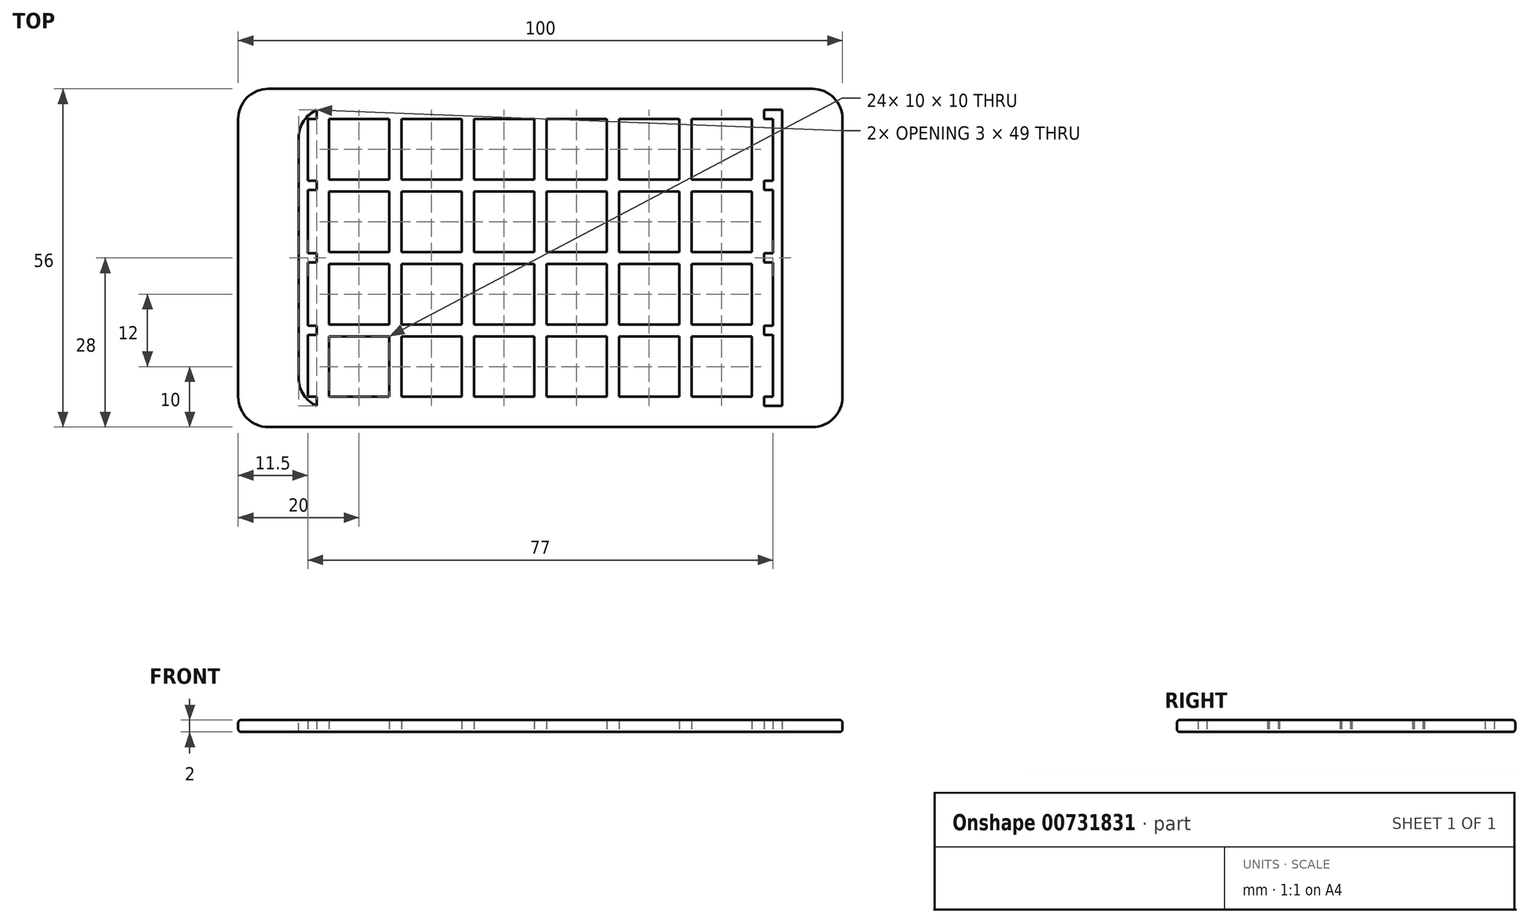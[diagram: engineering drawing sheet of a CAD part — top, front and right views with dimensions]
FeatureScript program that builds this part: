
annotation { "Feature Type Name" : "Feature", "Feature Type Description" : "" }
export const myFeature = defineFeature(function(context is Context, id is Id, definition is map)
    precondition{}
    {
        {
            var Q0;
            Q0=qCreatedBy(makeId("Top.planeOp"),FACE);
            var sketch = newSketch(context, id + "F0", { "sketchPlane" : qUnion([Q0])});
            skLineSegment(sketch, "E0.bottom", {"start": v(5, -5) * mm, "end": v(-5, -5) * mm});
            skLineSegment(sketch, "E0.top", {"start": v(5, 5) * mm, "end": v(-5, 5) * mm});
            skLineSegment(sketch, "E0.left", {"start": v(5, -5) * mm, "end": v(5, 5) * mm});
            skLineSegment(sketch, "E0.right", {"start": v(-5, -5) * mm, "end": v(-5, 5) * mm});
            skPoint(sketch, "E0.middle", {"position": v(0, 0) * mm});
            skPoint(sketch, "E1.0.1.0", {"position": v(0, 12) * mm});
            skLineSegment(sketch, "E1.0.1.1", {"start": v(5, 7) * mm, "end": v(-5, 7) * mm});
            skLineSegment(sketch, "E1.0.1.2", {"start": v(-5, 7) * mm, "end": v(-5, 17) * mm});
            skLineSegment(sketch, "E1.0.1.3", {"start": v(5, 7) * mm, "end": v(5, 17) * mm});
            skLineSegment(sketch, "E1.0.1.4", {"start": v(5, 17) * mm, "end": v(-5, 17) * mm});
            skPoint(sketch, "E1.0.2.0", {"position": v(0, 24) * mm});
            skLineSegment(sketch, "E1.0.2.1", {"start": v(5, 19) * mm, "end": v(-5, 19) * mm});
            skLineSegment(sketch, "E1.0.2.2", {"start": v(-5, 19) * mm, "end": v(-5, 29) * mm});
            skLineSegment(sketch, "E1.0.2.3", {"start": v(5, 19) * mm, "end": v(5, 29) * mm});
            skLineSegment(sketch, "E1.0.2.4", {"start": v(5, 29) * mm, "end": v(-5, 29) * mm});
            skPoint(sketch, "E1.1.0.0", {"position": v(12, 0) * mm});
            skLineSegment(sketch, "E1.1.0.1", {"start": v(17, -5) * mm, "end": v(7, -5) * mm});
            skLineSegment(sketch, "E1.1.0.2", {"start": v(7, -5) * mm, "end": v(7, 5) * mm});
            skLineSegment(sketch, "E1.1.0.3", {"start": v(17, -5) * mm, "end": v(17, 5) * mm});
            skLineSegment(sketch, "E1.1.0.4", {"start": v(17, 5) * mm, "end": v(7, 5) * mm});
            skPoint(sketch, "E1.1.1.0", {"position": v(12, 12) * mm});
            skLineSegment(sketch, "E1.1.1.1", {"start": v(17, 7) * mm, "end": v(7, 7) * mm});
            skLineSegment(sketch, "E1.1.1.2", {"start": v(7, 7) * mm, "end": v(7, 17) * mm});
            skLineSegment(sketch, "E1.1.1.3", {"start": v(17, 7) * mm, "end": v(17, 17) * mm});
            skLineSegment(sketch, "E1.1.1.4", {"start": v(17, 17) * mm, "end": v(7, 17) * mm});
            skPoint(sketch, "E1.1.2.0", {"position": v(12, 24) * mm});
            skLineSegment(sketch, "E1.1.2.1", {"start": v(17, 19) * mm, "end": v(7, 19) * mm});
            skLineSegment(sketch, "E1.1.2.2", {"start": v(7, 19) * mm, "end": v(7, 29) * mm});
            skLineSegment(sketch, "E1.1.2.3", {"start": v(17, 19) * mm, "end": v(17, 29) * mm});
            skLineSegment(sketch, "E1.1.2.4", {"start": v(17, 29) * mm, "end": v(7, 29) * mm});
            skPoint(sketch, "E1.2.0.0", {"position": v(24, 0) * mm});
            skLineSegment(sketch, "E1.2.0.1", {"start": v(29, -5) * mm, "end": v(19, -5) * mm});
            skLineSegment(sketch, "E1.2.0.2", {"start": v(19, -5) * mm, "end": v(19, 5) * mm});
            skLineSegment(sketch, "E1.2.0.3", {"start": v(29, -5) * mm, "end": v(29, 5) * mm});
            skLineSegment(sketch, "E1.2.0.4", {"start": v(29, 5) * mm, "end": v(19, 5) * mm});
            skPoint(sketch, "E1.2.1.0", {"position": v(24, 12) * mm});
            skLineSegment(sketch, "E1.2.1.1", {"start": v(29, 7) * mm, "end": v(19, 7) * mm});
            skLineSegment(sketch, "E1.2.1.2", {"start": v(19, 7) * mm, "end": v(19, 17) * mm});
            skLineSegment(sketch, "E1.2.1.3", {"start": v(29, 7) * mm, "end": v(29, 17) * mm});
            skLineSegment(sketch, "E1.2.1.4", {"start": v(29, 17) * mm, "end": v(19, 17) * mm});
            skPoint(sketch, "E1.2.2.0", {"position": v(24, 24) * mm});
            skLineSegment(sketch, "E1.2.2.1", {"start": v(29, 19) * mm, "end": v(19, 19) * mm});
            skLineSegment(sketch, "E1.2.2.2", {"start": v(19, 19) * mm, "end": v(19, 29) * mm});
            skLineSegment(sketch, "E1.2.2.3", {"start": v(29, 19) * mm, "end": v(29, 29) * mm});
            skLineSegment(sketch, "E1.2.2.4", {"start": v(29, 29) * mm, "end": v(19, 29) * mm});
            skLineSegment(sketch, "E1.direction1", {"start": v(-5, -5) * mm, "end": v(7, -5) * mm, "construction": true});
            skLineSegment(sketch, "E1.direction2", {"start": v(-5, -5) * mm, "end": v(-5, 7) * mm, "construction": true});
            skLineSegment(sketch, "E2.1.0.0", {"start": v(-31, 19) * mm, "end": v(-31, 29) * mm});
            skLineSegment(sketch, "E2.1.0.1", {"start": v(-17, 7) * mm, "end": v(-17, 17) * mm});
            skLineSegment(sketch, "E2.1.0.2", {"start": v(-7, -5) * mm, "end": v(-7, 5) * mm});
            skLineSegment(sketch, "E2.1.0.3", {"start": v(-7, 19) * mm, "end": v(-17, 19) * mm});
            skPoint(sketch, "E2.1.0.4", {"position": v(-24, 12) * mm});
            skLineSegment(sketch, "E2.1.0.5", {"start": v(-19, -5) * mm, "end": v(-19, 5) * mm});
            skLineSegment(sketch, "E2.1.0.6", {"start": v(-41, -5) * mm, "end": v(-29, -5) * mm, "construction": true});
            skLineSegment(sketch, "E2.1.0.7", {"start": v(-31, 5) * mm, "end": v(-41, 5) * mm});
            skLineSegment(sketch, "E2.1.0.8", {"start": v(-41, -5) * mm, "end": v(-41, 7) * mm, "construction": true});
            skPoint(sketch, "E2.1.0.9", {"position": v(-12, 12) * mm});
            skPoint(sketch, "E2.1.0.10", {"position": v(-36, 0) * mm});
            skPoint(sketch, "E2.1.0.11", {"position": v(-12, 24) * mm});
            skLineSegment(sketch, "E2.1.0.12", {"start": v(-31, 7) * mm, "end": v(-31, 17) * mm});
            skLineSegment(sketch, "E2.1.0.13", {"start": v(-29, 19) * mm, "end": v(-29, 29) * mm});
            skLineSegment(sketch, "E2.1.0.14", {"start": v(-31, 7) * mm, "end": v(-41, 7) * mm});
            skLineSegment(sketch, "E2.1.0.15", {"start": v(-31, 19) * mm, "end": v(-41, 19) * mm});
            skLineSegment(sketch, "E2.1.0.16", {"start": v(-19, 17) * mm, "end": v(-29, 17) * mm});
            skLineSegment(sketch, "E2.1.0.17", {"start": v(-19, 29) * mm, "end": v(-29, 29) * mm});
            skLineSegment(sketch, "E2.1.0.18", {"start": v(-19, 19) * mm, "end": v(-29, 19) * mm});
            skLineSegment(sketch, "E2.1.0.19", {"start": v(-7, 7) * mm, "end": v(-17, 7) * mm});
            skLineSegment(sketch, "E2.1.0.20", {"start": v(-19, -5) * mm, "end": v(-29, -5) * mm});
            skLineSegment(sketch, "E2.1.0.21", {"start": v(-41, 19) * mm, "end": v(-41, 29) * mm});
            skLineSegment(sketch, "E2.1.0.22", {"start": v(-29, -5) * mm, "end": v(-29, 5) * mm});
            skLineSegment(sketch, "E2.1.0.23", {"start": v(-19, 5) * mm, "end": v(-29, 5) * mm});
            skPoint(sketch, "E2.1.0.24", {"position": v(-36, 12) * mm});
            skLineSegment(sketch, "E2.1.0.25", {"start": v(-7, -5) * mm, "end": v(-17, -5) * mm});
            skPoint(sketch, "E2.1.0.26", {"position": v(-24, 0) * mm});
            skLineSegment(sketch, "E2.1.0.27", {"start": v(-7, 29) * mm, "end": v(-17, 29) * mm});
            skLineSegment(sketch, "E2.1.0.28", {"start": v(-41, 7) * mm, "end": v(-41, 17) * mm});
            skPoint(sketch, "E2.1.0.29", {"position": v(-24, 24) * mm});
            skLineSegment(sketch, "E2.1.0.30", {"start": v(-19, 7) * mm, "end": v(-29, 7) * mm});
            skPoint(sketch, "E2.1.0.31", {"position": v(-36, 24) * mm});
            skLineSegment(sketch, "E2.1.0.32", {"start": v(-31, 29) * mm, "end": v(-41, 29) * mm});
            skLineSegment(sketch, "E2.1.0.33", {"start": v(-31, -5) * mm, "end": v(-31, 5) * mm});
            skLineSegment(sketch, "E2.1.0.34", {"start": v(-7, 5) * mm, "end": v(-17, 5) * mm});
            skLineSegment(sketch, "E2.1.0.35", {"start": v(-7, 7) * mm, "end": v(-7, 17) * mm});
            skLineSegment(sketch, "E2.1.0.36", {"start": v(-29, 7) * mm, "end": v(-29, 17) * mm});
            skLineSegment(sketch, "E2.1.0.37", {"start": v(-17, 19) * mm, "end": v(-17, 29) * mm});
            skLineSegment(sketch, "E2.1.0.38", {"start": v(-31, 17) * mm, "end": v(-41, 17) * mm});
            skPoint(sketch, "E2.1.0.39", {"position": v(-12, 0) * mm});
            skLineSegment(sketch, "E2.1.0.40", {"start": v(-17, -5) * mm, "end": v(-17, 5) * mm});
            skLineSegment(sketch, "E2.1.0.41", {"start": v(-19, 19) * mm, "end": v(-19, 29) * mm});
            skLineSegment(sketch, "E2.1.0.42", {"start": v(-7, 17) * mm, "end": v(-17, 17) * mm});
            skLineSegment(sketch, "E2.1.0.43", {"start": v(-19, 7) * mm, "end": v(-19, 17) * mm});
            skLineSegment(sketch, "E2.1.0.44", {"start": v(-7, 19) * mm, "end": v(-7, 29) * mm});
            skLineSegment(sketch, "E2.1.0.45", {"start": v(-41, -5) * mm, "end": v(-41, 5) * mm});
            skLineSegment(sketch, "E2.1.0.46", {"start": v(-31, -5) * mm, "end": v(-41, -5) * mm});
            skLineSegment(sketch, "E2.direction1", {"start": v(-5, -5) * mm, "end": v(-41, -5) * mm, "construction": true});
            skPoint(sketch, "E3.0.1.0", {"position": v(24, -12) * mm});
            skLineSegment(sketch, "E3.0.1.1", {"start": v(19, -17) * mm, "end": v(19, -7) * mm});
            skLineSegment(sketch, "E3.0.1.2", {"start": v(7, -17) * mm, "end": v(7, -7) * mm});
            skLineSegment(sketch, "E3.0.1.3", {"start": v(17, -7) * mm, "end": v(7, -7) * mm});
            skLineSegment(sketch, "E3.0.1.4", {"start": v(29, -17) * mm, "end": v(19, -17) * mm});
            skLineSegment(sketch, "E3.0.1.5", {"start": v(-19, -7) * mm, "end": v(-29, -7) * mm});
            skLineSegment(sketch, "E3.0.1.6", {"start": v(-7, -7) * mm, "end": v(-17, -7) * mm});
            skLineSegment(sketch, "E3.0.1.7", {"start": v(5, -7) * mm, "end": v(-5, -7) * mm});
            skLineSegment(sketch, "E3.0.1.8", {"start": v(5, -17) * mm, "end": v(5, -7) * mm});
            skLineSegment(sketch, "E3.0.1.9", {"start": v(17, -17) * mm, "end": v(17, -7) * mm});
            skLineSegment(sketch, "E3.0.1.10", {"start": v(-29, -17) * mm, "end": v(-29, -7) * mm});
            skLineSegment(sketch, "E3.0.1.11", {"start": v(-7, -17) * mm, "end": v(-7, -7) * mm});
            skLineSegment(sketch, "E3.0.1.12", {"start": v(-31, -17) * mm, "end": v(-31, -7) * mm});
            skPoint(sketch, "E3.0.1.13", {"position": v(-24, -12) * mm});
            skLineSegment(sketch, "E3.0.1.14", {"start": v(-19, -17) * mm, "end": v(-19, -7) * mm});
            skLineSegment(sketch, "E3.0.1.15", {"start": v(29, -17) * mm, "end": v(29, -7) * mm});
            skLineSegment(sketch, "E3.0.1.16", {"start": v(-5, -17) * mm, "end": v(-5, -7) * mm});
            skLineSegment(sketch, "E3.0.1.17", {"start": v(-41, -17) * mm, "end": v(-41, -7) * mm});
            skPoint(sketch, "E3.0.1.18", {"position": v(0, -12) * mm});
            skPoint(sketch, "E3.0.1.19", {"position": v(12, -12) * mm});
            skLineSegment(sketch, "E3.0.1.20", {"start": v(29, -7) * mm, "end": v(19, -7) * mm});
            skLineSegment(sketch, "E3.0.1.21", {"start": v(-5, -17) * mm, "end": v(7, -17) * mm, "construction": true});
            skPoint(sketch, "E3.0.1.22", {"position": v(-12, -12) * mm});
            skPoint(sketch, "E3.0.1.23", {"position": v(-36, -12) * mm});
            skLineSegment(sketch, "E3.0.1.24", {"start": v(-31, -7) * mm, "end": v(-41, -7) * mm});
            skLineSegment(sketch, "E3.0.1.25", {"start": v(-5, -17) * mm, "end": v(-41, -17) * mm, "construction": true});
            skLineSegment(sketch, "E3.0.1.26", {"start": v(17, -17) * mm, "end": v(7, -17) * mm});
            skLineSegment(sketch, "E3.0.1.27", {"start": v(-17, -17) * mm, "end": v(-17, -7) * mm});
            skLineSegment(sketch, "E3.0.1.28", {"start": v(5, -17) * mm, "end": v(-5, -17) * mm});
            skLineSegment(sketch, "E3.0.1.29", {"start": v(-19, -17) * mm, "end": v(-29, -17) * mm});
            skLineSegment(sketch, "E3.0.1.30", {"start": v(-7, -17) * mm, "end": v(-17, -17) * mm});
            skLineSegment(sketch, "E3.0.1.31", {"start": v(-41, -17) * mm, "end": v(-29, -17) * mm, "construction": true});
            skLineSegment(sketch, "E3.0.1.32", {"start": v(-31, -17) * mm, "end": v(-41, -17) * mm});
            skLineSegment(sketch, "E3.direction1", {"start": v(-41, -5) * mm, "end": v(-23.4, -5) * mm, "construction": true});
            skLineSegment(sketch, "E3.direction2", {"start": v(-41, -5) * mm, "end": v(-41, -17) * mm, "construction": true});
            skLineSegment(sketch, "E4.bottom", {"start": v(-56, 34) * mm, "end": v(44, 34) * mm});
            skLineSegment(sketch, "E4.top", {"start": v(-56, -22) * mm, "end": v(44, -22) * mm});
            skLineSegment(sketch, "E4.left", {"start": v(-56, 34) * mm, "end": v(-56, -22) * mm});
            skLineSegment(sketch, "E4.right", {"start": v(44, 34) * mm, "end": v(44, -22) * mm});
            skLineSegment(sketch, "E5", {"start": v(-41, 29) * mm, "end": v(-41, 34) * mm});
            skLineSegment(sketch, "E6", {"start": v(-41, 29) * mm, "end": v(-56, 29) * mm});
            skLineSegment(sketch, "E7", {"start": v(29, -17) * mm, "end": v(29, -22) * mm});
            skLineSegment(sketch, "E8", {"start": v(29, -17) * mm, "end": v(44, -17) * mm});
            skLineSegment(sketch, "E9.bottom", {"start": v(-46, 29) * mm, "end": v(-44.5, 29) * mm});
            skLineSegment(sketch, "E9.top", {"start": v(-46, -17) * mm, "end": v(-44.5, -17) * mm});
            skLineSegment(sketch, "E9.left", {"start": v(-46, 29) * mm, "end": v(-46, -17) * mm});
            skLineSegment(sketch, "E9.right", {"start": v(-44.5, 29) * mm, "end": v(-44.5, -17) * mm});
            skLineSegment(sketch, "E10", {"start": v(-46, 29) * mm, "end": v(-46, 34) * mm});
            skLineSegment(sketch, "E11", {"start": v(-46, -17) * mm, "end": v(-46, -22) * mm});
            skLineSegment(sketch, "E12", {"start": v(-46, -17) * mm, "end": v(-56, -17) * mm});
            skLineSegment(sketch, "E13.bottom", {"start": v(-46, 29) * mm, "end": v(-43, 29) * mm});
            skLineSegment(sketch, "E13.top", {"start": v(-46, 30.5) * mm, "end": v(-43, 30.5) * mm});
            skLineSegment(sketch, "E13.left", {"start": v(-46, 29) * mm, "end": v(-46, 30.5) * mm});
            skLineSegment(sketch, "E13.right", {"start": v(-43, 29) * mm, "end": v(-43, 30.5) * mm});
            skLineSegment(sketch, "E14.bottom", {"start": v(-46, -17) * mm, "end": v(-43, -17) * mm});
            skLineSegment(sketch, "E14.top", {"start": v(-46, -18.5) * mm, "end": v(-43, -18.5) * mm});
            skLineSegment(sketch, "E14.left", {"start": v(-46, -17) * mm, "end": v(-46, -18.5) * mm});
            skLineSegment(sketch, "E14.right", {"start": v(-43, -17) * mm, "end": v(-43, -18.5) * mm});
            skLineSegment(sketch, "E15.bottom", {"start": v(32.5, 29) * mm, "end": v(34, 29) * mm});
            skLineSegment(sketch, "E15.top", {"start": v(32.5, -17) * mm, "end": v(34, -17) * mm});
            skLineSegment(sketch, "E15.left", {"start": v(32.5, 29) * mm, "end": v(32.5, -17) * mm});
            skLineSegment(sketch, "E15.right", {"start": v(34, 29) * mm, "end": v(34, -17) * mm});
            skLineSegment(sketch, "E16", {"start": v(34, -17) * mm, "end": v(34, -22) * mm});
            skLineSegment(sketch, "E17", {"start": v(34, -17) * mm, "end": v(44, -17) * mm});
            skLineSegment(sketch, "E18", {"start": v(34, 29) * mm, "end": v(34, 34) * mm});
            skLineSegment(sketch, "E19", {"start": v(34, 29) * mm, "end": v(44, 29) * mm});
            skLineSegment(sketch, "E20.bottom", {"start": v(34, 29) * mm, "end": v(31, 29) * mm});
            skLineSegment(sketch, "E20.top", {"start": v(34, 30.5) * mm, "end": v(31, 30.5) * mm});
            skLineSegment(sketch, "E20.left", {"start": v(34, 29) * mm, "end": v(34, 30.5) * mm});
            skLineSegment(sketch, "E20.right", {"start": v(31, 29) * mm, "end": v(31, 30.5) * mm});
            skLineSegment(sketch, "E21.bottom", {"start": v(34, -17) * mm, "end": v(31, -17) * mm});
            skLineSegment(sketch, "E21.top", {"start": v(34, -18.5) * mm, "end": v(31, -18.5) * mm});
            skLineSegment(sketch, "E21.left", {"start": v(34, -17) * mm, "end": v(34, -18.5) * mm});
            skLineSegment(sketch, "E21.right", {"start": v(31, -17) * mm, "end": v(31, -18.5) * mm});
            skLineSegment(sketch, "E22.bottom", {"start": v(31, 6.75) * mm, "end": v(32.5, 6.75) * mm});
            skLineSegment(sketch, "E22.top", {"start": v(31, 5.25) * mm, "end": v(32.5, 5.25) * mm});
            skLineSegment(sketch, "E22.left", {"start": v(31, 6.75) * mm, "end": v(31, 5.25) * mm});
            skLineSegment(sketch, "E22.right", {"start": v(32.5, 6.75) * mm, "end": v(32.5, 5.25) * mm});
            skLineSegment(sketch, "E23.bottom", {"start": v(32.5, -5.25) * mm, "end": v(31, -5.25) * mm});
            skLineSegment(sketch, "E23.top", {"start": v(32.5, -6.75) * mm, "end": v(31, -6.75) * mm});
            skLineSegment(sketch, "E23.left", {"start": v(32.5, -5.25) * mm, "end": v(32.5, -6.75) * mm});
            skLineSegment(sketch, "E23.right", {"start": v(31, -5.25) * mm, "end": v(31, -6.75) * mm});
            skLineSegment(sketch, "E24.bottom", {"start": v(-44.5, 6.75) * mm, "end": v(-43, 6.75) * mm});
            skLineSegment(sketch, "E24.top", {"start": v(-44.5, 5.25) * mm, "end": v(-43, 5.25) * mm});
            skLineSegment(sketch, "E24.left", {"start": v(-44.5, 6.75) * mm, "end": v(-44.5, 5.25) * mm});
            skLineSegment(sketch, "E24.right", {"start": v(-43, 6.75) * mm, "end": v(-43, 5.25) * mm});
            skLineSegment(sketch, "E25.bottom", {"start": v(-44.5, -5.25) * mm, "end": v(-43, -5.25) * mm});
            skLineSegment(sketch, "E25.top", {"start": v(-44.5, -6.75) * mm, "end": v(-43, -6.75) * mm});
            skLineSegment(sketch, "E25.left", {"start": v(-44.5, -5.25) * mm, "end": v(-44.5, -6.75) * mm});
            skLineSegment(sketch, "E25.right", {"start": v(-43, -5.25) * mm, "end": v(-43, -6.75) * mm});
            skLineSegment(sketch, "E26.bottom", {"start": v(-44.5, 18.75) * mm, "end": v(-43, 18.75) * mm});
            skLineSegment(sketch, "E26.top", {"start": v(-44.5, 17.25) * mm, "end": v(-43, 17.25) * mm});
            skLineSegment(sketch, "E26.left", {"start": v(-44.5, 18.75) * mm, "end": v(-44.5, 17.25) * mm});
            skLineSegment(sketch, "E26.right", {"start": v(-43, 18.75) * mm, "end": v(-43, 17.25) * mm});
            skLineSegment(sketch, "E27", {"start": v(-43, 18.75) * mm, "end": v(-43, 29) * mm});
            skLineSegment(sketch, "E28", {"start": v(-43, -17) * mm, "end": v(-43, -6.75) * mm});
            skLineSegment(sketch, "E29", {"start": v(-43, -5.25) * mm, "end": v(-43, 5.25) * mm});
            skLineSegment(sketch, "E30", {"start": v(-43, 6.75) * mm, "end": v(-43, 17.25) * mm});
            skLineSegment(sketch, "E31.bottom", {"start": v(32.5, 18.75) * mm, "end": v(31, 18.75) * mm});
            skLineSegment(sketch, "E31.top", {"start": v(32.5, 17.25) * mm, "end": v(31, 17.25) * mm});
            skLineSegment(sketch, "E31.left", {"start": v(32.5, 18.75) * mm, "end": v(32.5, 17.25) * mm});
            skLineSegment(sketch, "E31.right", {"start": v(31, 18.75) * mm, "end": v(31, 17.25) * mm});
            skLineSegment(sketch, "E32", {"start": v(31, 29) * mm, "end": v(31, 18.75) * mm});
            skLineSegment(sketch, "E33", {"start": v(31, -6.75) * mm, "end": v(31, -17) * mm});
            skLineSegment(sketch, "E34", {"start": v(31, 17.25) * mm, "end": v(31, 6.75) * mm});
            skLineSegment(sketch, "E35", {"start": v(31, 5.25) * mm, "end": v(31, -5.25) * mm});
            skSolve(sketch);
        }
        {
            var Q0;
            {var subQ1=sQuery(id+"F0.wireOp",EDGE,"E5");Q0=makeQuery(id+"F0.imprint","IMPRINT",FACE,{"disambiguationData":[TD([[makeQuery(id+"F0.imprint","IMPRINT",EDGE,{"derivedFrom":subQ1}),1.0]])]});}
            var Q1;
            Q1=makeQuery(id+"F0.imprint","IMPRINT",FACE,{"disambiguationData":[TD([[makeQuery(id+"F0.imprint","IMPRINT",EDGE,{"derivedFrom":sQuery(id+"F0.wireOp",EDGE,"E0.bottom")}),1.0]])]});
            var Q2;
            {var subQ0=sQuery(id+"F0.wireOp",EDGE,"E18");Q2=makeQuery(id+"F0.imprint","IMPRINT",FACE,{"disambiguationData":[TD([[makeQuery(id+"F0.imprint","IMPRINT",EDGE,{"derivedFrom":subQ0}),-1.0]])]});}
            var Q3;
            Q3=makeQuery(id+"F0.imprint","IMPRINT",FACE,{"disambiguationData":[TD([[makeQuery(id+"F0.imprint","IMPRINT",EDGE,{"derivedFrom":sQuery(id+"F0.wireOp",EDGE,"E15.right")}),1.0]])]});
            var Q4;
            {var subQ1=sQuery(id+"F0.wireOp",EDGE,"E16");Q4=makeQuery(id+"F0.imprint","IMPRINT",FACE,{"disambiguationData":[TD([[makeQuery(id+"F0.imprint","IMPRINT",EDGE,{"derivedFrom":subQ1}),1.0]])]});}
            var Q5;
            {var subQ1=sQuery(id+"F0.wireOp",EDGE,"E7");Q5=makeQuery(id+"F0.imprint","IMPRINT",FACE,{"disambiguationData":[TD([[makeQuery(id+"F0.imprint","IMPRINT",EDGE,{"derivedFrom":subQ1}),1.0]])]});}
            var Q6;
            {var subQ0=sQuery(id+"F0.wireOp",EDGE,"E22.top");Q6=makeQuery(id+"F0.imprint","IMPRINT",FACE,{"disambiguationData":[TD([[makeQuery(id+"F0.imprint","IMPRINT",EDGE,{"derivedFrom":subQ0}),-1.0]])]});}
            var Q7;
            {var subQ3=sQuery(id+"F0.wireOp",EDGE,"E22.bottom");Q7=makeQuery(id+"F0.imprint","IMPRINT",FACE,{"disambiguationData":[TD([[makeQuery(id+"F0.imprint","IMPRINT",EDGE,{"derivedFrom":subQ3}),1.0]])]});}
            var Q8;
            {var subQ4=sQuery(id+"F0.wireOp",EDGE,"E9.left");Q8=makeQuery(id+"F0.imprint","IMPRINT",FACE,{"disambiguationData":[TD([[makeQuery(id+"F0.imprint","IMPRINT",EDGE,{"derivedFrom":subQ4}),-1.0]])]});}
            var Q9;
            {var subQ4=sQuery(id+"F0.wireOp",EDGE,"E11");Q9=makeQuery(id+"F0.imprint","IMPRINT",FACE,{"disambiguationData":[TD([[makeQuery(id+"F0.imprint","IMPRINT",EDGE,{"derivedFrom":subQ4}),-1.0]])]});}
            var Q10;
            {var subQ0=sQuery(id+"F0.wireOp",EDGE,"E10");Q10=makeQuery(id+"F0.imprint","IMPRINT",FACE,{"disambiguationData":[TD([[makeQuery(id+"F0.imprint","IMPRINT",EDGE,{"derivedFrom":subQ0}),1.0]])]});}
            var Q11;
            {var subQ3=sQuery(id+"F0.wireOp",EDGE,"E26.bottom");Q11=makeQuery(id+"F0.imprint","IMPRINT",FACE,{"disambiguationData":[TD([[makeQuery(id+"F0.imprint","IMPRINT",EDGE,{"derivedFrom":subQ3}),1.0]])]});}
            var Q12;
            {var subQ0=sQuery(id+"F0.wireOp",EDGE,"E24.bottom");Q12=makeQuery(id+"F0.imprint","IMPRINT",FACE,{"disambiguationData":[TD([[makeQuery(id+"F0.imprint","IMPRINT",EDGE,{"derivedFrom":subQ0}),1.0]])]});}
            var Q13;
            {var subQ0=sQuery(id+"F0.wireOp",EDGE,"E24.top");Q13=makeQuery(id+"F0.imprint","IMPRINT",FACE,{"disambiguationData":[TD([[makeQuery(id+"F0.imprint","IMPRINT",EDGE,{"derivedFrom":subQ0}),-1.0]])]});}
            var Q14;
            {var subQ3=sQuery(id+"F0.wireOp",EDGE,"E25.top");Q14=makeQuery(id+"F0.imprint","IMPRINT",FACE,{"disambiguationData":[TD([[makeQuery(id+"F0.imprint","IMPRINT",EDGE,{"derivedFrom":subQ3}),-1.0]])]});}
            var Q15;
            {var subQ3=sQuery(id+"F0.wireOp",EDGE,"E31.bottom");Q15=makeQuery(id+"F0.imprint","IMPRINT",FACE,{"disambiguationData":[TD([[makeQuery(id+"F0.imprint","IMPRINT",EDGE,{"derivedFrom":subQ3}),-1.0]])]});}
            var Q16;
            {var subQ3=sQuery(id+"F0.wireOp",EDGE,"E23.top");Q16=makeQuery(id+"F0.imprint","IMPRINT",FACE,{"disambiguationData":[TD([[makeQuery(id+"F0.imprint","IMPRINT",EDGE,{"derivedFrom":subQ3}),1.0]])]});}
            extrude(context, id + "F1", {"entities" : qUnion([Q0, Q1, Q2, Q3, Q4, Q5, Q6, Q7, Q8, Q9, Q10, Q11, Q12, Q13, Q14, Q15, Q16]), "depth" : 2 * mm, "offsetDistance" : 25 * mm});
        }
        {
            var Q0;
            Q0=makeQuery(id+"F1.opExtrude","SWEPT_EDGE",EDGE,{"disambiguationData":[OSD([sQuery(id+"F0.wireOp",EDGE,"E4.bottom"),sQuery(id+"F0.wireOp",EDGE,"E10")])]});
            fillet(context, id + "F2", {"entities" : qUnion([Q0]), "radius" : 5 * mm, "tangentPropagation" : true, "allowEdgeOverflow" : false});
        }
        {
            var Q0;
            Q0=makeQuery(id+"F1.opExtrude","SWEPT_EDGE",EDGE,{"disambiguationData":[OSD([sQuery(id+"F0.wireOp",EDGE,"E4.top"),sQuery(id+"F0.wireOp",EDGE,"E11")])]});
            var Q1;
            Q1=makeQuery(id+"F1.opExtrude","SWEPT_EDGE",EDGE,{"disambiguationData":[OSD([sQuery(id+"F0.wireOp",EDGE,"E4.top"),sQuery(id+"F0.wireOp",EDGE,"E4.right")])]});
            var Q2;
            Q2=makeQuery(id+"F1.opExtrude","SWEPT_EDGE",EDGE,{"disambiguationData":[OSD([sQuery(id+"F0.wireOp",EDGE,"E4.bottom"),sQuery(id+"F0.wireOp",EDGE,"E4.right")])]});
            fillet(context, id + "F3", {"entities" : qUnion([Q0, Q1, Q2]), "radius" : 5 * mm, "tangentPropagation" : true, "allowEdgeOverflow" : false});
        }
        {
            var Q0;
            Q0=makeQuery(id+"F1.opExtrude","CAP_EDGE",EDGE,{"disambiguationData":[OSD([sQuery(id+"F0.wireOp",EDGE,"E4.bottom")])],"isStart":false});
            var Q1;
            Q1=makeQuery(id+"F1.opExtrude","CAP_EDGE",EDGE,{"disambiguationData":[OSD([sQuery(id+"F0.wireOp",EDGE,"E4.bottom")])],"isStart":true});
            var Q2;
            {var subQ0=sQuery(id+"F0.wireOp",EDGE,"E4.bottom");Q2=makeQuery(id+"F2.opFillet","BLEND_EDGE",EDGE,{"blendedFrom":[makeQuery(id+"F1.opExtrude","SWEPT_EDGE",EDGE,{"disambiguationData":[OSD([subQ0,sQuery(id+"F0.wireOp",EDGE,"E4.left")])]}),makeQuery(id+"F1.opExtrude","SWEPT_FACE",FACE,{"disambiguationData":[OSD([subQ0])]})],"blendedInto":[makeQuery(id+"F1.opExtrude","SWEPT_FACE",FACE,{"disambiguationData":[OSD([subQ0])]})]});}
            var Q3;
            {var subQ0=sQuery(id+"F0.wireOp",EDGE,"E4.bottom");Q3=makeQuery(id+"F2.opFillet","BLEND_EDGE",EDGE,{"blendedFrom":[makeQuery(id+"F1.opExtrude","SWEPT_EDGE",EDGE,{"disambiguationData":[OSD([subQ0,sQuery(id+"F0.wireOp",EDGE,"E4.right")])]}),makeQuery(id+"F1.opExtrude","SWEPT_FACE",FACE,{"disambiguationData":[OSD([subQ0])]})],"blendedInto":[makeQuery(id+"F1.opExtrude","SWEPT_FACE",FACE,{"disambiguationData":[OSD([subQ0])]})]});}
            var Q4;
            Q4=makeQuery(id+"F1.opExtrude","CAP_EDGE",EDGE,{"disambiguationData":[OSD([sQuery(id+"F0.wireOp",EDGE,"E4.right")])],"isStart":false});
            var Q5;
            {var subQ0=sQuery(id+"F0.wireOp",EDGE,"E4.right");var subQ1=sQuery(id+"F0.wireOp",EDGE,"E4.top");Q5=makeQuery(id+"F3.opFillet","BLEND_EDGE",EDGE,{"blendedFrom":[makeQuery(id+"F1.opExtrude","SWEPT_EDGE",EDGE,{"disambiguationData":[OSD([subQ1,subQ0])]}),makeQuery(id+"F1.opExtrude","CAP_FACE",FACE,{"disambiguationData":[OSD([sQuery(id+"F0.wireOp",EDGE,"E0.bottom"),sQuery(id+"F0.wireOp",EDGE,"E0.top"),sQuery(id+"F0.wireOp",EDGE,"E0.left"),sQuery(id+"F0.wireOp",EDGE,"E0.right"),sQuery(id+"F0.wireOp",EDGE,"E1.0.1.1"),sQuery(id+"F0.wireOp",EDGE,"E1.0.1.2"),sQuery(id+"F0.wireOp",EDGE,"E1.0.1.3"),sQuery(id+"F0.wireOp",EDGE,"E1.0.1.4"),sQuery(id+"F0.wireOp",EDGE,"E1.0.2.1"),sQuery(id+"F0.wireOp",EDGE,"E1.0.2.2"),sQuery(id+"F0.wireOp",EDGE,"E1.0.2.3"),sQuery(id+"F0.wireOp",EDGE,"E1.0.2.4"),sQuery(id+"F0.wireOp",EDGE,"E1.1.0.1"),sQuery(id+"F0.wireOp",EDGE,"E1.1.0.2"),sQuery(id+"F0.wireOp",EDGE,"E1.1.0.3"),sQuery(id+"F0.wireOp",EDGE,"E1.1.0.4"),sQuery(id+"F0.wireOp",EDGE,"E1.1.1.1"),sQuery(id+"F0.wireOp",EDGE,"E1.1.1.2"),sQuery(id+"F0.wireOp",EDGE,"E1.1.1.3"),sQuery(id+"F0.wireOp",EDGE,"E1.1.1.4"),sQuery(id+"F0.wireOp",EDGE,"E1.1.2.1"),sQuery(id+"F0.wireOp",EDGE,"E1.1.2.2"),sQuery(id+"F0.wireOp",EDGE,"E1.1.2.3"),sQuery(id+"F0.wireOp",EDGE,"E1.1.2.4"),sQuery(id+"F0.wireOp",EDGE,"E1.2.0.1"),sQuery(id+"F0.wireOp",EDGE,"E1.2.0.2"),sQuery(id+"F0.wireOp",EDGE,"E1.2.0.3"),sQuery(id+"F0.wireOp",EDGE,"E1.2.0.4"),sQuery(id+"F0.wireOp",EDGE,"E1.2.1.1"),sQuery(id+"F0.wireOp",EDGE,"E1.2.1.2"),sQuery(id+"F0.wireOp",EDGE,"E1.2.1.3"),sQuery(id+"F0.wireOp",EDGE,"E1.2.1.4"),sQuery(id+"F0.wireOp",EDGE,"E1.2.2.1"),sQuery(id+"F0.wireOp",EDGE,"E1.2.2.2"),sQuery(id+"F0.wireOp",EDGE,"E1.2.2.3"),sQuery(id+"F0.wireOp",EDGE,"E1.2.2.4"),sQuery(id+"F0.wireOp",EDGE,"E2.1.0.0"),sQuery(id+"F0.wireOp",EDGE,"E2.1.0.1"),sQuery(id+"F0.wireOp",EDGE,"E2.1.0.2"),sQuery(id+"F0.wireOp",EDGE,"E2.1.0.3"),sQuery(id+"F0.wireOp",EDGE,"E2.1.0.5"),sQuery(id+"F0.wireOp",EDGE,"E2.1.0.7"),sQuery(id+"F0.wireOp",EDGE,"E2.1.0.12"),sQuery(id+"F0.wireOp",EDGE,"E2.1.0.13"),sQuery(id+"F0.wireOp",EDGE,"E2.1.0.14"),sQuery(id+"F0.wireOp",EDGE,"E2.1.0.15"),sQuery(id+"F0.wireOp",EDGE,"E2.1.0.16"),sQuery(id+"F0.wireOp",EDGE,"E2.1.0.17"),sQuery(id+"F0.wireOp",EDGE,"E2.1.0.18"),sQuery(id+"F0.wireOp",EDGE,"E2.1.0.19"),sQuery(id+"F0.wireOp",EDGE,"E2.1.0.20"),sQuery(id+"F0.wireOp",EDGE,"E2.1.0.21"),sQuery(id+"F0.wireOp",EDGE,"E2.1.0.22"),sQuery(id+"F0.wireOp",EDGE,"E2.1.0.23"),sQuery(id+"F0.wireOp",EDGE,"E2.1.0.25"),sQuery(id+"F0.wireOp",EDGE,"E2.1.0.27"),sQuery(id+"F0.wireOp",EDGE,"E2.1.0.28"),sQuery(id+"F0.wireOp",EDGE,"E2.1.0.30"),sQuery(id+"F0.wireOp",EDGE,"E2.1.0.32"),sQuery(id+"F0.wireOp",EDGE,"E2.1.0.33"),sQuery(id+"F0.wireOp",EDGE,"E2.1.0.34"),sQuery(id+"F0.wireOp",EDGE,"E2.1.0.35"),sQuery(id+"F0.wireOp",EDGE,"E2.1.0.36"),sQuery(id+"F0.wireOp",EDGE,"E2.1.0.37"),sQuery(id+"F0.wireOp",EDGE,"E2.1.0.38"),sQuery(id+"F0.wireOp",EDGE,"E2.1.0.40"),sQuery(id+"F0.wireOp",EDGE,"E2.1.0.41"),sQuery(id+"F0.wireOp",EDGE,"E2.1.0.42"),sQuery(id+"F0.wireOp",EDGE,"E2.1.0.43"),sQuery(id+"F0.wireOp",EDGE,"E2.1.0.44"),sQuery(id+"F0.wireOp",EDGE,"E2.1.0.45"),sQuery(id+"F0.wireOp",EDGE,"E2.1.0.46"),sQuery(id+"F0.wireOp",EDGE,"E3.0.1.1"),sQuery(id+"F0.wireOp",EDGE,"E3.0.1.2"),sQuery(id+"F0.wireOp",EDGE,"E3.0.1.3"),sQuery(id+"F0.wireOp",EDGE,"E3.0.1.4"),sQuery(id+"F0.wireOp",EDGE,"E3.0.1.5"),sQuery(id+"F0.wireOp",EDGE,"E3.0.1.6"),sQuery(id+"F0.wireOp",EDGE,"E3.0.1.7"),sQuery(id+"F0.wireOp",EDGE,"E3.0.1.8"),sQuery(id+"F0.wireOp",EDGE,"E3.0.1.9"),sQuery(id+"F0.wireOp",EDGE,"E3.0.1.10"),sQuery(id+"F0.wireOp",EDGE,"E3.0.1.11"),sQuery(id+"F0.wireOp",EDGE,"E3.0.1.12"),sQuery(id+"F0.wireOp",EDGE,"E3.0.1.14"),sQuery(id+"F0.wireOp",EDGE,"E3.0.1.15"),sQuery(id+"F0.wireOp",EDGE,"E3.0.1.16"),sQuery(id+"F0.wireOp",EDGE,"E3.0.1.17"),sQuery(id+"F0.wireOp",EDGE,"E3.0.1.20"),sQuery(id+"F0.wireOp",EDGE,"E3.0.1.24"),sQuery(id+"F0.wireOp",EDGE,"E3.0.1.26"),sQuery(id+"F0.wireOp",EDGE,"E3.0.1.27"),sQuery(id+"F0.wireOp",EDGE,"E3.0.1.28"),sQuery(id+"F0.wireOp",EDGE,"E3.0.1.29"),sQuery(id+"F0.wireOp",EDGE,"E3.0.1.30"),sQuery(id+"F0.wireOp",EDGE,"E3.0.1.32"),sQuery(id+"F0.wireOp",EDGE,"E4.bottom"),subQ1,sQuery(id+"F0.wireOp",EDGE,"E4.left"),subQ0,sQuery(id+"F0.wireOp",EDGE,"E9.left"),sQuery(id+"F0.wireOp",EDGE,"E9.right"),sQuery(id+"F0.wireOp",EDGE,"E13.bottom"),sQuery(id+"F0.wireOp",EDGE,"E13.top"),sQuery(id+"F0.wireOp",EDGE,"E13.left"),sQuery(id+"F0.wireOp",EDGE,"E13.right"),sQuery(id+"F0.wireOp",EDGE,"E14.bottom"),sQuery(id+"F0.wireOp",EDGE,"E14.top"),sQuery(id+"F0.wireOp",EDGE,"E14.left"),sQuery(id+"F0.wireOp",EDGE,"E14.right"),sQuery(id+"F0.wireOp",EDGE,"E15.left"),sQuery(id+"F0.wireOp",EDGE,"E15.right"),sQuery(id+"F0.wireOp",EDGE,"E20.bottom"),sQuery(id+"F0.wireOp",EDGE,"E20.top"),sQuery(id+"F0.wireOp",EDGE,"E20.left"),sQuery(id+"F0.wireOp",EDGE,"E20.right"),sQuery(id+"F0.wireOp",EDGE,"E21.bottom"),sQuery(id+"F0.wireOp",EDGE,"E21.top"),sQuery(id+"F0.wireOp",EDGE,"E21.left"),sQuery(id+"F0.wireOp",EDGE,"E21.right"),sQuery(id+"F0.wireOp",EDGE,"E22.bottom"),sQuery(id+"F0.wireOp",EDGE,"E22.top"),sQuery(id+"F0.wireOp",EDGE,"E22.left"),sQuery(id+"F0.wireOp",EDGE,"E23.bottom"),sQuery(id+"F0.wireOp",EDGE,"E23.top"),sQuery(id+"F0.wireOp",EDGE,"E23.right"),sQuery(id+"F0.wireOp",EDGE,"E24.bottom"),sQuery(id+"F0.wireOp",EDGE,"E24.top"),sQuery(id+"F0.wireOp",EDGE,"E24.right"),sQuery(id+"F0.wireOp",EDGE,"E25.bottom"),sQuery(id+"F0.wireOp",EDGE,"E25.top"),sQuery(id+"F0.wireOp",EDGE,"E25.right"),sQuery(id+"F0.wireOp",EDGE,"E26.bottom"),sQuery(id+"F0.wireOp",EDGE,"E26.top"),sQuery(id+"F0.wireOp",EDGE,"E26.right"),sQuery(id+"F0.wireOp",EDGE,"E31.bottom"),sQuery(id+"F0.wireOp",EDGE,"E31.top"),sQuery(id+"F0.wireOp",EDGE,"E31.right")])],"isStart":false})],"blendedInto":[makeQuery(id+"F1.opExtrude","CAP_FACE",FACE,{"disambiguationData":[OSD([sQuery(id+"F0.wireOp",EDGE,"E0.bottom"),sQuery(id+"F0.wireOp",EDGE,"E0.top"),sQuery(id+"F0.wireOp",EDGE,"E0.left"),sQuery(id+"F0.wireOp",EDGE,"E0.right"),sQuery(id+"F0.wireOp",EDGE,"E1.0.1.1"),sQuery(id+"F0.wireOp",EDGE,"E1.0.1.2"),sQuery(id+"F0.wireOp",EDGE,"E1.0.1.3"),sQuery(id+"F0.wireOp",EDGE,"E1.0.1.4"),sQuery(id+"F0.wireOp",EDGE,"E1.0.2.1"),sQuery(id+"F0.wireOp",EDGE,"E1.0.2.2"),sQuery(id+"F0.wireOp",EDGE,"E1.0.2.3"),sQuery(id+"F0.wireOp",EDGE,"E1.0.2.4"),sQuery(id+"F0.wireOp",EDGE,"E1.1.0.1"),sQuery(id+"F0.wireOp",EDGE,"E1.1.0.2"),sQuery(id+"F0.wireOp",EDGE,"E1.1.0.3"),sQuery(id+"F0.wireOp",EDGE,"E1.1.0.4"),sQuery(id+"F0.wireOp",EDGE,"E1.1.1.1"),sQuery(id+"F0.wireOp",EDGE,"E1.1.1.2"),sQuery(id+"F0.wireOp",EDGE,"E1.1.1.3"),sQuery(id+"F0.wireOp",EDGE,"E1.1.1.4"),sQuery(id+"F0.wireOp",EDGE,"E1.1.2.1"),sQuery(id+"F0.wireOp",EDGE,"E1.1.2.2"),sQuery(id+"F0.wireOp",EDGE,"E1.1.2.3"),sQuery(id+"F0.wireOp",EDGE,"E1.1.2.4"),sQuery(id+"F0.wireOp",EDGE,"E1.2.0.1"),sQuery(id+"F0.wireOp",EDGE,"E1.2.0.2"),sQuery(id+"F0.wireOp",EDGE,"E1.2.0.3"),sQuery(id+"F0.wireOp",EDGE,"E1.2.0.4"),sQuery(id+"F0.wireOp",EDGE,"E1.2.1.1"),sQuery(id+"F0.wireOp",EDGE,"E1.2.1.2"),sQuery(id+"F0.wireOp",EDGE,"E1.2.1.3"),sQuery(id+"F0.wireOp",EDGE,"E1.2.1.4"),sQuery(id+"F0.wireOp",EDGE,"E1.2.2.1"),sQuery(id+"F0.wireOp",EDGE,"E1.2.2.2"),sQuery(id+"F0.wireOp",EDGE,"E1.2.2.3"),sQuery(id+"F0.wireOp",EDGE,"E1.2.2.4"),sQuery(id+"F0.wireOp",EDGE,"E2.1.0.0"),sQuery(id+"F0.wireOp",EDGE,"E2.1.0.1"),sQuery(id+"F0.wireOp",EDGE,"E2.1.0.2"),sQuery(id+"F0.wireOp",EDGE,"E2.1.0.3"),sQuery(id+"F0.wireOp",EDGE,"E2.1.0.5"),sQuery(id+"F0.wireOp",EDGE,"E2.1.0.7"),sQuery(id+"F0.wireOp",EDGE,"E2.1.0.12"),sQuery(id+"F0.wireOp",EDGE,"E2.1.0.13"),sQuery(id+"F0.wireOp",EDGE,"E2.1.0.14"),sQuery(id+"F0.wireOp",EDGE,"E2.1.0.15"),sQuery(id+"F0.wireOp",EDGE,"E2.1.0.16"),sQuery(id+"F0.wireOp",EDGE,"E2.1.0.17"),sQuery(id+"F0.wireOp",EDGE,"E2.1.0.18"),sQuery(id+"F0.wireOp",EDGE,"E2.1.0.19"),sQuery(id+"F0.wireOp",EDGE,"E2.1.0.20"),sQuery(id+"F0.wireOp",EDGE,"E2.1.0.21"),sQuery(id+"F0.wireOp",EDGE,"E2.1.0.22"),sQuery(id+"F0.wireOp",EDGE,"E2.1.0.23"),sQuery(id+"F0.wireOp",EDGE,"E2.1.0.25"),sQuery(id+"F0.wireOp",EDGE,"E2.1.0.27"),sQuery(id+"F0.wireOp",EDGE,"E2.1.0.28"),sQuery(id+"F0.wireOp",EDGE,"E2.1.0.30"),sQuery(id+"F0.wireOp",EDGE,"E2.1.0.32"),sQuery(id+"F0.wireOp",EDGE,"E2.1.0.33"),sQuery(id+"F0.wireOp",EDGE,"E2.1.0.34"),sQuery(id+"F0.wireOp",EDGE,"E2.1.0.35"),sQuery(id+"F0.wireOp",EDGE,"E2.1.0.36"),sQuery(id+"F0.wireOp",EDGE,"E2.1.0.37"),sQuery(id+"F0.wireOp",EDGE,"E2.1.0.38"),sQuery(id+"F0.wireOp",EDGE,"E2.1.0.40"),sQuery(id+"F0.wireOp",EDGE,"E2.1.0.41"),sQuery(id+"F0.wireOp",EDGE,"E2.1.0.42"),sQuery(id+"F0.wireOp",EDGE,"E2.1.0.43"),sQuery(id+"F0.wireOp",EDGE,"E2.1.0.44"),sQuery(id+"F0.wireOp",EDGE,"E2.1.0.45"),sQuery(id+"F0.wireOp",EDGE,"E2.1.0.46"),sQuery(id+"F0.wireOp",EDGE,"E3.0.1.1"),sQuery(id+"F0.wireOp",EDGE,"E3.0.1.2"),sQuery(id+"F0.wireOp",EDGE,"E3.0.1.3"),sQuery(id+"F0.wireOp",EDGE,"E3.0.1.4"),sQuery(id+"F0.wireOp",EDGE,"E3.0.1.5"),sQuery(id+"F0.wireOp",EDGE,"E3.0.1.6"),sQuery(id+"F0.wireOp",EDGE,"E3.0.1.7"),sQuery(id+"F0.wireOp",EDGE,"E3.0.1.8"),sQuery(id+"F0.wireOp",EDGE,"E3.0.1.9"),sQuery(id+"F0.wireOp",EDGE,"E3.0.1.10"),sQuery(id+"F0.wireOp",EDGE,"E3.0.1.11"),sQuery(id+"F0.wireOp",EDGE,"E3.0.1.12"),sQuery(id+"F0.wireOp",EDGE,"E3.0.1.14"),sQuery(id+"F0.wireOp",EDGE,"E3.0.1.15"),sQuery(id+"F0.wireOp",EDGE,"E3.0.1.16"),sQuery(id+"F0.wireOp",EDGE,"E3.0.1.17"),sQuery(id+"F0.wireOp",EDGE,"E3.0.1.20"),sQuery(id+"F0.wireOp",EDGE,"E3.0.1.24"),sQuery(id+"F0.wireOp",EDGE,"E3.0.1.26"),sQuery(id+"F0.wireOp",EDGE,"E3.0.1.27"),sQuery(id+"F0.wireOp",EDGE,"E3.0.1.28"),sQuery(id+"F0.wireOp",EDGE,"E3.0.1.29"),sQuery(id+"F0.wireOp",EDGE,"E3.0.1.30"),sQuery(id+"F0.wireOp",EDGE,"E3.0.1.32"),sQuery(id+"F0.wireOp",EDGE,"E4.bottom"),subQ1,sQuery(id+"F0.wireOp",EDGE,"E4.left"),subQ0,sQuery(id+"F0.wireOp",EDGE,"E9.left"),sQuery(id+"F0.wireOp",EDGE,"E9.right"),sQuery(id+"F0.wireOp",EDGE,"E13.bottom"),sQuery(id+"F0.wireOp",EDGE,"E13.top"),sQuery(id+"F0.wireOp",EDGE,"E13.left"),sQuery(id+"F0.wireOp",EDGE,"E13.right"),sQuery(id+"F0.wireOp",EDGE,"E14.bottom"),sQuery(id+"F0.wireOp",EDGE,"E14.top"),sQuery(id+"F0.wireOp",EDGE,"E14.left"),sQuery(id+"F0.wireOp",EDGE,"E14.right"),sQuery(id+"F0.wireOp",EDGE,"E15.left"),sQuery(id+"F0.wireOp",EDGE,"E15.right"),sQuery(id+"F0.wireOp",EDGE,"E20.bottom"),sQuery(id+"F0.wireOp",EDGE,"E20.top"),sQuery(id+"F0.wireOp",EDGE,"E20.left"),sQuery(id+"F0.wireOp",EDGE,"E20.right"),sQuery(id+"F0.wireOp",EDGE,"E21.bottom"),sQuery(id+"F0.wireOp",EDGE,"E21.top"),sQuery(id+"F0.wireOp",EDGE,"E21.left"),sQuery(id+"F0.wireOp",EDGE,"E21.right"),sQuery(id+"F0.wireOp",EDGE,"E22.bottom"),sQuery(id+"F0.wireOp",EDGE,"E22.top"),sQuery(id+"F0.wireOp",EDGE,"E22.left"),sQuery(id+"F0.wireOp",EDGE,"E23.bottom"),sQuery(id+"F0.wireOp",EDGE,"E23.top"),sQuery(id+"F0.wireOp",EDGE,"E23.right"),sQuery(id+"F0.wireOp",EDGE,"E24.bottom"),sQuery(id+"F0.wireOp",EDGE,"E24.top"),sQuery(id+"F0.wireOp",EDGE,"E24.right"),sQuery(id+"F0.wireOp",EDGE,"E25.bottom"),sQuery(id+"F0.wireOp",EDGE,"E25.top"),sQuery(id+"F0.wireOp",EDGE,"E25.right"),sQuery(id+"F0.wireOp",EDGE,"E26.bottom"),sQuery(id+"F0.wireOp",EDGE,"E26.top"),sQuery(id+"F0.wireOp",EDGE,"E26.right"),sQuery(id+"F0.wireOp",EDGE,"E31.bottom"),sQuery(id+"F0.wireOp",EDGE,"E31.top"),sQuery(id+"F0.wireOp",EDGE,"E31.right")])],"isStart":false})]});}
            var Q6;
            {var subQ0=sQuery(id+"F0.wireOp",EDGE,"E4.right");Q6=makeQuery(id+"F2.opFillet","BLEND_EDGE",EDGE,{"blendedFrom":[makeQuery(id+"F1.opExtrude","SWEPT_EDGE",EDGE,{"disambiguationData":[OSD([sQuery(id+"F0.wireOp",EDGE,"E4.bottom"),subQ0])]}),makeQuery(id+"F1.opExtrude","SWEPT_FACE",FACE,{"disambiguationData":[OSD([subQ0])]})],"blendedInto":[makeQuery(id+"F1.opExtrude","SWEPT_FACE",FACE,{"disambiguationData":[OSD([subQ0])]})]});}
            var Q7;
            {var subQ0=sQuery(id+"F0.wireOp",EDGE,"E4.right");Q7=makeQuery(id+"F3.opFillet","BLEND_EDGE",EDGE,{"blendedFrom":[makeQuery(id+"F1.opExtrude","SWEPT_EDGE",EDGE,{"disambiguationData":[OSD([sQuery(id+"F0.wireOp",EDGE,"E4.top"),subQ0])]}),makeQuery(id+"F1.opExtrude","SWEPT_FACE",FACE,{"disambiguationData":[OSD([subQ0])]})],"blendedInto":[makeQuery(id+"F1.opExtrude","SWEPT_FACE",FACE,{"disambiguationData":[OSD([subQ0])]})]});}
            var Q8;
            Q8=makeQuery(id+"F1.opExtrude","CAP_EDGE",EDGE,{"disambiguationData":[OSD([sQuery(id+"F0.wireOp",EDGE,"E4.right")])],"isStart":true});
            var Q9;
            {var subQ0=sQuery(id+"F0.wireOp",EDGE,"E4.right");var subQ1=sQuery(id+"F0.wireOp",EDGE,"E4.top");Q9=makeQuery(id+"F3.opFillet","BLEND_EDGE",EDGE,{"blendedFrom":[makeQuery(id+"F1.opExtrude","SWEPT_EDGE",EDGE,{"disambiguationData":[OSD([subQ1,subQ0])]}),makeQuery(id+"F1.opExtrude","CAP_FACE",FACE,{"disambiguationData":[OSD([sQuery(id+"F0.wireOp",EDGE,"E0.bottom"),sQuery(id+"F0.wireOp",EDGE,"E0.top"),sQuery(id+"F0.wireOp",EDGE,"E0.left"),sQuery(id+"F0.wireOp",EDGE,"E0.right"),sQuery(id+"F0.wireOp",EDGE,"E1.0.1.1"),sQuery(id+"F0.wireOp",EDGE,"E1.0.1.2"),sQuery(id+"F0.wireOp",EDGE,"E1.0.1.3"),sQuery(id+"F0.wireOp",EDGE,"E1.0.1.4"),sQuery(id+"F0.wireOp",EDGE,"E1.0.2.1"),sQuery(id+"F0.wireOp",EDGE,"E1.0.2.2"),sQuery(id+"F0.wireOp",EDGE,"E1.0.2.3"),sQuery(id+"F0.wireOp",EDGE,"E1.0.2.4"),sQuery(id+"F0.wireOp",EDGE,"E1.1.0.1"),sQuery(id+"F0.wireOp",EDGE,"E1.1.0.2"),sQuery(id+"F0.wireOp",EDGE,"E1.1.0.3"),sQuery(id+"F0.wireOp",EDGE,"E1.1.0.4"),sQuery(id+"F0.wireOp",EDGE,"E1.1.1.1"),sQuery(id+"F0.wireOp",EDGE,"E1.1.1.2"),sQuery(id+"F0.wireOp",EDGE,"E1.1.1.3"),sQuery(id+"F0.wireOp",EDGE,"E1.1.1.4"),sQuery(id+"F0.wireOp",EDGE,"E1.1.2.1"),sQuery(id+"F0.wireOp",EDGE,"E1.1.2.2"),sQuery(id+"F0.wireOp",EDGE,"E1.1.2.3"),sQuery(id+"F0.wireOp",EDGE,"E1.1.2.4"),sQuery(id+"F0.wireOp",EDGE,"E1.2.0.1"),sQuery(id+"F0.wireOp",EDGE,"E1.2.0.2"),sQuery(id+"F0.wireOp",EDGE,"E1.2.0.3"),sQuery(id+"F0.wireOp",EDGE,"E1.2.0.4"),sQuery(id+"F0.wireOp",EDGE,"E1.2.1.1"),sQuery(id+"F0.wireOp",EDGE,"E1.2.1.2"),sQuery(id+"F0.wireOp",EDGE,"E1.2.1.3"),sQuery(id+"F0.wireOp",EDGE,"E1.2.1.4"),sQuery(id+"F0.wireOp",EDGE,"E1.2.2.1"),sQuery(id+"F0.wireOp",EDGE,"E1.2.2.2"),sQuery(id+"F0.wireOp",EDGE,"E1.2.2.3"),sQuery(id+"F0.wireOp",EDGE,"E1.2.2.4"),sQuery(id+"F0.wireOp",EDGE,"E2.1.0.0"),sQuery(id+"F0.wireOp",EDGE,"E2.1.0.1"),sQuery(id+"F0.wireOp",EDGE,"E2.1.0.2"),sQuery(id+"F0.wireOp",EDGE,"E2.1.0.3"),sQuery(id+"F0.wireOp",EDGE,"E2.1.0.5"),sQuery(id+"F0.wireOp",EDGE,"E2.1.0.7"),sQuery(id+"F0.wireOp",EDGE,"E2.1.0.12"),sQuery(id+"F0.wireOp",EDGE,"E2.1.0.13"),sQuery(id+"F0.wireOp",EDGE,"E2.1.0.14"),sQuery(id+"F0.wireOp",EDGE,"E2.1.0.15"),sQuery(id+"F0.wireOp",EDGE,"E2.1.0.16"),sQuery(id+"F0.wireOp",EDGE,"E2.1.0.17"),sQuery(id+"F0.wireOp",EDGE,"E2.1.0.18"),sQuery(id+"F0.wireOp",EDGE,"E2.1.0.19"),sQuery(id+"F0.wireOp",EDGE,"E2.1.0.20"),sQuery(id+"F0.wireOp",EDGE,"E2.1.0.21"),sQuery(id+"F0.wireOp",EDGE,"E2.1.0.22"),sQuery(id+"F0.wireOp",EDGE,"E2.1.0.23"),sQuery(id+"F0.wireOp",EDGE,"E2.1.0.25"),sQuery(id+"F0.wireOp",EDGE,"E2.1.0.27"),sQuery(id+"F0.wireOp",EDGE,"E2.1.0.28"),sQuery(id+"F0.wireOp",EDGE,"E2.1.0.30"),sQuery(id+"F0.wireOp",EDGE,"E2.1.0.32"),sQuery(id+"F0.wireOp",EDGE,"E2.1.0.33"),sQuery(id+"F0.wireOp",EDGE,"E2.1.0.34"),sQuery(id+"F0.wireOp",EDGE,"E2.1.0.35"),sQuery(id+"F0.wireOp",EDGE,"E2.1.0.36"),sQuery(id+"F0.wireOp",EDGE,"E2.1.0.37"),sQuery(id+"F0.wireOp",EDGE,"E2.1.0.38"),sQuery(id+"F0.wireOp",EDGE,"E2.1.0.40"),sQuery(id+"F0.wireOp",EDGE,"E2.1.0.41"),sQuery(id+"F0.wireOp",EDGE,"E2.1.0.42"),sQuery(id+"F0.wireOp",EDGE,"E2.1.0.43"),sQuery(id+"F0.wireOp",EDGE,"E2.1.0.44"),sQuery(id+"F0.wireOp",EDGE,"E2.1.0.45"),sQuery(id+"F0.wireOp",EDGE,"E2.1.0.46"),sQuery(id+"F0.wireOp",EDGE,"E3.0.1.1"),sQuery(id+"F0.wireOp",EDGE,"E3.0.1.2"),sQuery(id+"F0.wireOp",EDGE,"E3.0.1.3"),sQuery(id+"F0.wireOp",EDGE,"E3.0.1.4"),sQuery(id+"F0.wireOp",EDGE,"E3.0.1.5"),sQuery(id+"F0.wireOp",EDGE,"E3.0.1.6"),sQuery(id+"F0.wireOp",EDGE,"E3.0.1.7"),sQuery(id+"F0.wireOp",EDGE,"E3.0.1.8"),sQuery(id+"F0.wireOp",EDGE,"E3.0.1.9"),sQuery(id+"F0.wireOp",EDGE,"E3.0.1.10"),sQuery(id+"F0.wireOp",EDGE,"E3.0.1.11"),sQuery(id+"F0.wireOp",EDGE,"E3.0.1.12"),sQuery(id+"F0.wireOp",EDGE,"E3.0.1.14"),sQuery(id+"F0.wireOp",EDGE,"E3.0.1.15"),sQuery(id+"F0.wireOp",EDGE,"E3.0.1.16"),sQuery(id+"F0.wireOp",EDGE,"E3.0.1.17"),sQuery(id+"F0.wireOp",EDGE,"E3.0.1.20"),sQuery(id+"F0.wireOp",EDGE,"E3.0.1.24"),sQuery(id+"F0.wireOp",EDGE,"E3.0.1.26"),sQuery(id+"F0.wireOp",EDGE,"E3.0.1.27"),sQuery(id+"F0.wireOp",EDGE,"E3.0.1.28"),sQuery(id+"F0.wireOp",EDGE,"E3.0.1.29"),sQuery(id+"F0.wireOp",EDGE,"E3.0.1.30"),sQuery(id+"F0.wireOp",EDGE,"E3.0.1.32"),sQuery(id+"F0.wireOp",EDGE,"E4.bottom"),subQ1,sQuery(id+"F0.wireOp",EDGE,"E4.left"),subQ0,sQuery(id+"F0.wireOp",EDGE,"E9.left"),sQuery(id+"F0.wireOp",EDGE,"E9.right"),sQuery(id+"F0.wireOp",EDGE,"E13.bottom"),sQuery(id+"F0.wireOp",EDGE,"E13.top"),sQuery(id+"F0.wireOp",EDGE,"E13.left"),sQuery(id+"F0.wireOp",EDGE,"E13.right"),sQuery(id+"F0.wireOp",EDGE,"E14.bottom"),sQuery(id+"F0.wireOp",EDGE,"E14.top"),sQuery(id+"F0.wireOp",EDGE,"E14.left"),sQuery(id+"F0.wireOp",EDGE,"E14.right"),sQuery(id+"F0.wireOp",EDGE,"E15.left"),sQuery(id+"F0.wireOp",EDGE,"E15.right"),sQuery(id+"F0.wireOp",EDGE,"E20.bottom"),sQuery(id+"F0.wireOp",EDGE,"E20.top"),sQuery(id+"F0.wireOp",EDGE,"E20.left"),sQuery(id+"F0.wireOp",EDGE,"E20.right"),sQuery(id+"F0.wireOp",EDGE,"E21.bottom"),sQuery(id+"F0.wireOp",EDGE,"E21.top"),sQuery(id+"F0.wireOp",EDGE,"E21.left"),sQuery(id+"F0.wireOp",EDGE,"E21.right"),sQuery(id+"F0.wireOp",EDGE,"E22.bottom"),sQuery(id+"F0.wireOp",EDGE,"E22.top"),sQuery(id+"F0.wireOp",EDGE,"E22.left"),sQuery(id+"F0.wireOp",EDGE,"E23.bottom"),sQuery(id+"F0.wireOp",EDGE,"E23.top"),sQuery(id+"F0.wireOp",EDGE,"E23.right"),sQuery(id+"F0.wireOp",EDGE,"E24.bottom"),sQuery(id+"F0.wireOp",EDGE,"E24.top"),sQuery(id+"F0.wireOp",EDGE,"E24.right"),sQuery(id+"F0.wireOp",EDGE,"E25.bottom"),sQuery(id+"F0.wireOp",EDGE,"E25.top"),sQuery(id+"F0.wireOp",EDGE,"E25.right"),sQuery(id+"F0.wireOp",EDGE,"E26.bottom"),sQuery(id+"F0.wireOp",EDGE,"E26.top"),sQuery(id+"F0.wireOp",EDGE,"E26.right"),sQuery(id+"F0.wireOp",EDGE,"E31.bottom"),sQuery(id+"F0.wireOp",EDGE,"E31.top"),sQuery(id+"F0.wireOp",EDGE,"E31.right")])],"isStart":true})],"blendedInto":[makeQuery(id+"F1.opExtrude","CAP_FACE",FACE,{"disambiguationData":[OSD([sQuery(id+"F0.wireOp",EDGE,"E0.bottom"),sQuery(id+"F0.wireOp",EDGE,"E0.top"),sQuery(id+"F0.wireOp",EDGE,"E0.left"),sQuery(id+"F0.wireOp",EDGE,"E0.right"),sQuery(id+"F0.wireOp",EDGE,"E1.0.1.1"),sQuery(id+"F0.wireOp",EDGE,"E1.0.1.2"),sQuery(id+"F0.wireOp",EDGE,"E1.0.1.3"),sQuery(id+"F0.wireOp",EDGE,"E1.0.1.4"),sQuery(id+"F0.wireOp",EDGE,"E1.0.2.1"),sQuery(id+"F0.wireOp",EDGE,"E1.0.2.2"),sQuery(id+"F0.wireOp",EDGE,"E1.0.2.3"),sQuery(id+"F0.wireOp",EDGE,"E1.0.2.4"),sQuery(id+"F0.wireOp",EDGE,"E1.1.0.1"),sQuery(id+"F0.wireOp",EDGE,"E1.1.0.2"),sQuery(id+"F0.wireOp",EDGE,"E1.1.0.3"),sQuery(id+"F0.wireOp",EDGE,"E1.1.0.4"),sQuery(id+"F0.wireOp",EDGE,"E1.1.1.1"),sQuery(id+"F0.wireOp",EDGE,"E1.1.1.2"),sQuery(id+"F0.wireOp",EDGE,"E1.1.1.3"),sQuery(id+"F0.wireOp",EDGE,"E1.1.1.4"),sQuery(id+"F0.wireOp",EDGE,"E1.1.2.1"),sQuery(id+"F0.wireOp",EDGE,"E1.1.2.2"),sQuery(id+"F0.wireOp",EDGE,"E1.1.2.3"),sQuery(id+"F0.wireOp",EDGE,"E1.1.2.4"),sQuery(id+"F0.wireOp",EDGE,"E1.2.0.1"),sQuery(id+"F0.wireOp",EDGE,"E1.2.0.2"),sQuery(id+"F0.wireOp",EDGE,"E1.2.0.3"),sQuery(id+"F0.wireOp",EDGE,"E1.2.0.4"),sQuery(id+"F0.wireOp",EDGE,"E1.2.1.1"),sQuery(id+"F0.wireOp",EDGE,"E1.2.1.2"),sQuery(id+"F0.wireOp",EDGE,"E1.2.1.3"),sQuery(id+"F0.wireOp",EDGE,"E1.2.1.4"),sQuery(id+"F0.wireOp",EDGE,"E1.2.2.1"),sQuery(id+"F0.wireOp",EDGE,"E1.2.2.2"),sQuery(id+"F0.wireOp",EDGE,"E1.2.2.3"),sQuery(id+"F0.wireOp",EDGE,"E1.2.2.4"),sQuery(id+"F0.wireOp",EDGE,"E2.1.0.0"),sQuery(id+"F0.wireOp",EDGE,"E2.1.0.1"),sQuery(id+"F0.wireOp",EDGE,"E2.1.0.2"),sQuery(id+"F0.wireOp",EDGE,"E2.1.0.3"),sQuery(id+"F0.wireOp",EDGE,"E2.1.0.5"),sQuery(id+"F0.wireOp",EDGE,"E2.1.0.7"),sQuery(id+"F0.wireOp",EDGE,"E2.1.0.12"),sQuery(id+"F0.wireOp",EDGE,"E2.1.0.13"),sQuery(id+"F0.wireOp",EDGE,"E2.1.0.14"),sQuery(id+"F0.wireOp",EDGE,"E2.1.0.15"),sQuery(id+"F0.wireOp",EDGE,"E2.1.0.16"),sQuery(id+"F0.wireOp",EDGE,"E2.1.0.17"),sQuery(id+"F0.wireOp",EDGE,"E2.1.0.18"),sQuery(id+"F0.wireOp",EDGE,"E2.1.0.19"),sQuery(id+"F0.wireOp",EDGE,"E2.1.0.20"),sQuery(id+"F0.wireOp",EDGE,"E2.1.0.21"),sQuery(id+"F0.wireOp",EDGE,"E2.1.0.22"),sQuery(id+"F0.wireOp",EDGE,"E2.1.0.23"),sQuery(id+"F0.wireOp",EDGE,"E2.1.0.25"),sQuery(id+"F0.wireOp",EDGE,"E2.1.0.27"),sQuery(id+"F0.wireOp",EDGE,"E2.1.0.28"),sQuery(id+"F0.wireOp",EDGE,"E2.1.0.30"),sQuery(id+"F0.wireOp",EDGE,"E2.1.0.32"),sQuery(id+"F0.wireOp",EDGE,"E2.1.0.33"),sQuery(id+"F0.wireOp",EDGE,"E2.1.0.34"),sQuery(id+"F0.wireOp",EDGE,"E2.1.0.35"),sQuery(id+"F0.wireOp",EDGE,"E2.1.0.36"),sQuery(id+"F0.wireOp",EDGE,"E2.1.0.37"),sQuery(id+"F0.wireOp",EDGE,"E2.1.0.38"),sQuery(id+"F0.wireOp",EDGE,"E2.1.0.40"),sQuery(id+"F0.wireOp",EDGE,"E2.1.0.41"),sQuery(id+"F0.wireOp",EDGE,"E2.1.0.42"),sQuery(id+"F0.wireOp",EDGE,"E2.1.0.43"),sQuery(id+"F0.wireOp",EDGE,"E2.1.0.44"),sQuery(id+"F0.wireOp",EDGE,"E2.1.0.45"),sQuery(id+"F0.wireOp",EDGE,"E2.1.0.46"),sQuery(id+"F0.wireOp",EDGE,"E3.0.1.1"),sQuery(id+"F0.wireOp",EDGE,"E3.0.1.2"),sQuery(id+"F0.wireOp",EDGE,"E3.0.1.3"),sQuery(id+"F0.wireOp",EDGE,"E3.0.1.4"),sQuery(id+"F0.wireOp",EDGE,"E3.0.1.5"),sQuery(id+"F0.wireOp",EDGE,"E3.0.1.6"),sQuery(id+"F0.wireOp",EDGE,"E3.0.1.7"),sQuery(id+"F0.wireOp",EDGE,"E3.0.1.8"),sQuery(id+"F0.wireOp",EDGE,"E3.0.1.9"),sQuery(id+"F0.wireOp",EDGE,"E3.0.1.10"),sQuery(id+"F0.wireOp",EDGE,"E3.0.1.11"),sQuery(id+"F0.wireOp",EDGE,"E3.0.1.12"),sQuery(id+"F0.wireOp",EDGE,"E3.0.1.14"),sQuery(id+"F0.wireOp",EDGE,"E3.0.1.15"),sQuery(id+"F0.wireOp",EDGE,"E3.0.1.16"),sQuery(id+"F0.wireOp",EDGE,"E3.0.1.17"),sQuery(id+"F0.wireOp",EDGE,"E3.0.1.20"),sQuery(id+"F0.wireOp",EDGE,"E3.0.1.24"),sQuery(id+"F0.wireOp",EDGE,"E3.0.1.26"),sQuery(id+"F0.wireOp",EDGE,"E3.0.1.27"),sQuery(id+"F0.wireOp",EDGE,"E3.0.1.28"),sQuery(id+"F0.wireOp",EDGE,"E3.0.1.29"),sQuery(id+"F0.wireOp",EDGE,"E3.0.1.30"),sQuery(id+"F0.wireOp",EDGE,"E3.0.1.32"),sQuery(id+"F0.wireOp",EDGE,"E4.bottom"),subQ1,sQuery(id+"F0.wireOp",EDGE,"E4.left"),subQ0,sQuery(id+"F0.wireOp",EDGE,"E9.left"),sQuery(id+"F0.wireOp",EDGE,"E9.right"),sQuery(id+"F0.wireOp",EDGE,"E13.bottom"),sQuery(id+"F0.wireOp",EDGE,"E13.top"),sQuery(id+"F0.wireOp",EDGE,"E13.left"),sQuery(id+"F0.wireOp",EDGE,"E13.right"),sQuery(id+"F0.wireOp",EDGE,"E14.bottom"),sQuery(id+"F0.wireOp",EDGE,"E14.top"),sQuery(id+"F0.wireOp",EDGE,"E14.left"),sQuery(id+"F0.wireOp",EDGE,"E14.right"),sQuery(id+"F0.wireOp",EDGE,"E15.left"),sQuery(id+"F0.wireOp",EDGE,"E15.right"),sQuery(id+"F0.wireOp",EDGE,"E20.bottom"),sQuery(id+"F0.wireOp",EDGE,"E20.top"),sQuery(id+"F0.wireOp",EDGE,"E20.left"),sQuery(id+"F0.wireOp",EDGE,"E20.right"),sQuery(id+"F0.wireOp",EDGE,"E21.bottom"),sQuery(id+"F0.wireOp",EDGE,"E21.top"),sQuery(id+"F0.wireOp",EDGE,"E21.left"),sQuery(id+"F0.wireOp",EDGE,"E21.right"),sQuery(id+"F0.wireOp",EDGE,"E22.bottom"),sQuery(id+"F0.wireOp",EDGE,"E22.top"),sQuery(id+"F0.wireOp",EDGE,"E22.left"),sQuery(id+"F0.wireOp",EDGE,"E23.bottom"),sQuery(id+"F0.wireOp",EDGE,"E23.top"),sQuery(id+"F0.wireOp",EDGE,"E23.right"),sQuery(id+"F0.wireOp",EDGE,"E24.bottom"),sQuery(id+"F0.wireOp",EDGE,"E24.top"),sQuery(id+"F0.wireOp",EDGE,"E24.right"),sQuery(id+"F0.wireOp",EDGE,"E25.bottom"),sQuery(id+"F0.wireOp",EDGE,"E25.top"),sQuery(id+"F0.wireOp",EDGE,"E25.right"),sQuery(id+"F0.wireOp",EDGE,"E26.bottom"),sQuery(id+"F0.wireOp",EDGE,"E26.top"),sQuery(id+"F0.wireOp",EDGE,"E26.right"),sQuery(id+"F0.wireOp",EDGE,"E31.bottom"),sQuery(id+"F0.wireOp",EDGE,"E31.top"),sQuery(id+"F0.wireOp",EDGE,"E31.right")])],"isStart":true})]});}
            var Q10;
            {var subQ0=sQuery(id+"F0.wireOp",EDGE,"E4.right");var subQ1=sQuery(id+"F0.wireOp",EDGE,"E4.bottom");Q10=makeQuery(id+"F2.opFillet","BLEND_EDGE",EDGE,{"blendedFrom":[makeQuery(id+"F1.opExtrude","SWEPT_EDGE",EDGE,{"disambiguationData":[OSD([subQ1,subQ0])]}),makeQuery(id+"F1.opExtrude","CAP_FACE",FACE,{"disambiguationData":[OSD([sQuery(id+"F0.wireOp",EDGE,"E0.bottom"),sQuery(id+"F0.wireOp",EDGE,"E0.top"),sQuery(id+"F0.wireOp",EDGE,"E0.left"),sQuery(id+"F0.wireOp",EDGE,"E0.right"),sQuery(id+"F0.wireOp",EDGE,"E1.0.1.1"),sQuery(id+"F0.wireOp",EDGE,"E1.0.1.2"),sQuery(id+"F0.wireOp",EDGE,"E1.0.1.3"),sQuery(id+"F0.wireOp",EDGE,"E1.0.1.4"),sQuery(id+"F0.wireOp",EDGE,"E1.0.2.1"),sQuery(id+"F0.wireOp",EDGE,"E1.0.2.2"),sQuery(id+"F0.wireOp",EDGE,"E1.0.2.3"),sQuery(id+"F0.wireOp",EDGE,"E1.0.2.4"),sQuery(id+"F0.wireOp",EDGE,"E1.1.0.1"),sQuery(id+"F0.wireOp",EDGE,"E1.1.0.2"),sQuery(id+"F0.wireOp",EDGE,"E1.1.0.3"),sQuery(id+"F0.wireOp",EDGE,"E1.1.0.4"),sQuery(id+"F0.wireOp",EDGE,"E1.1.1.1"),sQuery(id+"F0.wireOp",EDGE,"E1.1.1.2"),sQuery(id+"F0.wireOp",EDGE,"E1.1.1.3"),sQuery(id+"F0.wireOp",EDGE,"E1.1.1.4"),sQuery(id+"F0.wireOp",EDGE,"E1.1.2.1"),sQuery(id+"F0.wireOp",EDGE,"E1.1.2.2"),sQuery(id+"F0.wireOp",EDGE,"E1.1.2.3"),sQuery(id+"F0.wireOp",EDGE,"E1.1.2.4"),sQuery(id+"F0.wireOp",EDGE,"E1.2.0.1"),sQuery(id+"F0.wireOp",EDGE,"E1.2.0.2"),sQuery(id+"F0.wireOp",EDGE,"E1.2.0.3"),sQuery(id+"F0.wireOp",EDGE,"E1.2.0.4"),sQuery(id+"F0.wireOp",EDGE,"E1.2.1.1"),sQuery(id+"F0.wireOp",EDGE,"E1.2.1.2"),sQuery(id+"F0.wireOp",EDGE,"E1.2.1.3"),sQuery(id+"F0.wireOp",EDGE,"E1.2.1.4"),sQuery(id+"F0.wireOp",EDGE,"E1.2.2.1"),sQuery(id+"F0.wireOp",EDGE,"E1.2.2.2"),sQuery(id+"F0.wireOp",EDGE,"E1.2.2.3"),sQuery(id+"F0.wireOp",EDGE,"E1.2.2.4"),sQuery(id+"F0.wireOp",EDGE,"E2.1.0.0"),sQuery(id+"F0.wireOp",EDGE,"E2.1.0.1"),sQuery(id+"F0.wireOp",EDGE,"E2.1.0.2"),sQuery(id+"F0.wireOp",EDGE,"E2.1.0.3"),sQuery(id+"F0.wireOp",EDGE,"E2.1.0.5"),sQuery(id+"F0.wireOp",EDGE,"E2.1.0.7"),sQuery(id+"F0.wireOp",EDGE,"E2.1.0.12"),sQuery(id+"F0.wireOp",EDGE,"E2.1.0.13"),sQuery(id+"F0.wireOp",EDGE,"E2.1.0.14"),sQuery(id+"F0.wireOp",EDGE,"E2.1.0.15"),sQuery(id+"F0.wireOp",EDGE,"E2.1.0.16"),sQuery(id+"F0.wireOp",EDGE,"E2.1.0.17"),sQuery(id+"F0.wireOp",EDGE,"E2.1.0.18"),sQuery(id+"F0.wireOp",EDGE,"E2.1.0.19"),sQuery(id+"F0.wireOp",EDGE,"E2.1.0.20"),sQuery(id+"F0.wireOp",EDGE,"E2.1.0.21"),sQuery(id+"F0.wireOp",EDGE,"E2.1.0.22"),sQuery(id+"F0.wireOp",EDGE,"E2.1.0.23"),sQuery(id+"F0.wireOp",EDGE,"E2.1.0.25"),sQuery(id+"F0.wireOp",EDGE,"E2.1.0.27"),sQuery(id+"F0.wireOp",EDGE,"E2.1.0.28"),sQuery(id+"F0.wireOp",EDGE,"E2.1.0.30"),sQuery(id+"F0.wireOp",EDGE,"E2.1.0.32"),sQuery(id+"F0.wireOp",EDGE,"E2.1.0.33"),sQuery(id+"F0.wireOp",EDGE,"E2.1.0.34"),sQuery(id+"F0.wireOp",EDGE,"E2.1.0.35"),sQuery(id+"F0.wireOp",EDGE,"E2.1.0.36"),sQuery(id+"F0.wireOp",EDGE,"E2.1.0.37"),sQuery(id+"F0.wireOp",EDGE,"E2.1.0.38"),sQuery(id+"F0.wireOp",EDGE,"E2.1.0.40"),sQuery(id+"F0.wireOp",EDGE,"E2.1.0.41"),sQuery(id+"F0.wireOp",EDGE,"E2.1.0.42"),sQuery(id+"F0.wireOp",EDGE,"E2.1.0.43"),sQuery(id+"F0.wireOp",EDGE,"E2.1.0.44"),sQuery(id+"F0.wireOp",EDGE,"E2.1.0.45"),sQuery(id+"F0.wireOp",EDGE,"E2.1.0.46"),sQuery(id+"F0.wireOp",EDGE,"E3.0.1.1"),sQuery(id+"F0.wireOp",EDGE,"E3.0.1.2"),sQuery(id+"F0.wireOp",EDGE,"E3.0.1.3"),sQuery(id+"F0.wireOp",EDGE,"E3.0.1.4"),sQuery(id+"F0.wireOp",EDGE,"E3.0.1.5"),sQuery(id+"F0.wireOp",EDGE,"E3.0.1.6"),sQuery(id+"F0.wireOp",EDGE,"E3.0.1.7"),sQuery(id+"F0.wireOp",EDGE,"E3.0.1.8"),sQuery(id+"F0.wireOp",EDGE,"E3.0.1.9"),sQuery(id+"F0.wireOp",EDGE,"E3.0.1.10"),sQuery(id+"F0.wireOp",EDGE,"E3.0.1.11"),sQuery(id+"F0.wireOp",EDGE,"E3.0.1.12"),sQuery(id+"F0.wireOp",EDGE,"E3.0.1.14"),sQuery(id+"F0.wireOp",EDGE,"E3.0.1.15"),sQuery(id+"F0.wireOp",EDGE,"E3.0.1.16"),sQuery(id+"F0.wireOp",EDGE,"E3.0.1.17"),sQuery(id+"F0.wireOp",EDGE,"E3.0.1.20"),sQuery(id+"F0.wireOp",EDGE,"E3.0.1.24"),sQuery(id+"F0.wireOp",EDGE,"E3.0.1.26"),sQuery(id+"F0.wireOp",EDGE,"E3.0.1.27"),sQuery(id+"F0.wireOp",EDGE,"E3.0.1.28"),sQuery(id+"F0.wireOp",EDGE,"E3.0.1.29"),sQuery(id+"F0.wireOp",EDGE,"E3.0.1.30"),sQuery(id+"F0.wireOp",EDGE,"E3.0.1.32"),subQ1,sQuery(id+"F0.wireOp",EDGE,"E4.top"),sQuery(id+"F0.wireOp",EDGE,"E4.left"),subQ0,sQuery(id+"F0.wireOp",EDGE,"E9.left"),sQuery(id+"F0.wireOp",EDGE,"E9.right"),sQuery(id+"F0.wireOp",EDGE,"E13.bottom"),sQuery(id+"F0.wireOp",EDGE,"E13.top"),sQuery(id+"F0.wireOp",EDGE,"E13.left"),sQuery(id+"F0.wireOp",EDGE,"E13.right"),sQuery(id+"F0.wireOp",EDGE,"E14.bottom"),sQuery(id+"F0.wireOp",EDGE,"E14.top"),sQuery(id+"F0.wireOp",EDGE,"E14.left"),sQuery(id+"F0.wireOp",EDGE,"E14.right"),sQuery(id+"F0.wireOp",EDGE,"E15.left"),sQuery(id+"F0.wireOp",EDGE,"E15.right"),sQuery(id+"F0.wireOp",EDGE,"E20.bottom"),sQuery(id+"F0.wireOp",EDGE,"E20.top"),sQuery(id+"F0.wireOp",EDGE,"E20.left"),sQuery(id+"F0.wireOp",EDGE,"E20.right"),sQuery(id+"F0.wireOp",EDGE,"E21.bottom"),sQuery(id+"F0.wireOp",EDGE,"E21.top"),sQuery(id+"F0.wireOp",EDGE,"E21.left"),sQuery(id+"F0.wireOp",EDGE,"E21.right"),sQuery(id+"F0.wireOp",EDGE,"E22.bottom"),sQuery(id+"F0.wireOp",EDGE,"E22.top"),sQuery(id+"F0.wireOp",EDGE,"E22.left"),sQuery(id+"F0.wireOp",EDGE,"E23.bottom"),sQuery(id+"F0.wireOp",EDGE,"E23.top"),sQuery(id+"F0.wireOp",EDGE,"E23.right"),sQuery(id+"F0.wireOp",EDGE,"E24.bottom"),sQuery(id+"F0.wireOp",EDGE,"E24.top"),sQuery(id+"F0.wireOp",EDGE,"E24.right"),sQuery(id+"F0.wireOp",EDGE,"E25.bottom"),sQuery(id+"F0.wireOp",EDGE,"E25.top"),sQuery(id+"F0.wireOp",EDGE,"E25.right"),sQuery(id+"F0.wireOp",EDGE,"E26.bottom"),sQuery(id+"F0.wireOp",EDGE,"E26.top"),sQuery(id+"F0.wireOp",EDGE,"E26.right"),sQuery(id+"F0.wireOp",EDGE,"E31.bottom"),sQuery(id+"F0.wireOp",EDGE,"E31.top"),sQuery(id+"F0.wireOp",EDGE,"E31.right")])],"isStart":false})],"blendedInto":[makeQuery(id+"F1.opExtrude","CAP_FACE",FACE,{"disambiguationData":[OSD([sQuery(id+"F0.wireOp",EDGE,"E0.bottom"),sQuery(id+"F0.wireOp",EDGE,"E0.top"),sQuery(id+"F0.wireOp",EDGE,"E0.left"),sQuery(id+"F0.wireOp",EDGE,"E0.right"),sQuery(id+"F0.wireOp",EDGE,"E1.0.1.1"),sQuery(id+"F0.wireOp",EDGE,"E1.0.1.2"),sQuery(id+"F0.wireOp",EDGE,"E1.0.1.3"),sQuery(id+"F0.wireOp",EDGE,"E1.0.1.4"),sQuery(id+"F0.wireOp",EDGE,"E1.0.2.1"),sQuery(id+"F0.wireOp",EDGE,"E1.0.2.2"),sQuery(id+"F0.wireOp",EDGE,"E1.0.2.3"),sQuery(id+"F0.wireOp",EDGE,"E1.0.2.4"),sQuery(id+"F0.wireOp",EDGE,"E1.1.0.1"),sQuery(id+"F0.wireOp",EDGE,"E1.1.0.2"),sQuery(id+"F0.wireOp",EDGE,"E1.1.0.3"),sQuery(id+"F0.wireOp",EDGE,"E1.1.0.4"),sQuery(id+"F0.wireOp",EDGE,"E1.1.1.1"),sQuery(id+"F0.wireOp",EDGE,"E1.1.1.2"),sQuery(id+"F0.wireOp",EDGE,"E1.1.1.3"),sQuery(id+"F0.wireOp",EDGE,"E1.1.1.4"),sQuery(id+"F0.wireOp",EDGE,"E1.1.2.1"),sQuery(id+"F0.wireOp",EDGE,"E1.1.2.2"),sQuery(id+"F0.wireOp",EDGE,"E1.1.2.3"),sQuery(id+"F0.wireOp",EDGE,"E1.1.2.4"),sQuery(id+"F0.wireOp",EDGE,"E1.2.0.1"),sQuery(id+"F0.wireOp",EDGE,"E1.2.0.2"),sQuery(id+"F0.wireOp",EDGE,"E1.2.0.3"),sQuery(id+"F0.wireOp",EDGE,"E1.2.0.4"),sQuery(id+"F0.wireOp",EDGE,"E1.2.1.1"),sQuery(id+"F0.wireOp",EDGE,"E1.2.1.2"),sQuery(id+"F0.wireOp",EDGE,"E1.2.1.3"),sQuery(id+"F0.wireOp",EDGE,"E1.2.1.4"),sQuery(id+"F0.wireOp",EDGE,"E1.2.2.1"),sQuery(id+"F0.wireOp",EDGE,"E1.2.2.2"),sQuery(id+"F0.wireOp",EDGE,"E1.2.2.3"),sQuery(id+"F0.wireOp",EDGE,"E1.2.2.4"),sQuery(id+"F0.wireOp",EDGE,"E2.1.0.0"),sQuery(id+"F0.wireOp",EDGE,"E2.1.0.1"),sQuery(id+"F0.wireOp",EDGE,"E2.1.0.2"),sQuery(id+"F0.wireOp",EDGE,"E2.1.0.3"),sQuery(id+"F0.wireOp",EDGE,"E2.1.0.5"),sQuery(id+"F0.wireOp",EDGE,"E2.1.0.7"),sQuery(id+"F0.wireOp",EDGE,"E2.1.0.12"),sQuery(id+"F0.wireOp",EDGE,"E2.1.0.13"),sQuery(id+"F0.wireOp",EDGE,"E2.1.0.14"),sQuery(id+"F0.wireOp",EDGE,"E2.1.0.15"),sQuery(id+"F0.wireOp",EDGE,"E2.1.0.16"),sQuery(id+"F0.wireOp",EDGE,"E2.1.0.17"),sQuery(id+"F0.wireOp",EDGE,"E2.1.0.18"),sQuery(id+"F0.wireOp",EDGE,"E2.1.0.19"),sQuery(id+"F0.wireOp",EDGE,"E2.1.0.20"),sQuery(id+"F0.wireOp",EDGE,"E2.1.0.21"),sQuery(id+"F0.wireOp",EDGE,"E2.1.0.22"),sQuery(id+"F0.wireOp",EDGE,"E2.1.0.23"),sQuery(id+"F0.wireOp",EDGE,"E2.1.0.25"),sQuery(id+"F0.wireOp",EDGE,"E2.1.0.27"),sQuery(id+"F0.wireOp",EDGE,"E2.1.0.28"),sQuery(id+"F0.wireOp",EDGE,"E2.1.0.30"),sQuery(id+"F0.wireOp",EDGE,"E2.1.0.32"),sQuery(id+"F0.wireOp",EDGE,"E2.1.0.33"),sQuery(id+"F0.wireOp",EDGE,"E2.1.0.34"),sQuery(id+"F0.wireOp",EDGE,"E2.1.0.35"),sQuery(id+"F0.wireOp",EDGE,"E2.1.0.36"),sQuery(id+"F0.wireOp",EDGE,"E2.1.0.37"),sQuery(id+"F0.wireOp",EDGE,"E2.1.0.38"),sQuery(id+"F0.wireOp",EDGE,"E2.1.0.40"),sQuery(id+"F0.wireOp",EDGE,"E2.1.0.41"),sQuery(id+"F0.wireOp",EDGE,"E2.1.0.42"),sQuery(id+"F0.wireOp",EDGE,"E2.1.0.43"),sQuery(id+"F0.wireOp",EDGE,"E2.1.0.44"),sQuery(id+"F0.wireOp",EDGE,"E2.1.0.45"),sQuery(id+"F0.wireOp",EDGE,"E2.1.0.46"),sQuery(id+"F0.wireOp",EDGE,"E3.0.1.1"),sQuery(id+"F0.wireOp",EDGE,"E3.0.1.2"),sQuery(id+"F0.wireOp",EDGE,"E3.0.1.3"),sQuery(id+"F0.wireOp",EDGE,"E3.0.1.4"),sQuery(id+"F0.wireOp",EDGE,"E3.0.1.5"),sQuery(id+"F0.wireOp",EDGE,"E3.0.1.6"),sQuery(id+"F0.wireOp",EDGE,"E3.0.1.7"),sQuery(id+"F0.wireOp",EDGE,"E3.0.1.8"),sQuery(id+"F0.wireOp",EDGE,"E3.0.1.9"),sQuery(id+"F0.wireOp",EDGE,"E3.0.1.10"),sQuery(id+"F0.wireOp",EDGE,"E3.0.1.11"),sQuery(id+"F0.wireOp",EDGE,"E3.0.1.12"),sQuery(id+"F0.wireOp",EDGE,"E3.0.1.14"),sQuery(id+"F0.wireOp",EDGE,"E3.0.1.15"),sQuery(id+"F0.wireOp",EDGE,"E3.0.1.16"),sQuery(id+"F0.wireOp",EDGE,"E3.0.1.17"),sQuery(id+"F0.wireOp",EDGE,"E3.0.1.20"),sQuery(id+"F0.wireOp",EDGE,"E3.0.1.24"),sQuery(id+"F0.wireOp",EDGE,"E3.0.1.26"),sQuery(id+"F0.wireOp",EDGE,"E3.0.1.27"),sQuery(id+"F0.wireOp",EDGE,"E3.0.1.28"),sQuery(id+"F0.wireOp",EDGE,"E3.0.1.29"),sQuery(id+"F0.wireOp",EDGE,"E3.0.1.30"),sQuery(id+"F0.wireOp",EDGE,"E3.0.1.32"),subQ1,sQuery(id+"F0.wireOp",EDGE,"E4.top"),sQuery(id+"F0.wireOp",EDGE,"E4.left"),subQ0,sQuery(id+"F0.wireOp",EDGE,"E9.left"),sQuery(id+"F0.wireOp",EDGE,"E9.right"),sQuery(id+"F0.wireOp",EDGE,"E13.bottom"),sQuery(id+"F0.wireOp",EDGE,"E13.top"),sQuery(id+"F0.wireOp",EDGE,"E13.left"),sQuery(id+"F0.wireOp",EDGE,"E13.right"),sQuery(id+"F0.wireOp",EDGE,"E14.bottom"),sQuery(id+"F0.wireOp",EDGE,"E14.top"),sQuery(id+"F0.wireOp",EDGE,"E14.left"),sQuery(id+"F0.wireOp",EDGE,"E14.right"),sQuery(id+"F0.wireOp",EDGE,"E15.left"),sQuery(id+"F0.wireOp",EDGE,"E15.right"),sQuery(id+"F0.wireOp",EDGE,"E20.bottom"),sQuery(id+"F0.wireOp",EDGE,"E20.top"),sQuery(id+"F0.wireOp",EDGE,"E20.left"),sQuery(id+"F0.wireOp",EDGE,"E20.right"),sQuery(id+"F0.wireOp",EDGE,"E21.bottom"),sQuery(id+"F0.wireOp",EDGE,"E21.top"),sQuery(id+"F0.wireOp",EDGE,"E21.left"),sQuery(id+"F0.wireOp",EDGE,"E21.right"),sQuery(id+"F0.wireOp",EDGE,"E22.bottom"),sQuery(id+"F0.wireOp",EDGE,"E22.top"),sQuery(id+"F0.wireOp",EDGE,"E22.left"),sQuery(id+"F0.wireOp",EDGE,"E23.bottom"),sQuery(id+"F0.wireOp",EDGE,"E23.top"),sQuery(id+"F0.wireOp",EDGE,"E23.right"),sQuery(id+"F0.wireOp",EDGE,"E24.bottom"),sQuery(id+"F0.wireOp",EDGE,"E24.top"),sQuery(id+"F0.wireOp",EDGE,"E24.right"),sQuery(id+"F0.wireOp",EDGE,"E25.bottom"),sQuery(id+"F0.wireOp",EDGE,"E25.top"),sQuery(id+"F0.wireOp",EDGE,"E25.right"),sQuery(id+"F0.wireOp",EDGE,"E26.bottom"),sQuery(id+"F0.wireOp",EDGE,"E26.top"),sQuery(id+"F0.wireOp",EDGE,"E26.right"),sQuery(id+"F0.wireOp",EDGE,"E31.bottom"),sQuery(id+"F0.wireOp",EDGE,"E31.top"),sQuery(id+"F0.wireOp",EDGE,"E31.right")])],"isStart":false})]});}
            var Q11;
            Q11=makeQuery(id+"F1.opExtrude","CAP_EDGE",EDGE,{"disambiguationData":[OSD([sQuery(id+"F0.wireOp",EDGE,"E4.top")])],"isStart":false});
            var Q12;
            {var subQ0=sQuery(id+"F0.wireOp",EDGE,"E4.right");var subQ1=sQuery(id+"F0.wireOp",EDGE,"E4.bottom");Q12=makeQuery(id+"F2.opFillet","BLEND_EDGE",EDGE,{"blendedFrom":[makeQuery(id+"F1.opExtrude","SWEPT_EDGE",EDGE,{"disambiguationData":[OSD([subQ1,subQ0])]}),makeQuery(id+"F1.opExtrude","CAP_FACE",FACE,{"disambiguationData":[OSD([sQuery(id+"F0.wireOp",EDGE,"E0.bottom"),sQuery(id+"F0.wireOp",EDGE,"E0.top"),sQuery(id+"F0.wireOp",EDGE,"E0.left"),sQuery(id+"F0.wireOp",EDGE,"E0.right"),sQuery(id+"F0.wireOp",EDGE,"E1.0.1.1"),sQuery(id+"F0.wireOp",EDGE,"E1.0.1.2"),sQuery(id+"F0.wireOp",EDGE,"E1.0.1.3"),sQuery(id+"F0.wireOp",EDGE,"E1.0.1.4"),sQuery(id+"F0.wireOp",EDGE,"E1.0.2.1"),sQuery(id+"F0.wireOp",EDGE,"E1.0.2.2"),sQuery(id+"F0.wireOp",EDGE,"E1.0.2.3"),sQuery(id+"F0.wireOp",EDGE,"E1.0.2.4"),sQuery(id+"F0.wireOp",EDGE,"E1.1.0.1"),sQuery(id+"F0.wireOp",EDGE,"E1.1.0.2"),sQuery(id+"F0.wireOp",EDGE,"E1.1.0.3"),sQuery(id+"F0.wireOp",EDGE,"E1.1.0.4"),sQuery(id+"F0.wireOp",EDGE,"E1.1.1.1"),sQuery(id+"F0.wireOp",EDGE,"E1.1.1.2"),sQuery(id+"F0.wireOp",EDGE,"E1.1.1.3"),sQuery(id+"F0.wireOp",EDGE,"E1.1.1.4"),sQuery(id+"F0.wireOp",EDGE,"E1.1.2.1"),sQuery(id+"F0.wireOp",EDGE,"E1.1.2.2"),sQuery(id+"F0.wireOp",EDGE,"E1.1.2.3"),sQuery(id+"F0.wireOp",EDGE,"E1.1.2.4"),sQuery(id+"F0.wireOp",EDGE,"E1.2.0.1"),sQuery(id+"F0.wireOp",EDGE,"E1.2.0.2"),sQuery(id+"F0.wireOp",EDGE,"E1.2.0.3"),sQuery(id+"F0.wireOp",EDGE,"E1.2.0.4"),sQuery(id+"F0.wireOp",EDGE,"E1.2.1.1"),sQuery(id+"F0.wireOp",EDGE,"E1.2.1.2"),sQuery(id+"F0.wireOp",EDGE,"E1.2.1.3"),sQuery(id+"F0.wireOp",EDGE,"E1.2.1.4"),sQuery(id+"F0.wireOp",EDGE,"E1.2.2.1"),sQuery(id+"F0.wireOp",EDGE,"E1.2.2.2"),sQuery(id+"F0.wireOp",EDGE,"E1.2.2.3"),sQuery(id+"F0.wireOp",EDGE,"E1.2.2.4"),sQuery(id+"F0.wireOp",EDGE,"E2.1.0.0"),sQuery(id+"F0.wireOp",EDGE,"E2.1.0.1"),sQuery(id+"F0.wireOp",EDGE,"E2.1.0.2"),sQuery(id+"F0.wireOp",EDGE,"E2.1.0.3"),sQuery(id+"F0.wireOp",EDGE,"E2.1.0.5"),sQuery(id+"F0.wireOp",EDGE,"E2.1.0.7"),sQuery(id+"F0.wireOp",EDGE,"E2.1.0.12"),sQuery(id+"F0.wireOp",EDGE,"E2.1.0.13"),sQuery(id+"F0.wireOp",EDGE,"E2.1.0.14"),sQuery(id+"F0.wireOp",EDGE,"E2.1.0.15"),sQuery(id+"F0.wireOp",EDGE,"E2.1.0.16"),sQuery(id+"F0.wireOp",EDGE,"E2.1.0.17"),sQuery(id+"F0.wireOp",EDGE,"E2.1.0.18"),sQuery(id+"F0.wireOp",EDGE,"E2.1.0.19"),sQuery(id+"F0.wireOp",EDGE,"E2.1.0.20"),sQuery(id+"F0.wireOp",EDGE,"E2.1.0.21"),sQuery(id+"F0.wireOp",EDGE,"E2.1.0.22"),sQuery(id+"F0.wireOp",EDGE,"E2.1.0.23"),sQuery(id+"F0.wireOp",EDGE,"E2.1.0.25"),sQuery(id+"F0.wireOp",EDGE,"E2.1.0.27"),sQuery(id+"F0.wireOp",EDGE,"E2.1.0.28"),sQuery(id+"F0.wireOp",EDGE,"E2.1.0.30"),sQuery(id+"F0.wireOp",EDGE,"E2.1.0.32"),sQuery(id+"F0.wireOp",EDGE,"E2.1.0.33"),sQuery(id+"F0.wireOp",EDGE,"E2.1.0.34"),sQuery(id+"F0.wireOp",EDGE,"E2.1.0.35"),sQuery(id+"F0.wireOp",EDGE,"E2.1.0.36"),sQuery(id+"F0.wireOp",EDGE,"E2.1.0.37"),sQuery(id+"F0.wireOp",EDGE,"E2.1.0.38"),sQuery(id+"F0.wireOp",EDGE,"E2.1.0.40"),sQuery(id+"F0.wireOp",EDGE,"E2.1.0.41"),sQuery(id+"F0.wireOp",EDGE,"E2.1.0.42"),sQuery(id+"F0.wireOp",EDGE,"E2.1.0.43"),sQuery(id+"F0.wireOp",EDGE,"E2.1.0.44"),sQuery(id+"F0.wireOp",EDGE,"E2.1.0.45"),sQuery(id+"F0.wireOp",EDGE,"E2.1.0.46"),sQuery(id+"F0.wireOp",EDGE,"E3.0.1.1"),sQuery(id+"F0.wireOp",EDGE,"E3.0.1.2"),sQuery(id+"F0.wireOp",EDGE,"E3.0.1.3"),sQuery(id+"F0.wireOp",EDGE,"E3.0.1.4"),sQuery(id+"F0.wireOp",EDGE,"E3.0.1.5"),sQuery(id+"F0.wireOp",EDGE,"E3.0.1.6"),sQuery(id+"F0.wireOp",EDGE,"E3.0.1.7"),sQuery(id+"F0.wireOp",EDGE,"E3.0.1.8"),sQuery(id+"F0.wireOp",EDGE,"E3.0.1.9"),sQuery(id+"F0.wireOp",EDGE,"E3.0.1.10"),sQuery(id+"F0.wireOp",EDGE,"E3.0.1.11"),sQuery(id+"F0.wireOp",EDGE,"E3.0.1.12"),sQuery(id+"F0.wireOp",EDGE,"E3.0.1.14"),sQuery(id+"F0.wireOp",EDGE,"E3.0.1.15"),sQuery(id+"F0.wireOp",EDGE,"E3.0.1.16"),sQuery(id+"F0.wireOp",EDGE,"E3.0.1.17"),sQuery(id+"F0.wireOp",EDGE,"E3.0.1.20"),sQuery(id+"F0.wireOp",EDGE,"E3.0.1.24"),sQuery(id+"F0.wireOp",EDGE,"E3.0.1.26"),sQuery(id+"F0.wireOp",EDGE,"E3.0.1.27"),sQuery(id+"F0.wireOp",EDGE,"E3.0.1.28"),sQuery(id+"F0.wireOp",EDGE,"E3.0.1.29"),sQuery(id+"F0.wireOp",EDGE,"E3.0.1.30"),sQuery(id+"F0.wireOp",EDGE,"E3.0.1.32"),subQ1,sQuery(id+"F0.wireOp",EDGE,"E4.top"),sQuery(id+"F0.wireOp",EDGE,"E4.left"),subQ0,sQuery(id+"F0.wireOp",EDGE,"E9.left"),sQuery(id+"F0.wireOp",EDGE,"E9.right"),sQuery(id+"F0.wireOp",EDGE,"E13.bottom"),sQuery(id+"F0.wireOp",EDGE,"E13.top"),sQuery(id+"F0.wireOp",EDGE,"E13.left"),sQuery(id+"F0.wireOp",EDGE,"E13.right"),sQuery(id+"F0.wireOp",EDGE,"E14.bottom"),sQuery(id+"F0.wireOp",EDGE,"E14.top"),sQuery(id+"F0.wireOp",EDGE,"E14.left"),sQuery(id+"F0.wireOp",EDGE,"E14.right"),sQuery(id+"F0.wireOp",EDGE,"E15.left"),sQuery(id+"F0.wireOp",EDGE,"E15.right"),sQuery(id+"F0.wireOp",EDGE,"E20.bottom"),sQuery(id+"F0.wireOp",EDGE,"E20.top"),sQuery(id+"F0.wireOp",EDGE,"E20.left"),sQuery(id+"F0.wireOp",EDGE,"E20.right"),sQuery(id+"F0.wireOp",EDGE,"E21.bottom"),sQuery(id+"F0.wireOp",EDGE,"E21.top"),sQuery(id+"F0.wireOp",EDGE,"E21.left"),sQuery(id+"F0.wireOp",EDGE,"E21.right"),sQuery(id+"F0.wireOp",EDGE,"E22.bottom"),sQuery(id+"F0.wireOp",EDGE,"E22.top"),sQuery(id+"F0.wireOp",EDGE,"E22.left"),sQuery(id+"F0.wireOp",EDGE,"E23.bottom"),sQuery(id+"F0.wireOp",EDGE,"E23.top"),sQuery(id+"F0.wireOp",EDGE,"E23.right"),sQuery(id+"F0.wireOp",EDGE,"E24.bottom"),sQuery(id+"F0.wireOp",EDGE,"E24.top"),sQuery(id+"F0.wireOp",EDGE,"E24.right"),sQuery(id+"F0.wireOp",EDGE,"E25.bottom"),sQuery(id+"F0.wireOp",EDGE,"E25.top"),sQuery(id+"F0.wireOp",EDGE,"E25.right"),sQuery(id+"F0.wireOp",EDGE,"E26.bottom"),sQuery(id+"F0.wireOp",EDGE,"E26.top"),sQuery(id+"F0.wireOp",EDGE,"E26.right"),sQuery(id+"F0.wireOp",EDGE,"E31.bottom"),sQuery(id+"F0.wireOp",EDGE,"E31.top"),sQuery(id+"F0.wireOp",EDGE,"E31.right")])],"isStart":true})],"blendedInto":[makeQuery(id+"F1.opExtrude","CAP_FACE",FACE,{"disambiguationData":[OSD([sQuery(id+"F0.wireOp",EDGE,"E0.bottom"),sQuery(id+"F0.wireOp",EDGE,"E0.top"),sQuery(id+"F0.wireOp",EDGE,"E0.left"),sQuery(id+"F0.wireOp",EDGE,"E0.right"),sQuery(id+"F0.wireOp",EDGE,"E1.0.1.1"),sQuery(id+"F0.wireOp",EDGE,"E1.0.1.2"),sQuery(id+"F0.wireOp",EDGE,"E1.0.1.3"),sQuery(id+"F0.wireOp",EDGE,"E1.0.1.4"),sQuery(id+"F0.wireOp",EDGE,"E1.0.2.1"),sQuery(id+"F0.wireOp",EDGE,"E1.0.2.2"),sQuery(id+"F0.wireOp",EDGE,"E1.0.2.3"),sQuery(id+"F0.wireOp",EDGE,"E1.0.2.4"),sQuery(id+"F0.wireOp",EDGE,"E1.1.0.1"),sQuery(id+"F0.wireOp",EDGE,"E1.1.0.2"),sQuery(id+"F0.wireOp",EDGE,"E1.1.0.3"),sQuery(id+"F0.wireOp",EDGE,"E1.1.0.4"),sQuery(id+"F0.wireOp",EDGE,"E1.1.1.1"),sQuery(id+"F0.wireOp",EDGE,"E1.1.1.2"),sQuery(id+"F0.wireOp",EDGE,"E1.1.1.3"),sQuery(id+"F0.wireOp",EDGE,"E1.1.1.4"),sQuery(id+"F0.wireOp",EDGE,"E1.1.2.1"),sQuery(id+"F0.wireOp",EDGE,"E1.1.2.2"),sQuery(id+"F0.wireOp",EDGE,"E1.1.2.3"),sQuery(id+"F0.wireOp",EDGE,"E1.1.2.4"),sQuery(id+"F0.wireOp",EDGE,"E1.2.0.1"),sQuery(id+"F0.wireOp",EDGE,"E1.2.0.2"),sQuery(id+"F0.wireOp",EDGE,"E1.2.0.3"),sQuery(id+"F0.wireOp",EDGE,"E1.2.0.4"),sQuery(id+"F0.wireOp",EDGE,"E1.2.1.1"),sQuery(id+"F0.wireOp",EDGE,"E1.2.1.2"),sQuery(id+"F0.wireOp",EDGE,"E1.2.1.3"),sQuery(id+"F0.wireOp",EDGE,"E1.2.1.4"),sQuery(id+"F0.wireOp",EDGE,"E1.2.2.1"),sQuery(id+"F0.wireOp",EDGE,"E1.2.2.2"),sQuery(id+"F0.wireOp",EDGE,"E1.2.2.3"),sQuery(id+"F0.wireOp",EDGE,"E1.2.2.4"),sQuery(id+"F0.wireOp",EDGE,"E2.1.0.0"),sQuery(id+"F0.wireOp",EDGE,"E2.1.0.1"),sQuery(id+"F0.wireOp",EDGE,"E2.1.0.2"),sQuery(id+"F0.wireOp",EDGE,"E2.1.0.3"),sQuery(id+"F0.wireOp",EDGE,"E2.1.0.5"),sQuery(id+"F0.wireOp",EDGE,"E2.1.0.7"),sQuery(id+"F0.wireOp",EDGE,"E2.1.0.12"),sQuery(id+"F0.wireOp",EDGE,"E2.1.0.13"),sQuery(id+"F0.wireOp",EDGE,"E2.1.0.14"),sQuery(id+"F0.wireOp",EDGE,"E2.1.0.15"),sQuery(id+"F0.wireOp",EDGE,"E2.1.0.16"),sQuery(id+"F0.wireOp",EDGE,"E2.1.0.17"),sQuery(id+"F0.wireOp",EDGE,"E2.1.0.18"),sQuery(id+"F0.wireOp",EDGE,"E2.1.0.19"),sQuery(id+"F0.wireOp",EDGE,"E2.1.0.20"),sQuery(id+"F0.wireOp",EDGE,"E2.1.0.21"),sQuery(id+"F0.wireOp",EDGE,"E2.1.0.22"),sQuery(id+"F0.wireOp",EDGE,"E2.1.0.23"),sQuery(id+"F0.wireOp",EDGE,"E2.1.0.25"),sQuery(id+"F0.wireOp",EDGE,"E2.1.0.27"),sQuery(id+"F0.wireOp",EDGE,"E2.1.0.28"),sQuery(id+"F0.wireOp",EDGE,"E2.1.0.30"),sQuery(id+"F0.wireOp",EDGE,"E2.1.0.32"),sQuery(id+"F0.wireOp",EDGE,"E2.1.0.33"),sQuery(id+"F0.wireOp",EDGE,"E2.1.0.34"),sQuery(id+"F0.wireOp",EDGE,"E2.1.0.35"),sQuery(id+"F0.wireOp",EDGE,"E2.1.0.36"),sQuery(id+"F0.wireOp",EDGE,"E2.1.0.37"),sQuery(id+"F0.wireOp",EDGE,"E2.1.0.38"),sQuery(id+"F0.wireOp",EDGE,"E2.1.0.40"),sQuery(id+"F0.wireOp",EDGE,"E2.1.0.41"),sQuery(id+"F0.wireOp",EDGE,"E2.1.0.42"),sQuery(id+"F0.wireOp",EDGE,"E2.1.0.43"),sQuery(id+"F0.wireOp",EDGE,"E2.1.0.44"),sQuery(id+"F0.wireOp",EDGE,"E2.1.0.45"),sQuery(id+"F0.wireOp",EDGE,"E2.1.0.46"),sQuery(id+"F0.wireOp",EDGE,"E3.0.1.1"),sQuery(id+"F0.wireOp",EDGE,"E3.0.1.2"),sQuery(id+"F0.wireOp",EDGE,"E3.0.1.3"),sQuery(id+"F0.wireOp",EDGE,"E3.0.1.4"),sQuery(id+"F0.wireOp",EDGE,"E3.0.1.5"),sQuery(id+"F0.wireOp",EDGE,"E3.0.1.6"),sQuery(id+"F0.wireOp",EDGE,"E3.0.1.7"),sQuery(id+"F0.wireOp",EDGE,"E3.0.1.8"),sQuery(id+"F0.wireOp",EDGE,"E3.0.1.9"),sQuery(id+"F0.wireOp",EDGE,"E3.0.1.10"),sQuery(id+"F0.wireOp",EDGE,"E3.0.1.11"),sQuery(id+"F0.wireOp",EDGE,"E3.0.1.12"),sQuery(id+"F0.wireOp",EDGE,"E3.0.1.14"),sQuery(id+"F0.wireOp",EDGE,"E3.0.1.15"),sQuery(id+"F0.wireOp",EDGE,"E3.0.1.16"),sQuery(id+"F0.wireOp",EDGE,"E3.0.1.17"),sQuery(id+"F0.wireOp",EDGE,"E3.0.1.20"),sQuery(id+"F0.wireOp",EDGE,"E3.0.1.24"),sQuery(id+"F0.wireOp",EDGE,"E3.0.1.26"),sQuery(id+"F0.wireOp",EDGE,"E3.0.1.27"),sQuery(id+"F0.wireOp",EDGE,"E3.0.1.28"),sQuery(id+"F0.wireOp",EDGE,"E3.0.1.29"),sQuery(id+"F0.wireOp",EDGE,"E3.0.1.30"),sQuery(id+"F0.wireOp",EDGE,"E3.0.1.32"),subQ1,sQuery(id+"F0.wireOp",EDGE,"E4.top"),sQuery(id+"F0.wireOp",EDGE,"E4.left"),subQ0,sQuery(id+"F0.wireOp",EDGE,"E9.left"),sQuery(id+"F0.wireOp",EDGE,"E9.right"),sQuery(id+"F0.wireOp",EDGE,"E13.bottom"),sQuery(id+"F0.wireOp",EDGE,"E13.top"),sQuery(id+"F0.wireOp",EDGE,"E13.left"),sQuery(id+"F0.wireOp",EDGE,"E13.right"),sQuery(id+"F0.wireOp",EDGE,"E14.bottom"),sQuery(id+"F0.wireOp",EDGE,"E14.top"),sQuery(id+"F0.wireOp",EDGE,"E14.left"),sQuery(id+"F0.wireOp",EDGE,"E14.right"),sQuery(id+"F0.wireOp",EDGE,"E15.left"),sQuery(id+"F0.wireOp",EDGE,"E15.right"),sQuery(id+"F0.wireOp",EDGE,"E20.bottom"),sQuery(id+"F0.wireOp",EDGE,"E20.top"),sQuery(id+"F0.wireOp",EDGE,"E20.left"),sQuery(id+"F0.wireOp",EDGE,"E20.right"),sQuery(id+"F0.wireOp",EDGE,"E21.bottom"),sQuery(id+"F0.wireOp",EDGE,"E21.top"),sQuery(id+"F0.wireOp",EDGE,"E21.left"),sQuery(id+"F0.wireOp",EDGE,"E21.right"),sQuery(id+"F0.wireOp",EDGE,"E22.bottom"),sQuery(id+"F0.wireOp",EDGE,"E22.top"),sQuery(id+"F0.wireOp",EDGE,"E22.left"),sQuery(id+"F0.wireOp",EDGE,"E23.bottom"),sQuery(id+"F0.wireOp",EDGE,"E23.top"),sQuery(id+"F0.wireOp",EDGE,"E23.right"),sQuery(id+"F0.wireOp",EDGE,"E24.bottom"),sQuery(id+"F0.wireOp",EDGE,"E24.top"),sQuery(id+"F0.wireOp",EDGE,"E24.right"),sQuery(id+"F0.wireOp",EDGE,"E25.bottom"),sQuery(id+"F0.wireOp",EDGE,"E25.top"),sQuery(id+"F0.wireOp",EDGE,"E25.right"),sQuery(id+"F0.wireOp",EDGE,"E26.bottom"),sQuery(id+"F0.wireOp",EDGE,"E26.top"),sQuery(id+"F0.wireOp",EDGE,"E26.right"),sQuery(id+"F0.wireOp",EDGE,"E31.bottom"),sQuery(id+"F0.wireOp",EDGE,"E31.top"),sQuery(id+"F0.wireOp",EDGE,"E31.right")])],"isStart":true})]});}
            var Q13;
            {var subQ0=sQuery(id+"F0.wireOp",EDGE,"E4.top");Q13=makeQuery(id+"F3.opFillet","BLEND_EDGE",EDGE,{"blendedFrom":[makeQuery(id+"F1.opExtrude","SWEPT_EDGE",EDGE,{"disambiguationData":[OSD([subQ0,sQuery(id+"F0.wireOp",EDGE,"E4.right")])]}),makeQuery(id+"F1.opExtrude","SWEPT_FACE",FACE,{"disambiguationData":[OSD([subQ0])]})],"blendedInto":[makeQuery(id+"F1.opExtrude","SWEPT_FACE",FACE,{"disambiguationData":[OSD([subQ0])]})]});}
            var Q14;
            Q14=makeQuery(id+"F1.opExtrude","CAP_EDGE",EDGE,{"disambiguationData":[OSD([sQuery(id+"F0.wireOp",EDGE,"E4.top")])],"isStart":true});
            var Q15;
            {var subQ0=sQuery(id+"F0.wireOp",EDGE,"E4.left");var subQ1=sQuery(id+"F0.wireOp",EDGE,"E4.top");Q15=makeQuery(id+"F3.opFillet","BLEND_EDGE",EDGE,{"blendedFrom":[makeQuery(id+"F1.opExtrude","SWEPT_EDGE",EDGE,{"disambiguationData":[OSD([subQ1,subQ0])]}),makeQuery(id+"F1.opExtrude","CAP_FACE",FACE,{"disambiguationData":[OSD([sQuery(id+"F0.wireOp",EDGE,"E0.bottom"),sQuery(id+"F0.wireOp",EDGE,"E0.top"),sQuery(id+"F0.wireOp",EDGE,"E0.left"),sQuery(id+"F0.wireOp",EDGE,"E0.right"),sQuery(id+"F0.wireOp",EDGE,"E1.0.1.1"),sQuery(id+"F0.wireOp",EDGE,"E1.0.1.2"),sQuery(id+"F0.wireOp",EDGE,"E1.0.1.3"),sQuery(id+"F0.wireOp",EDGE,"E1.0.1.4"),sQuery(id+"F0.wireOp",EDGE,"E1.0.2.1"),sQuery(id+"F0.wireOp",EDGE,"E1.0.2.2"),sQuery(id+"F0.wireOp",EDGE,"E1.0.2.3"),sQuery(id+"F0.wireOp",EDGE,"E1.0.2.4"),sQuery(id+"F0.wireOp",EDGE,"E1.1.0.1"),sQuery(id+"F0.wireOp",EDGE,"E1.1.0.2"),sQuery(id+"F0.wireOp",EDGE,"E1.1.0.3"),sQuery(id+"F0.wireOp",EDGE,"E1.1.0.4"),sQuery(id+"F0.wireOp",EDGE,"E1.1.1.1"),sQuery(id+"F0.wireOp",EDGE,"E1.1.1.2"),sQuery(id+"F0.wireOp",EDGE,"E1.1.1.3"),sQuery(id+"F0.wireOp",EDGE,"E1.1.1.4"),sQuery(id+"F0.wireOp",EDGE,"E1.1.2.1"),sQuery(id+"F0.wireOp",EDGE,"E1.1.2.2"),sQuery(id+"F0.wireOp",EDGE,"E1.1.2.3"),sQuery(id+"F0.wireOp",EDGE,"E1.1.2.4"),sQuery(id+"F0.wireOp",EDGE,"E1.2.0.1"),sQuery(id+"F0.wireOp",EDGE,"E1.2.0.2"),sQuery(id+"F0.wireOp",EDGE,"E1.2.0.3"),sQuery(id+"F0.wireOp",EDGE,"E1.2.0.4"),sQuery(id+"F0.wireOp",EDGE,"E1.2.1.1"),sQuery(id+"F0.wireOp",EDGE,"E1.2.1.2"),sQuery(id+"F0.wireOp",EDGE,"E1.2.1.3"),sQuery(id+"F0.wireOp",EDGE,"E1.2.1.4"),sQuery(id+"F0.wireOp",EDGE,"E1.2.2.1"),sQuery(id+"F0.wireOp",EDGE,"E1.2.2.2"),sQuery(id+"F0.wireOp",EDGE,"E1.2.2.3"),sQuery(id+"F0.wireOp",EDGE,"E1.2.2.4"),sQuery(id+"F0.wireOp",EDGE,"E2.1.0.0"),sQuery(id+"F0.wireOp",EDGE,"E2.1.0.1"),sQuery(id+"F0.wireOp",EDGE,"E2.1.0.2"),sQuery(id+"F0.wireOp",EDGE,"E2.1.0.3"),sQuery(id+"F0.wireOp",EDGE,"E2.1.0.5"),sQuery(id+"F0.wireOp",EDGE,"E2.1.0.7"),sQuery(id+"F0.wireOp",EDGE,"E2.1.0.12"),sQuery(id+"F0.wireOp",EDGE,"E2.1.0.13"),sQuery(id+"F0.wireOp",EDGE,"E2.1.0.14"),sQuery(id+"F0.wireOp",EDGE,"E2.1.0.15"),sQuery(id+"F0.wireOp",EDGE,"E2.1.0.16"),sQuery(id+"F0.wireOp",EDGE,"E2.1.0.17"),sQuery(id+"F0.wireOp",EDGE,"E2.1.0.18"),sQuery(id+"F0.wireOp",EDGE,"E2.1.0.19"),sQuery(id+"F0.wireOp",EDGE,"E2.1.0.20"),sQuery(id+"F0.wireOp",EDGE,"E2.1.0.21"),sQuery(id+"F0.wireOp",EDGE,"E2.1.0.22"),sQuery(id+"F0.wireOp",EDGE,"E2.1.0.23"),sQuery(id+"F0.wireOp",EDGE,"E2.1.0.25"),sQuery(id+"F0.wireOp",EDGE,"E2.1.0.27"),sQuery(id+"F0.wireOp",EDGE,"E2.1.0.28"),sQuery(id+"F0.wireOp",EDGE,"E2.1.0.30"),sQuery(id+"F0.wireOp",EDGE,"E2.1.0.32"),sQuery(id+"F0.wireOp",EDGE,"E2.1.0.33"),sQuery(id+"F0.wireOp",EDGE,"E2.1.0.34"),sQuery(id+"F0.wireOp",EDGE,"E2.1.0.35"),sQuery(id+"F0.wireOp",EDGE,"E2.1.0.36"),sQuery(id+"F0.wireOp",EDGE,"E2.1.0.37"),sQuery(id+"F0.wireOp",EDGE,"E2.1.0.38"),sQuery(id+"F0.wireOp",EDGE,"E2.1.0.40"),sQuery(id+"F0.wireOp",EDGE,"E2.1.0.41"),sQuery(id+"F0.wireOp",EDGE,"E2.1.0.42"),sQuery(id+"F0.wireOp",EDGE,"E2.1.0.43"),sQuery(id+"F0.wireOp",EDGE,"E2.1.0.44"),sQuery(id+"F0.wireOp",EDGE,"E2.1.0.45"),sQuery(id+"F0.wireOp",EDGE,"E2.1.0.46"),sQuery(id+"F0.wireOp",EDGE,"E3.0.1.1"),sQuery(id+"F0.wireOp",EDGE,"E3.0.1.2"),sQuery(id+"F0.wireOp",EDGE,"E3.0.1.3"),sQuery(id+"F0.wireOp",EDGE,"E3.0.1.4"),sQuery(id+"F0.wireOp",EDGE,"E3.0.1.5"),sQuery(id+"F0.wireOp",EDGE,"E3.0.1.6"),sQuery(id+"F0.wireOp",EDGE,"E3.0.1.7"),sQuery(id+"F0.wireOp",EDGE,"E3.0.1.8"),sQuery(id+"F0.wireOp",EDGE,"E3.0.1.9"),sQuery(id+"F0.wireOp",EDGE,"E3.0.1.10"),sQuery(id+"F0.wireOp",EDGE,"E3.0.1.11"),sQuery(id+"F0.wireOp",EDGE,"E3.0.1.12"),sQuery(id+"F0.wireOp",EDGE,"E3.0.1.14"),sQuery(id+"F0.wireOp",EDGE,"E3.0.1.15"),sQuery(id+"F0.wireOp",EDGE,"E3.0.1.16"),sQuery(id+"F0.wireOp",EDGE,"E3.0.1.17"),sQuery(id+"F0.wireOp",EDGE,"E3.0.1.20"),sQuery(id+"F0.wireOp",EDGE,"E3.0.1.24"),sQuery(id+"F0.wireOp",EDGE,"E3.0.1.26"),sQuery(id+"F0.wireOp",EDGE,"E3.0.1.27"),sQuery(id+"F0.wireOp",EDGE,"E3.0.1.28"),sQuery(id+"F0.wireOp",EDGE,"E3.0.1.29"),sQuery(id+"F0.wireOp",EDGE,"E3.0.1.30"),sQuery(id+"F0.wireOp",EDGE,"E3.0.1.32"),sQuery(id+"F0.wireOp",EDGE,"E4.bottom"),subQ1,subQ0,sQuery(id+"F0.wireOp",EDGE,"E4.right"),sQuery(id+"F0.wireOp",EDGE,"E9.left"),sQuery(id+"F0.wireOp",EDGE,"E9.right"),sQuery(id+"F0.wireOp",EDGE,"E13.bottom"),sQuery(id+"F0.wireOp",EDGE,"E13.top"),sQuery(id+"F0.wireOp",EDGE,"E13.left"),sQuery(id+"F0.wireOp",EDGE,"E13.right"),sQuery(id+"F0.wireOp",EDGE,"E14.bottom"),sQuery(id+"F0.wireOp",EDGE,"E14.top"),sQuery(id+"F0.wireOp",EDGE,"E14.left"),sQuery(id+"F0.wireOp",EDGE,"E14.right"),sQuery(id+"F0.wireOp",EDGE,"E15.left"),sQuery(id+"F0.wireOp",EDGE,"E15.right"),sQuery(id+"F0.wireOp",EDGE,"E20.bottom"),sQuery(id+"F0.wireOp",EDGE,"E20.top"),sQuery(id+"F0.wireOp",EDGE,"E20.left"),sQuery(id+"F0.wireOp",EDGE,"E20.right"),sQuery(id+"F0.wireOp",EDGE,"E21.bottom"),sQuery(id+"F0.wireOp",EDGE,"E21.top"),sQuery(id+"F0.wireOp",EDGE,"E21.left"),sQuery(id+"F0.wireOp",EDGE,"E21.right"),sQuery(id+"F0.wireOp",EDGE,"E22.bottom"),sQuery(id+"F0.wireOp",EDGE,"E22.top"),sQuery(id+"F0.wireOp",EDGE,"E22.left"),sQuery(id+"F0.wireOp",EDGE,"E23.bottom"),sQuery(id+"F0.wireOp",EDGE,"E23.top"),sQuery(id+"F0.wireOp",EDGE,"E23.right"),sQuery(id+"F0.wireOp",EDGE,"E24.bottom"),sQuery(id+"F0.wireOp",EDGE,"E24.top"),sQuery(id+"F0.wireOp",EDGE,"E24.right"),sQuery(id+"F0.wireOp",EDGE,"E25.bottom"),sQuery(id+"F0.wireOp",EDGE,"E25.top"),sQuery(id+"F0.wireOp",EDGE,"E25.right"),sQuery(id+"F0.wireOp",EDGE,"E26.bottom"),sQuery(id+"F0.wireOp",EDGE,"E26.top"),sQuery(id+"F0.wireOp",EDGE,"E26.right"),sQuery(id+"F0.wireOp",EDGE,"E31.bottom"),sQuery(id+"F0.wireOp",EDGE,"E31.top"),sQuery(id+"F0.wireOp",EDGE,"E31.right")])],"isStart":false})],"blendedInto":[makeQuery(id+"F1.opExtrude","CAP_FACE",FACE,{"disambiguationData":[OSD([sQuery(id+"F0.wireOp",EDGE,"E0.bottom"),sQuery(id+"F0.wireOp",EDGE,"E0.top"),sQuery(id+"F0.wireOp",EDGE,"E0.left"),sQuery(id+"F0.wireOp",EDGE,"E0.right"),sQuery(id+"F0.wireOp",EDGE,"E1.0.1.1"),sQuery(id+"F0.wireOp",EDGE,"E1.0.1.2"),sQuery(id+"F0.wireOp",EDGE,"E1.0.1.3"),sQuery(id+"F0.wireOp",EDGE,"E1.0.1.4"),sQuery(id+"F0.wireOp",EDGE,"E1.0.2.1"),sQuery(id+"F0.wireOp",EDGE,"E1.0.2.2"),sQuery(id+"F0.wireOp",EDGE,"E1.0.2.3"),sQuery(id+"F0.wireOp",EDGE,"E1.0.2.4"),sQuery(id+"F0.wireOp",EDGE,"E1.1.0.1"),sQuery(id+"F0.wireOp",EDGE,"E1.1.0.2"),sQuery(id+"F0.wireOp",EDGE,"E1.1.0.3"),sQuery(id+"F0.wireOp",EDGE,"E1.1.0.4"),sQuery(id+"F0.wireOp",EDGE,"E1.1.1.1"),sQuery(id+"F0.wireOp",EDGE,"E1.1.1.2"),sQuery(id+"F0.wireOp",EDGE,"E1.1.1.3"),sQuery(id+"F0.wireOp",EDGE,"E1.1.1.4"),sQuery(id+"F0.wireOp",EDGE,"E1.1.2.1"),sQuery(id+"F0.wireOp",EDGE,"E1.1.2.2"),sQuery(id+"F0.wireOp",EDGE,"E1.1.2.3"),sQuery(id+"F0.wireOp",EDGE,"E1.1.2.4"),sQuery(id+"F0.wireOp",EDGE,"E1.2.0.1"),sQuery(id+"F0.wireOp",EDGE,"E1.2.0.2"),sQuery(id+"F0.wireOp",EDGE,"E1.2.0.3"),sQuery(id+"F0.wireOp",EDGE,"E1.2.0.4"),sQuery(id+"F0.wireOp",EDGE,"E1.2.1.1"),sQuery(id+"F0.wireOp",EDGE,"E1.2.1.2"),sQuery(id+"F0.wireOp",EDGE,"E1.2.1.3"),sQuery(id+"F0.wireOp",EDGE,"E1.2.1.4"),sQuery(id+"F0.wireOp",EDGE,"E1.2.2.1"),sQuery(id+"F0.wireOp",EDGE,"E1.2.2.2"),sQuery(id+"F0.wireOp",EDGE,"E1.2.2.3"),sQuery(id+"F0.wireOp",EDGE,"E1.2.2.4"),sQuery(id+"F0.wireOp",EDGE,"E2.1.0.0"),sQuery(id+"F0.wireOp",EDGE,"E2.1.0.1"),sQuery(id+"F0.wireOp",EDGE,"E2.1.0.2"),sQuery(id+"F0.wireOp",EDGE,"E2.1.0.3"),sQuery(id+"F0.wireOp",EDGE,"E2.1.0.5"),sQuery(id+"F0.wireOp",EDGE,"E2.1.0.7"),sQuery(id+"F0.wireOp",EDGE,"E2.1.0.12"),sQuery(id+"F0.wireOp",EDGE,"E2.1.0.13"),sQuery(id+"F0.wireOp",EDGE,"E2.1.0.14"),sQuery(id+"F0.wireOp",EDGE,"E2.1.0.15"),sQuery(id+"F0.wireOp",EDGE,"E2.1.0.16"),sQuery(id+"F0.wireOp",EDGE,"E2.1.0.17"),sQuery(id+"F0.wireOp",EDGE,"E2.1.0.18"),sQuery(id+"F0.wireOp",EDGE,"E2.1.0.19"),sQuery(id+"F0.wireOp",EDGE,"E2.1.0.20"),sQuery(id+"F0.wireOp",EDGE,"E2.1.0.21"),sQuery(id+"F0.wireOp",EDGE,"E2.1.0.22"),sQuery(id+"F0.wireOp",EDGE,"E2.1.0.23"),sQuery(id+"F0.wireOp",EDGE,"E2.1.0.25"),sQuery(id+"F0.wireOp",EDGE,"E2.1.0.27"),sQuery(id+"F0.wireOp",EDGE,"E2.1.0.28"),sQuery(id+"F0.wireOp",EDGE,"E2.1.0.30"),sQuery(id+"F0.wireOp",EDGE,"E2.1.0.32"),sQuery(id+"F0.wireOp",EDGE,"E2.1.0.33"),sQuery(id+"F0.wireOp",EDGE,"E2.1.0.34"),sQuery(id+"F0.wireOp",EDGE,"E2.1.0.35"),sQuery(id+"F0.wireOp",EDGE,"E2.1.0.36"),sQuery(id+"F0.wireOp",EDGE,"E2.1.0.37"),sQuery(id+"F0.wireOp",EDGE,"E2.1.0.38"),sQuery(id+"F0.wireOp",EDGE,"E2.1.0.40"),sQuery(id+"F0.wireOp",EDGE,"E2.1.0.41"),sQuery(id+"F0.wireOp",EDGE,"E2.1.0.42"),sQuery(id+"F0.wireOp",EDGE,"E2.1.0.43"),sQuery(id+"F0.wireOp",EDGE,"E2.1.0.44"),sQuery(id+"F0.wireOp",EDGE,"E2.1.0.45"),sQuery(id+"F0.wireOp",EDGE,"E2.1.0.46"),sQuery(id+"F0.wireOp",EDGE,"E3.0.1.1"),sQuery(id+"F0.wireOp",EDGE,"E3.0.1.2"),sQuery(id+"F0.wireOp",EDGE,"E3.0.1.3"),sQuery(id+"F0.wireOp",EDGE,"E3.0.1.4"),sQuery(id+"F0.wireOp",EDGE,"E3.0.1.5"),sQuery(id+"F0.wireOp",EDGE,"E3.0.1.6"),sQuery(id+"F0.wireOp",EDGE,"E3.0.1.7"),sQuery(id+"F0.wireOp",EDGE,"E3.0.1.8"),sQuery(id+"F0.wireOp",EDGE,"E3.0.1.9"),sQuery(id+"F0.wireOp",EDGE,"E3.0.1.10"),sQuery(id+"F0.wireOp",EDGE,"E3.0.1.11"),sQuery(id+"F0.wireOp",EDGE,"E3.0.1.12"),sQuery(id+"F0.wireOp",EDGE,"E3.0.1.14"),sQuery(id+"F0.wireOp",EDGE,"E3.0.1.15"),sQuery(id+"F0.wireOp",EDGE,"E3.0.1.16"),sQuery(id+"F0.wireOp",EDGE,"E3.0.1.17"),sQuery(id+"F0.wireOp",EDGE,"E3.0.1.20"),sQuery(id+"F0.wireOp",EDGE,"E3.0.1.24"),sQuery(id+"F0.wireOp",EDGE,"E3.0.1.26"),sQuery(id+"F0.wireOp",EDGE,"E3.0.1.27"),sQuery(id+"F0.wireOp",EDGE,"E3.0.1.28"),sQuery(id+"F0.wireOp",EDGE,"E3.0.1.29"),sQuery(id+"F0.wireOp",EDGE,"E3.0.1.30"),sQuery(id+"F0.wireOp",EDGE,"E3.0.1.32"),sQuery(id+"F0.wireOp",EDGE,"E4.bottom"),subQ1,subQ0,sQuery(id+"F0.wireOp",EDGE,"E4.right"),sQuery(id+"F0.wireOp",EDGE,"E9.left"),sQuery(id+"F0.wireOp",EDGE,"E9.right"),sQuery(id+"F0.wireOp",EDGE,"E13.bottom"),sQuery(id+"F0.wireOp",EDGE,"E13.top"),sQuery(id+"F0.wireOp",EDGE,"E13.left"),sQuery(id+"F0.wireOp",EDGE,"E13.right"),sQuery(id+"F0.wireOp",EDGE,"E14.bottom"),sQuery(id+"F0.wireOp",EDGE,"E14.top"),sQuery(id+"F0.wireOp",EDGE,"E14.left"),sQuery(id+"F0.wireOp",EDGE,"E14.right"),sQuery(id+"F0.wireOp",EDGE,"E15.left"),sQuery(id+"F0.wireOp",EDGE,"E15.right"),sQuery(id+"F0.wireOp",EDGE,"E20.bottom"),sQuery(id+"F0.wireOp",EDGE,"E20.top"),sQuery(id+"F0.wireOp",EDGE,"E20.left"),sQuery(id+"F0.wireOp",EDGE,"E20.right"),sQuery(id+"F0.wireOp",EDGE,"E21.bottom"),sQuery(id+"F0.wireOp",EDGE,"E21.top"),sQuery(id+"F0.wireOp",EDGE,"E21.left"),sQuery(id+"F0.wireOp",EDGE,"E21.right"),sQuery(id+"F0.wireOp",EDGE,"E22.bottom"),sQuery(id+"F0.wireOp",EDGE,"E22.top"),sQuery(id+"F0.wireOp",EDGE,"E22.left"),sQuery(id+"F0.wireOp",EDGE,"E23.bottom"),sQuery(id+"F0.wireOp",EDGE,"E23.top"),sQuery(id+"F0.wireOp",EDGE,"E23.right"),sQuery(id+"F0.wireOp",EDGE,"E24.bottom"),sQuery(id+"F0.wireOp",EDGE,"E24.top"),sQuery(id+"F0.wireOp",EDGE,"E24.right"),sQuery(id+"F0.wireOp",EDGE,"E25.bottom"),sQuery(id+"F0.wireOp",EDGE,"E25.top"),sQuery(id+"F0.wireOp",EDGE,"E25.right"),sQuery(id+"F0.wireOp",EDGE,"E26.bottom"),sQuery(id+"F0.wireOp",EDGE,"E26.top"),sQuery(id+"F0.wireOp",EDGE,"E26.right"),sQuery(id+"F0.wireOp",EDGE,"E31.bottom"),sQuery(id+"F0.wireOp",EDGE,"E31.top"),sQuery(id+"F0.wireOp",EDGE,"E31.right")])],"isStart":false})]});}
            var Q16;
            {var subQ0=sQuery(id+"F0.wireOp",EDGE,"E4.top");Q16=makeQuery(id+"F3.opFillet","BLEND_EDGE",EDGE,{"blendedFrom":[makeQuery(id+"F1.opExtrude","SWEPT_EDGE",EDGE,{"disambiguationData":[OSD([subQ0,sQuery(id+"F0.wireOp",EDGE,"E4.left")])]}),makeQuery(id+"F1.opExtrude","SWEPT_FACE",FACE,{"disambiguationData":[OSD([subQ0])]})],"blendedInto":[makeQuery(id+"F1.opExtrude","SWEPT_FACE",FACE,{"disambiguationData":[OSD([subQ0])]})]});}
            var Q17;
            {var subQ0=sQuery(id+"F0.wireOp",EDGE,"E4.left");var subQ1=sQuery(id+"F0.wireOp",EDGE,"E4.top");Q17=makeQuery(id+"F3.opFillet","BLEND_EDGE",EDGE,{"blendedFrom":[makeQuery(id+"F1.opExtrude","SWEPT_EDGE",EDGE,{"disambiguationData":[OSD([subQ1,subQ0])]}),makeQuery(id+"F1.opExtrude","CAP_FACE",FACE,{"disambiguationData":[OSD([sQuery(id+"F0.wireOp",EDGE,"E0.bottom"),sQuery(id+"F0.wireOp",EDGE,"E0.top"),sQuery(id+"F0.wireOp",EDGE,"E0.left"),sQuery(id+"F0.wireOp",EDGE,"E0.right"),sQuery(id+"F0.wireOp",EDGE,"E1.0.1.1"),sQuery(id+"F0.wireOp",EDGE,"E1.0.1.2"),sQuery(id+"F0.wireOp",EDGE,"E1.0.1.3"),sQuery(id+"F0.wireOp",EDGE,"E1.0.1.4"),sQuery(id+"F0.wireOp",EDGE,"E1.0.2.1"),sQuery(id+"F0.wireOp",EDGE,"E1.0.2.2"),sQuery(id+"F0.wireOp",EDGE,"E1.0.2.3"),sQuery(id+"F0.wireOp",EDGE,"E1.0.2.4"),sQuery(id+"F0.wireOp",EDGE,"E1.1.0.1"),sQuery(id+"F0.wireOp",EDGE,"E1.1.0.2"),sQuery(id+"F0.wireOp",EDGE,"E1.1.0.3"),sQuery(id+"F0.wireOp",EDGE,"E1.1.0.4"),sQuery(id+"F0.wireOp",EDGE,"E1.1.1.1"),sQuery(id+"F0.wireOp",EDGE,"E1.1.1.2"),sQuery(id+"F0.wireOp",EDGE,"E1.1.1.3"),sQuery(id+"F0.wireOp",EDGE,"E1.1.1.4"),sQuery(id+"F0.wireOp",EDGE,"E1.1.2.1"),sQuery(id+"F0.wireOp",EDGE,"E1.1.2.2"),sQuery(id+"F0.wireOp",EDGE,"E1.1.2.3"),sQuery(id+"F0.wireOp",EDGE,"E1.1.2.4"),sQuery(id+"F0.wireOp",EDGE,"E1.2.0.1"),sQuery(id+"F0.wireOp",EDGE,"E1.2.0.2"),sQuery(id+"F0.wireOp",EDGE,"E1.2.0.3"),sQuery(id+"F0.wireOp",EDGE,"E1.2.0.4"),sQuery(id+"F0.wireOp",EDGE,"E1.2.1.1"),sQuery(id+"F0.wireOp",EDGE,"E1.2.1.2"),sQuery(id+"F0.wireOp",EDGE,"E1.2.1.3"),sQuery(id+"F0.wireOp",EDGE,"E1.2.1.4"),sQuery(id+"F0.wireOp",EDGE,"E1.2.2.1"),sQuery(id+"F0.wireOp",EDGE,"E1.2.2.2"),sQuery(id+"F0.wireOp",EDGE,"E1.2.2.3"),sQuery(id+"F0.wireOp",EDGE,"E1.2.2.4"),sQuery(id+"F0.wireOp",EDGE,"E2.1.0.0"),sQuery(id+"F0.wireOp",EDGE,"E2.1.0.1"),sQuery(id+"F0.wireOp",EDGE,"E2.1.0.2"),sQuery(id+"F0.wireOp",EDGE,"E2.1.0.3"),sQuery(id+"F0.wireOp",EDGE,"E2.1.0.5"),sQuery(id+"F0.wireOp",EDGE,"E2.1.0.7"),sQuery(id+"F0.wireOp",EDGE,"E2.1.0.12"),sQuery(id+"F0.wireOp",EDGE,"E2.1.0.13"),sQuery(id+"F0.wireOp",EDGE,"E2.1.0.14"),sQuery(id+"F0.wireOp",EDGE,"E2.1.0.15"),sQuery(id+"F0.wireOp",EDGE,"E2.1.0.16"),sQuery(id+"F0.wireOp",EDGE,"E2.1.0.17"),sQuery(id+"F0.wireOp",EDGE,"E2.1.0.18"),sQuery(id+"F0.wireOp",EDGE,"E2.1.0.19"),sQuery(id+"F0.wireOp",EDGE,"E2.1.0.20"),sQuery(id+"F0.wireOp",EDGE,"E2.1.0.21"),sQuery(id+"F0.wireOp",EDGE,"E2.1.0.22"),sQuery(id+"F0.wireOp",EDGE,"E2.1.0.23"),sQuery(id+"F0.wireOp",EDGE,"E2.1.0.25"),sQuery(id+"F0.wireOp",EDGE,"E2.1.0.27"),sQuery(id+"F0.wireOp",EDGE,"E2.1.0.28"),sQuery(id+"F0.wireOp",EDGE,"E2.1.0.30"),sQuery(id+"F0.wireOp",EDGE,"E2.1.0.32"),sQuery(id+"F0.wireOp",EDGE,"E2.1.0.33"),sQuery(id+"F0.wireOp",EDGE,"E2.1.0.34"),sQuery(id+"F0.wireOp",EDGE,"E2.1.0.35"),sQuery(id+"F0.wireOp",EDGE,"E2.1.0.36"),sQuery(id+"F0.wireOp",EDGE,"E2.1.0.37"),sQuery(id+"F0.wireOp",EDGE,"E2.1.0.38"),sQuery(id+"F0.wireOp",EDGE,"E2.1.0.40"),sQuery(id+"F0.wireOp",EDGE,"E2.1.0.41"),sQuery(id+"F0.wireOp",EDGE,"E2.1.0.42"),sQuery(id+"F0.wireOp",EDGE,"E2.1.0.43"),sQuery(id+"F0.wireOp",EDGE,"E2.1.0.44"),sQuery(id+"F0.wireOp",EDGE,"E2.1.0.45"),sQuery(id+"F0.wireOp",EDGE,"E2.1.0.46"),sQuery(id+"F0.wireOp",EDGE,"E3.0.1.1"),sQuery(id+"F0.wireOp",EDGE,"E3.0.1.2"),sQuery(id+"F0.wireOp",EDGE,"E3.0.1.3"),sQuery(id+"F0.wireOp",EDGE,"E3.0.1.4"),sQuery(id+"F0.wireOp",EDGE,"E3.0.1.5"),sQuery(id+"F0.wireOp",EDGE,"E3.0.1.6"),sQuery(id+"F0.wireOp",EDGE,"E3.0.1.7"),sQuery(id+"F0.wireOp",EDGE,"E3.0.1.8"),sQuery(id+"F0.wireOp",EDGE,"E3.0.1.9"),sQuery(id+"F0.wireOp",EDGE,"E3.0.1.10"),sQuery(id+"F0.wireOp",EDGE,"E3.0.1.11"),sQuery(id+"F0.wireOp",EDGE,"E3.0.1.12"),sQuery(id+"F0.wireOp",EDGE,"E3.0.1.14"),sQuery(id+"F0.wireOp",EDGE,"E3.0.1.15"),sQuery(id+"F0.wireOp",EDGE,"E3.0.1.16"),sQuery(id+"F0.wireOp",EDGE,"E3.0.1.17"),sQuery(id+"F0.wireOp",EDGE,"E3.0.1.20"),sQuery(id+"F0.wireOp",EDGE,"E3.0.1.24"),sQuery(id+"F0.wireOp",EDGE,"E3.0.1.26"),sQuery(id+"F0.wireOp",EDGE,"E3.0.1.27"),sQuery(id+"F0.wireOp",EDGE,"E3.0.1.28"),sQuery(id+"F0.wireOp",EDGE,"E3.0.1.29"),sQuery(id+"F0.wireOp",EDGE,"E3.0.1.30"),sQuery(id+"F0.wireOp",EDGE,"E3.0.1.32"),sQuery(id+"F0.wireOp",EDGE,"E4.bottom"),subQ1,subQ0,sQuery(id+"F0.wireOp",EDGE,"E4.right"),sQuery(id+"F0.wireOp",EDGE,"E9.left"),sQuery(id+"F0.wireOp",EDGE,"E9.right"),sQuery(id+"F0.wireOp",EDGE,"E13.bottom"),sQuery(id+"F0.wireOp",EDGE,"E13.top"),sQuery(id+"F0.wireOp",EDGE,"E13.left"),sQuery(id+"F0.wireOp",EDGE,"E13.right"),sQuery(id+"F0.wireOp",EDGE,"E14.bottom"),sQuery(id+"F0.wireOp",EDGE,"E14.top"),sQuery(id+"F0.wireOp",EDGE,"E14.left"),sQuery(id+"F0.wireOp",EDGE,"E14.right"),sQuery(id+"F0.wireOp",EDGE,"E15.left"),sQuery(id+"F0.wireOp",EDGE,"E15.right"),sQuery(id+"F0.wireOp",EDGE,"E20.bottom"),sQuery(id+"F0.wireOp",EDGE,"E20.top"),sQuery(id+"F0.wireOp",EDGE,"E20.left"),sQuery(id+"F0.wireOp",EDGE,"E20.right"),sQuery(id+"F0.wireOp",EDGE,"E21.bottom"),sQuery(id+"F0.wireOp",EDGE,"E21.top"),sQuery(id+"F0.wireOp",EDGE,"E21.left"),sQuery(id+"F0.wireOp",EDGE,"E21.right"),sQuery(id+"F0.wireOp",EDGE,"E22.bottom"),sQuery(id+"F0.wireOp",EDGE,"E22.top"),sQuery(id+"F0.wireOp",EDGE,"E22.left"),sQuery(id+"F0.wireOp",EDGE,"E23.bottom"),sQuery(id+"F0.wireOp",EDGE,"E23.top"),sQuery(id+"F0.wireOp",EDGE,"E23.right"),sQuery(id+"F0.wireOp",EDGE,"E24.bottom"),sQuery(id+"F0.wireOp",EDGE,"E24.top"),sQuery(id+"F0.wireOp",EDGE,"E24.right"),sQuery(id+"F0.wireOp",EDGE,"E25.bottom"),sQuery(id+"F0.wireOp",EDGE,"E25.top"),sQuery(id+"F0.wireOp",EDGE,"E25.right"),sQuery(id+"F0.wireOp",EDGE,"E26.bottom"),sQuery(id+"F0.wireOp",EDGE,"E26.top"),sQuery(id+"F0.wireOp",EDGE,"E26.right"),sQuery(id+"F0.wireOp",EDGE,"E31.bottom"),sQuery(id+"F0.wireOp",EDGE,"E31.top"),sQuery(id+"F0.wireOp",EDGE,"E31.right")])],"isStart":true})],"blendedInto":[makeQuery(id+"F1.opExtrude","CAP_FACE",FACE,{"disambiguationData":[OSD([sQuery(id+"F0.wireOp",EDGE,"E0.bottom"),sQuery(id+"F0.wireOp",EDGE,"E0.top"),sQuery(id+"F0.wireOp",EDGE,"E0.left"),sQuery(id+"F0.wireOp",EDGE,"E0.right"),sQuery(id+"F0.wireOp",EDGE,"E1.0.1.1"),sQuery(id+"F0.wireOp",EDGE,"E1.0.1.2"),sQuery(id+"F0.wireOp",EDGE,"E1.0.1.3"),sQuery(id+"F0.wireOp",EDGE,"E1.0.1.4"),sQuery(id+"F0.wireOp",EDGE,"E1.0.2.1"),sQuery(id+"F0.wireOp",EDGE,"E1.0.2.2"),sQuery(id+"F0.wireOp",EDGE,"E1.0.2.3"),sQuery(id+"F0.wireOp",EDGE,"E1.0.2.4"),sQuery(id+"F0.wireOp",EDGE,"E1.1.0.1"),sQuery(id+"F0.wireOp",EDGE,"E1.1.0.2"),sQuery(id+"F0.wireOp",EDGE,"E1.1.0.3"),sQuery(id+"F0.wireOp",EDGE,"E1.1.0.4"),sQuery(id+"F0.wireOp",EDGE,"E1.1.1.1"),sQuery(id+"F0.wireOp",EDGE,"E1.1.1.2"),sQuery(id+"F0.wireOp",EDGE,"E1.1.1.3"),sQuery(id+"F0.wireOp",EDGE,"E1.1.1.4"),sQuery(id+"F0.wireOp",EDGE,"E1.1.2.1"),sQuery(id+"F0.wireOp",EDGE,"E1.1.2.2"),sQuery(id+"F0.wireOp",EDGE,"E1.1.2.3"),sQuery(id+"F0.wireOp",EDGE,"E1.1.2.4"),sQuery(id+"F0.wireOp",EDGE,"E1.2.0.1"),sQuery(id+"F0.wireOp",EDGE,"E1.2.0.2"),sQuery(id+"F0.wireOp",EDGE,"E1.2.0.3"),sQuery(id+"F0.wireOp",EDGE,"E1.2.0.4"),sQuery(id+"F0.wireOp",EDGE,"E1.2.1.1"),sQuery(id+"F0.wireOp",EDGE,"E1.2.1.2"),sQuery(id+"F0.wireOp",EDGE,"E1.2.1.3"),sQuery(id+"F0.wireOp",EDGE,"E1.2.1.4"),sQuery(id+"F0.wireOp",EDGE,"E1.2.2.1"),sQuery(id+"F0.wireOp",EDGE,"E1.2.2.2"),sQuery(id+"F0.wireOp",EDGE,"E1.2.2.3"),sQuery(id+"F0.wireOp",EDGE,"E1.2.2.4"),sQuery(id+"F0.wireOp",EDGE,"E2.1.0.0"),sQuery(id+"F0.wireOp",EDGE,"E2.1.0.1"),sQuery(id+"F0.wireOp",EDGE,"E2.1.0.2"),sQuery(id+"F0.wireOp",EDGE,"E2.1.0.3"),sQuery(id+"F0.wireOp",EDGE,"E2.1.0.5"),sQuery(id+"F0.wireOp",EDGE,"E2.1.0.7"),sQuery(id+"F0.wireOp",EDGE,"E2.1.0.12"),sQuery(id+"F0.wireOp",EDGE,"E2.1.0.13"),sQuery(id+"F0.wireOp",EDGE,"E2.1.0.14"),sQuery(id+"F0.wireOp",EDGE,"E2.1.0.15"),sQuery(id+"F0.wireOp",EDGE,"E2.1.0.16"),sQuery(id+"F0.wireOp",EDGE,"E2.1.0.17"),sQuery(id+"F0.wireOp",EDGE,"E2.1.0.18"),sQuery(id+"F0.wireOp",EDGE,"E2.1.0.19"),sQuery(id+"F0.wireOp",EDGE,"E2.1.0.20"),sQuery(id+"F0.wireOp",EDGE,"E2.1.0.21"),sQuery(id+"F0.wireOp",EDGE,"E2.1.0.22"),sQuery(id+"F0.wireOp",EDGE,"E2.1.0.23"),sQuery(id+"F0.wireOp",EDGE,"E2.1.0.25"),sQuery(id+"F0.wireOp",EDGE,"E2.1.0.27"),sQuery(id+"F0.wireOp",EDGE,"E2.1.0.28"),sQuery(id+"F0.wireOp",EDGE,"E2.1.0.30"),sQuery(id+"F0.wireOp",EDGE,"E2.1.0.32"),sQuery(id+"F0.wireOp",EDGE,"E2.1.0.33"),sQuery(id+"F0.wireOp",EDGE,"E2.1.0.34"),sQuery(id+"F0.wireOp",EDGE,"E2.1.0.35"),sQuery(id+"F0.wireOp",EDGE,"E2.1.0.36"),sQuery(id+"F0.wireOp",EDGE,"E2.1.0.37"),sQuery(id+"F0.wireOp",EDGE,"E2.1.0.38"),sQuery(id+"F0.wireOp",EDGE,"E2.1.0.40"),sQuery(id+"F0.wireOp",EDGE,"E2.1.0.41"),sQuery(id+"F0.wireOp",EDGE,"E2.1.0.42"),sQuery(id+"F0.wireOp",EDGE,"E2.1.0.43"),sQuery(id+"F0.wireOp",EDGE,"E2.1.0.44"),sQuery(id+"F0.wireOp",EDGE,"E2.1.0.45"),sQuery(id+"F0.wireOp",EDGE,"E2.1.0.46"),sQuery(id+"F0.wireOp",EDGE,"E3.0.1.1"),sQuery(id+"F0.wireOp",EDGE,"E3.0.1.2"),sQuery(id+"F0.wireOp",EDGE,"E3.0.1.3"),sQuery(id+"F0.wireOp",EDGE,"E3.0.1.4"),sQuery(id+"F0.wireOp",EDGE,"E3.0.1.5"),sQuery(id+"F0.wireOp",EDGE,"E3.0.1.6"),sQuery(id+"F0.wireOp",EDGE,"E3.0.1.7"),sQuery(id+"F0.wireOp",EDGE,"E3.0.1.8"),sQuery(id+"F0.wireOp",EDGE,"E3.0.1.9"),sQuery(id+"F0.wireOp",EDGE,"E3.0.1.10"),sQuery(id+"F0.wireOp",EDGE,"E3.0.1.11"),sQuery(id+"F0.wireOp",EDGE,"E3.0.1.12"),sQuery(id+"F0.wireOp",EDGE,"E3.0.1.14"),sQuery(id+"F0.wireOp",EDGE,"E3.0.1.15"),sQuery(id+"F0.wireOp",EDGE,"E3.0.1.16"),sQuery(id+"F0.wireOp",EDGE,"E3.0.1.17"),sQuery(id+"F0.wireOp",EDGE,"E3.0.1.20"),sQuery(id+"F0.wireOp",EDGE,"E3.0.1.24"),sQuery(id+"F0.wireOp",EDGE,"E3.0.1.26"),sQuery(id+"F0.wireOp",EDGE,"E3.0.1.27"),sQuery(id+"F0.wireOp",EDGE,"E3.0.1.28"),sQuery(id+"F0.wireOp",EDGE,"E3.0.1.29"),sQuery(id+"F0.wireOp",EDGE,"E3.0.1.30"),sQuery(id+"F0.wireOp",EDGE,"E3.0.1.32"),sQuery(id+"F0.wireOp",EDGE,"E4.bottom"),subQ1,subQ0,sQuery(id+"F0.wireOp",EDGE,"E4.right"),sQuery(id+"F0.wireOp",EDGE,"E9.left"),sQuery(id+"F0.wireOp",EDGE,"E9.right"),sQuery(id+"F0.wireOp",EDGE,"E13.bottom"),sQuery(id+"F0.wireOp",EDGE,"E13.top"),sQuery(id+"F0.wireOp",EDGE,"E13.left"),sQuery(id+"F0.wireOp",EDGE,"E13.right"),sQuery(id+"F0.wireOp",EDGE,"E14.bottom"),sQuery(id+"F0.wireOp",EDGE,"E14.top"),sQuery(id+"F0.wireOp",EDGE,"E14.left"),sQuery(id+"F0.wireOp",EDGE,"E14.right"),sQuery(id+"F0.wireOp",EDGE,"E15.left"),sQuery(id+"F0.wireOp",EDGE,"E15.right"),sQuery(id+"F0.wireOp",EDGE,"E20.bottom"),sQuery(id+"F0.wireOp",EDGE,"E20.top"),sQuery(id+"F0.wireOp",EDGE,"E20.left"),sQuery(id+"F0.wireOp",EDGE,"E20.right"),sQuery(id+"F0.wireOp",EDGE,"E21.bottom"),sQuery(id+"F0.wireOp",EDGE,"E21.top"),sQuery(id+"F0.wireOp",EDGE,"E21.left"),sQuery(id+"F0.wireOp",EDGE,"E21.right"),sQuery(id+"F0.wireOp",EDGE,"E22.bottom"),sQuery(id+"F0.wireOp",EDGE,"E22.top"),sQuery(id+"F0.wireOp",EDGE,"E22.left"),sQuery(id+"F0.wireOp",EDGE,"E23.bottom"),sQuery(id+"F0.wireOp",EDGE,"E23.top"),sQuery(id+"F0.wireOp",EDGE,"E23.right"),sQuery(id+"F0.wireOp",EDGE,"E24.bottom"),sQuery(id+"F0.wireOp",EDGE,"E24.top"),sQuery(id+"F0.wireOp",EDGE,"E24.right"),sQuery(id+"F0.wireOp",EDGE,"E25.bottom"),sQuery(id+"F0.wireOp",EDGE,"E25.top"),sQuery(id+"F0.wireOp",EDGE,"E25.right"),sQuery(id+"F0.wireOp",EDGE,"E26.bottom"),sQuery(id+"F0.wireOp",EDGE,"E26.top"),sQuery(id+"F0.wireOp",EDGE,"E26.right"),sQuery(id+"F0.wireOp",EDGE,"E31.bottom"),sQuery(id+"F0.wireOp",EDGE,"E31.top"),sQuery(id+"F0.wireOp",EDGE,"E31.right")])],"isStart":true})]});}
            var Q18;
            Q18=makeQuery(id+"F1.opExtrude","CAP_EDGE",EDGE,{"disambiguationData":[OSD([sQuery(id+"F0.wireOp",EDGE,"E4.left")])],"isStart":false});
            var Q19;
            {var subQ0=sQuery(id+"F0.wireOp",EDGE,"E4.left");var subQ1=sQuery(id+"F0.wireOp",EDGE,"E4.bottom");Q19=makeQuery(id+"F2.opFillet","BLEND_EDGE",EDGE,{"blendedFrom":[makeQuery(id+"F1.opExtrude","SWEPT_EDGE",EDGE,{"disambiguationData":[OSD([subQ1,subQ0])]}),makeQuery(id+"F1.opExtrude","CAP_FACE",FACE,{"disambiguationData":[OSD([sQuery(id+"F0.wireOp",EDGE,"E0.bottom"),sQuery(id+"F0.wireOp",EDGE,"E0.top"),sQuery(id+"F0.wireOp",EDGE,"E0.left"),sQuery(id+"F0.wireOp",EDGE,"E0.right"),sQuery(id+"F0.wireOp",EDGE,"E1.0.1.1"),sQuery(id+"F0.wireOp",EDGE,"E1.0.1.2"),sQuery(id+"F0.wireOp",EDGE,"E1.0.1.3"),sQuery(id+"F0.wireOp",EDGE,"E1.0.1.4"),sQuery(id+"F0.wireOp",EDGE,"E1.0.2.1"),sQuery(id+"F0.wireOp",EDGE,"E1.0.2.2"),sQuery(id+"F0.wireOp",EDGE,"E1.0.2.3"),sQuery(id+"F0.wireOp",EDGE,"E1.0.2.4"),sQuery(id+"F0.wireOp",EDGE,"E1.1.0.1"),sQuery(id+"F0.wireOp",EDGE,"E1.1.0.2"),sQuery(id+"F0.wireOp",EDGE,"E1.1.0.3"),sQuery(id+"F0.wireOp",EDGE,"E1.1.0.4"),sQuery(id+"F0.wireOp",EDGE,"E1.1.1.1"),sQuery(id+"F0.wireOp",EDGE,"E1.1.1.2"),sQuery(id+"F0.wireOp",EDGE,"E1.1.1.3"),sQuery(id+"F0.wireOp",EDGE,"E1.1.1.4"),sQuery(id+"F0.wireOp",EDGE,"E1.1.2.1"),sQuery(id+"F0.wireOp",EDGE,"E1.1.2.2"),sQuery(id+"F0.wireOp",EDGE,"E1.1.2.3"),sQuery(id+"F0.wireOp",EDGE,"E1.1.2.4"),sQuery(id+"F0.wireOp",EDGE,"E1.2.0.1"),sQuery(id+"F0.wireOp",EDGE,"E1.2.0.2"),sQuery(id+"F0.wireOp",EDGE,"E1.2.0.3"),sQuery(id+"F0.wireOp",EDGE,"E1.2.0.4"),sQuery(id+"F0.wireOp",EDGE,"E1.2.1.1"),sQuery(id+"F0.wireOp",EDGE,"E1.2.1.2"),sQuery(id+"F0.wireOp",EDGE,"E1.2.1.3"),sQuery(id+"F0.wireOp",EDGE,"E1.2.1.4"),sQuery(id+"F0.wireOp",EDGE,"E1.2.2.1"),sQuery(id+"F0.wireOp",EDGE,"E1.2.2.2"),sQuery(id+"F0.wireOp",EDGE,"E1.2.2.3"),sQuery(id+"F0.wireOp",EDGE,"E1.2.2.4"),sQuery(id+"F0.wireOp",EDGE,"E2.1.0.0"),sQuery(id+"F0.wireOp",EDGE,"E2.1.0.1"),sQuery(id+"F0.wireOp",EDGE,"E2.1.0.2"),sQuery(id+"F0.wireOp",EDGE,"E2.1.0.3"),sQuery(id+"F0.wireOp",EDGE,"E2.1.0.5"),sQuery(id+"F0.wireOp",EDGE,"E2.1.0.7"),sQuery(id+"F0.wireOp",EDGE,"E2.1.0.12"),sQuery(id+"F0.wireOp",EDGE,"E2.1.0.13"),sQuery(id+"F0.wireOp",EDGE,"E2.1.0.14"),sQuery(id+"F0.wireOp",EDGE,"E2.1.0.15"),sQuery(id+"F0.wireOp",EDGE,"E2.1.0.16"),sQuery(id+"F0.wireOp",EDGE,"E2.1.0.17"),sQuery(id+"F0.wireOp",EDGE,"E2.1.0.18"),sQuery(id+"F0.wireOp",EDGE,"E2.1.0.19"),sQuery(id+"F0.wireOp",EDGE,"E2.1.0.20"),sQuery(id+"F0.wireOp",EDGE,"E2.1.0.21"),sQuery(id+"F0.wireOp",EDGE,"E2.1.0.22"),sQuery(id+"F0.wireOp",EDGE,"E2.1.0.23"),sQuery(id+"F0.wireOp",EDGE,"E2.1.0.25"),sQuery(id+"F0.wireOp",EDGE,"E2.1.0.27"),sQuery(id+"F0.wireOp",EDGE,"E2.1.0.28"),sQuery(id+"F0.wireOp",EDGE,"E2.1.0.30"),sQuery(id+"F0.wireOp",EDGE,"E2.1.0.32"),sQuery(id+"F0.wireOp",EDGE,"E2.1.0.33"),sQuery(id+"F0.wireOp",EDGE,"E2.1.0.34"),sQuery(id+"F0.wireOp",EDGE,"E2.1.0.35"),sQuery(id+"F0.wireOp",EDGE,"E2.1.0.36"),sQuery(id+"F0.wireOp",EDGE,"E2.1.0.37"),sQuery(id+"F0.wireOp",EDGE,"E2.1.0.38"),sQuery(id+"F0.wireOp",EDGE,"E2.1.0.40"),sQuery(id+"F0.wireOp",EDGE,"E2.1.0.41"),sQuery(id+"F0.wireOp",EDGE,"E2.1.0.42"),sQuery(id+"F0.wireOp",EDGE,"E2.1.0.43"),sQuery(id+"F0.wireOp",EDGE,"E2.1.0.44"),sQuery(id+"F0.wireOp",EDGE,"E2.1.0.45"),sQuery(id+"F0.wireOp",EDGE,"E2.1.0.46"),sQuery(id+"F0.wireOp",EDGE,"E3.0.1.1"),sQuery(id+"F0.wireOp",EDGE,"E3.0.1.2"),sQuery(id+"F0.wireOp",EDGE,"E3.0.1.3"),sQuery(id+"F0.wireOp",EDGE,"E3.0.1.4"),sQuery(id+"F0.wireOp",EDGE,"E3.0.1.5"),sQuery(id+"F0.wireOp",EDGE,"E3.0.1.6"),sQuery(id+"F0.wireOp",EDGE,"E3.0.1.7"),sQuery(id+"F0.wireOp",EDGE,"E3.0.1.8"),sQuery(id+"F0.wireOp",EDGE,"E3.0.1.9"),sQuery(id+"F0.wireOp",EDGE,"E3.0.1.10"),sQuery(id+"F0.wireOp",EDGE,"E3.0.1.11"),sQuery(id+"F0.wireOp",EDGE,"E3.0.1.12"),sQuery(id+"F0.wireOp",EDGE,"E3.0.1.14"),sQuery(id+"F0.wireOp",EDGE,"E3.0.1.15"),sQuery(id+"F0.wireOp",EDGE,"E3.0.1.16"),sQuery(id+"F0.wireOp",EDGE,"E3.0.1.17"),sQuery(id+"F0.wireOp",EDGE,"E3.0.1.20"),sQuery(id+"F0.wireOp",EDGE,"E3.0.1.24"),sQuery(id+"F0.wireOp",EDGE,"E3.0.1.26"),sQuery(id+"F0.wireOp",EDGE,"E3.0.1.27"),sQuery(id+"F0.wireOp",EDGE,"E3.0.1.28"),sQuery(id+"F0.wireOp",EDGE,"E3.0.1.29"),sQuery(id+"F0.wireOp",EDGE,"E3.0.1.30"),sQuery(id+"F0.wireOp",EDGE,"E3.0.1.32"),subQ1,sQuery(id+"F0.wireOp",EDGE,"E4.top"),subQ0,sQuery(id+"F0.wireOp",EDGE,"E4.right"),sQuery(id+"F0.wireOp",EDGE,"E9.left"),sQuery(id+"F0.wireOp",EDGE,"E9.right"),sQuery(id+"F0.wireOp",EDGE,"E13.bottom"),sQuery(id+"F0.wireOp",EDGE,"E13.top"),sQuery(id+"F0.wireOp",EDGE,"E13.left"),sQuery(id+"F0.wireOp",EDGE,"E13.right"),sQuery(id+"F0.wireOp",EDGE,"E14.bottom"),sQuery(id+"F0.wireOp",EDGE,"E14.top"),sQuery(id+"F0.wireOp",EDGE,"E14.left"),sQuery(id+"F0.wireOp",EDGE,"E14.right"),sQuery(id+"F0.wireOp",EDGE,"E15.left"),sQuery(id+"F0.wireOp",EDGE,"E15.right"),sQuery(id+"F0.wireOp",EDGE,"E20.bottom"),sQuery(id+"F0.wireOp",EDGE,"E20.top"),sQuery(id+"F0.wireOp",EDGE,"E20.left"),sQuery(id+"F0.wireOp",EDGE,"E20.right"),sQuery(id+"F0.wireOp",EDGE,"E21.bottom"),sQuery(id+"F0.wireOp",EDGE,"E21.top"),sQuery(id+"F0.wireOp",EDGE,"E21.left"),sQuery(id+"F0.wireOp",EDGE,"E21.right"),sQuery(id+"F0.wireOp",EDGE,"E22.bottom"),sQuery(id+"F0.wireOp",EDGE,"E22.top"),sQuery(id+"F0.wireOp",EDGE,"E22.left"),sQuery(id+"F0.wireOp",EDGE,"E23.bottom"),sQuery(id+"F0.wireOp",EDGE,"E23.top"),sQuery(id+"F0.wireOp",EDGE,"E23.right"),sQuery(id+"F0.wireOp",EDGE,"E24.bottom"),sQuery(id+"F0.wireOp",EDGE,"E24.top"),sQuery(id+"F0.wireOp",EDGE,"E24.right"),sQuery(id+"F0.wireOp",EDGE,"E25.bottom"),sQuery(id+"F0.wireOp",EDGE,"E25.top"),sQuery(id+"F0.wireOp",EDGE,"E25.right"),sQuery(id+"F0.wireOp",EDGE,"E26.bottom"),sQuery(id+"F0.wireOp",EDGE,"E26.top"),sQuery(id+"F0.wireOp",EDGE,"E26.right"),sQuery(id+"F0.wireOp",EDGE,"E31.bottom"),sQuery(id+"F0.wireOp",EDGE,"E31.top"),sQuery(id+"F0.wireOp",EDGE,"E31.right")])],"isStart":false})],"blendedInto":[makeQuery(id+"F1.opExtrude","CAP_FACE",FACE,{"disambiguationData":[OSD([sQuery(id+"F0.wireOp",EDGE,"E0.bottom"),sQuery(id+"F0.wireOp",EDGE,"E0.top"),sQuery(id+"F0.wireOp",EDGE,"E0.left"),sQuery(id+"F0.wireOp",EDGE,"E0.right"),sQuery(id+"F0.wireOp",EDGE,"E1.0.1.1"),sQuery(id+"F0.wireOp",EDGE,"E1.0.1.2"),sQuery(id+"F0.wireOp",EDGE,"E1.0.1.3"),sQuery(id+"F0.wireOp",EDGE,"E1.0.1.4"),sQuery(id+"F0.wireOp",EDGE,"E1.0.2.1"),sQuery(id+"F0.wireOp",EDGE,"E1.0.2.2"),sQuery(id+"F0.wireOp",EDGE,"E1.0.2.3"),sQuery(id+"F0.wireOp",EDGE,"E1.0.2.4"),sQuery(id+"F0.wireOp",EDGE,"E1.1.0.1"),sQuery(id+"F0.wireOp",EDGE,"E1.1.0.2"),sQuery(id+"F0.wireOp",EDGE,"E1.1.0.3"),sQuery(id+"F0.wireOp",EDGE,"E1.1.0.4"),sQuery(id+"F0.wireOp",EDGE,"E1.1.1.1"),sQuery(id+"F0.wireOp",EDGE,"E1.1.1.2"),sQuery(id+"F0.wireOp",EDGE,"E1.1.1.3"),sQuery(id+"F0.wireOp",EDGE,"E1.1.1.4"),sQuery(id+"F0.wireOp",EDGE,"E1.1.2.1"),sQuery(id+"F0.wireOp",EDGE,"E1.1.2.2"),sQuery(id+"F0.wireOp",EDGE,"E1.1.2.3"),sQuery(id+"F0.wireOp",EDGE,"E1.1.2.4"),sQuery(id+"F0.wireOp",EDGE,"E1.2.0.1"),sQuery(id+"F0.wireOp",EDGE,"E1.2.0.2"),sQuery(id+"F0.wireOp",EDGE,"E1.2.0.3"),sQuery(id+"F0.wireOp",EDGE,"E1.2.0.4"),sQuery(id+"F0.wireOp",EDGE,"E1.2.1.1"),sQuery(id+"F0.wireOp",EDGE,"E1.2.1.2"),sQuery(id+"F0.wireOp",EDGE,"E1.2.1.3"),sQuery(id+"F0.wireOp",EDGE,"E1.2.1.4"),sQuery(id+"F0.wireOp",EDGE,"E1.2.2.1"),sQuery(id+"F0.wireOp",EDGE,"E1.2.2.2"),sQuery(id+"F0.wireOp",EDGE,"E1.2.2.3"),sQuery(id+"F0.wireOp",EDGE,"E1.2.2.4"),sQuery(id+"F0.wireOp",EDGE,"E2.1.0.0"),sQuery(id+"F0.wireOp",EDGE,"E2.1.0.1"),sQuery(id+"F0.wireOp",EDGE,"E2.1.0.2"),sQuery(id+"F0.wireOp",EDGE,"E2.1.0.3"),sQuery(id+"F0.wireOp",EDGE,"E2.1.0.5"),sQuery(id+"F0.wireOp",EDGE,"E2.1.0.7"),sQuery(id+"F0.wireOp",EDGE,"E2.1.0.12"),sQuery(id+"F0.wireOp",EDGE,"E2.1.0.13"),sQuery(id+"F0.wireOp",EDGE,"E2.1.0.14"),sQuery(id+"F0.wireOp",EDGE,"E2.1.0.15"),sQuery(id+"F0.wireOp",EDGE,"E2.1.0.16"),sQuery(id+"F0.wireOp",EDGE,"E2.1.0.17"),sQuery(id+"F0.wireOp",EDGE,"E2.1.0.18"),sQuery(id+"F0.wireOp",EDGE,"E2.1.0.19"),sQuery(id+"F0.wireOp",EDGE,"E2.1.0.20"),sQuery(id+"F0.wireOp",EDGE,"E2.1.0.21"),sQuery(id+"F0.wireOp",EDGE,"E2.1.0.22"),sQuery(id+"F0.wireOp",EDGE,"E2.1.0.23"),sQuery(id+"F0.wireOp",EDGE,"E2.1.0.25"),sQuery(id+"F0.wireOp",EDGE,"E2.1.0.27"),sQuery(id+"F0.wireOp",EDGE,"E2.1.0.28"),sQuery(id+"F0.wireOp",EDGE,"E2.1.0.30"),sQuery(id+"F0.wireOp",EDGE,"E2.1.0.32"),sQuery(id+"F0.wireOp",EDGE,"E2.1.0.33"),sQuery(id+"F0.wireOp",EDGE,"E2.1.0.34"),sQuery(id+"F0.wireOp",EDGE,"E2.1.0.35"),sQuery(id+"F0.wireOp",EDGE,"E2.1.0.36"),sQuery(id+"F0.wireOp",EDGE,"E2.1.0.37"),sQuery(id+"F0.wireOp",EDGE,"E2.1.0.38"),sQuery(id+"F0.wireOp",EDGE,"E2.1.0.40"),sQuery(id+"F0.wireOp",EDGE,"E2.1.0.41"),sQuery(id+"F0.wireOp",EDGE,"E2.1.0.42"),sQuery(id+"F0.wireOp",EDGE,"E2.1.0.43"),sQuery(id+"F0.wireOp",EDGE,"E2.1.0.44"),sQuery(id+"F0.wireOp",EDGE,"E2.1.0.45"),sQuery(id+"F0.wireOp",EDGE,"E2.1.0.46"),sQuery(id+"F0.wireOp",EDGE,"E3.0.1.1"),sQuery(id+"F0.wireOp",EDGE,"E3.0.1.2"),sQuery(id+"F0.wireOp",EDGE,"E3.0.1.3"),sQuery(id+"F0.wireOp",EDGE,"E3.0.1.4"),sQuery(id+"F0.wireOp",EDGE,"E3.0.1.5"),sQuery(id+"F0.wireOp",EDGE,"E3.0.1.6"),sQuery(id+"F0.wireOp",EDGE,"E3.0.1.7"),sQuery(id+"F0.wireOp",EDGE,"E3.0.1.8"),sQuery(id+"F0.wireOp",EDGE,"E3.0.1.9"),sQuery(id+"F0.wireOp",EDGE,"E3.0.1.10"),sQuery(id+"F0.wireOp",EDGE,"E3.0.1.11"),sQuery(id+"F0.wireOp",EDGE,"E3.0.1.12"),sQuery(id+"F0.wireOp",EDGE,"E3.0.1.14"),sQuery(id+"F0.wireOp",EDGE,"E3.0.1.15"),sQuery(id+"F0.wireOp",EDGE,"E3.0.1.16"),sQuery(id+"F0.wireOp",EDGE,"E3.0.1.17"),sQuery(id+"F0.wireOp",EDGE,"E3.0.1.20"),sQuery(id+"F0.wireOp",EDGE,"E3.0.1.24"),sQuery(id+"F0.wireOp",EDGE,"E3.0.1.26"),sQuery(id+"F0.wireOp",EDGE,"E3.0.1.27"),sQuery(id+"F0.wireOp",EDGE,"E3.0.1.28"),sQuery(id+"F0.wireOp",EDGE,"E3.0.1.29"),sQuery(id+"F0.wireOp",EDGE,"E3.0.1.30"),sQuery(id+"F0.wireOp",EDGE,"E3.0.1.32"),subQ1,sQuery(id+"F0.wireOp",EDGE,"E4.top"),subQ0,sQuery(id+"F0.wireOp",EDGE,"E4.right"),sQuery(id+"F0.wireOp",EDGE,"E9.left"),sQuery(id+"F0.wireOp",EDGE,"E9.right"),sQuery(id+"F0.wireOp",EDGE,"E13.bottom"),sQuery(id+"F0.wireOp",EDGE,"E13.top"),sQuery(id+"F0.wireOp",EDGE,"E13.left"),sQuery(id+"F0.wireOp",EDGE,"E13.right"),sQuery(id+"F0.wireOp",EDGE,"E14.bottom"),sQuery(id+"F0.wireOp",EDGE,"E14.top"),sQuery(id+"F0.wireOp",EDGE,"E14.left"),sQuery(id+"F0.wireOp",EDGE,"E14.right"),sQuery(id+"F0.wireOp",EDGE,"E15.left"),sQuery(id+"F0.wireOp",EDGE,"E15.right"),sQuery(id+"F0.wireOp",EDGE,"E20.bottom"),sQuery(id+"F0.wireOp",EDGE,"E20.top"),sQuery(id+"F0.wireOp",EDGE,"E20.left"),sQuery(id+"F0.wireOp",EDGE,"E20.right"),sQuery(id+"F0.wireOp",EDGE,"E21.bottom"),sQuery(id+"F0.wireOp",EDGE,"E21.top"),sQuery(id+"F0.wireOp",EDGE,"E21.left"),sQuery(id+"F0.wireOp",EDGE,"E21.right"),sQuery(id+"F0.wireOp",EDGE,"E22.bottom"),sQuery(id+"F0.wireOp",EDGE,"E22.top"),sQuery(id+"F0.wireOp",EDGE,"E22.left"),sQuery(id+"F0.wireOp",EDGE,"E23.bottom"),sQuery(id+"F0.wireOp",EDGE,"E23.top"),sQuery(id+"F0.wireOp",EDGE,"E23.right"),sQuery(id+"F0.wireOp",EDGE,"E24.bottom"),sQuery(id+"F0.wireOp",EDGE,"E24.top"),sQuery(id+"F0.wireOp",EDGE,"E24.right"),sQuery(id+"F0.wireOp",EDGE,"E25.bottom"),sQuery(id+"F0.wireOp",EDGE,"E25.top"),sQuery(id+"F0.wireOp",EDGE,"E25.right"),sQuery(id+"F0.wireOp",EDGE,"E26.bottom"),sQuery(id+"F0.wireOp",EDGE,"E26.top"),sQuery(id+"F0.wireOp",EDGE,"E26.right"),sQuery(id+"F0.wireOp",EDGE,"E31.bottom"),sQuery(id+"F0.wireOp",EDGE,"E31.top"),sQuery(id+"F0.wireOp",EDGE,"E31.right")])],"isStart":false})]});}
            var Q20;
            {var subQ0=sQuery(id+"F0.wireOp",EDGE,"E4.left");Q20=makeQuery(id+"F3.opFillet","BLEND_EDGE",EDGE,{"blendedFrom":[makeQuery(id+"F1.opExtrude","SWEPT_EDGE",EDGE,{"disambiguationData":[OSD([sQuery(id+"F0.wireOp",EDGE,"E4.top"),subQ0])]}),makeQuery(id+"F1.opExtrude","SWEPT_FACE",FACE,{"disambiguationData":[OSD([subQ0])]})],"blendedInto":[makeQuery(id+"F1.opExtrude","SWEPT_FACE",FACE,{"disambiguationData":[OSD([subQ0])]})]});}
            var Q21;
            Q21=makeQuery(id+"F1.opExtrude","CAP_EDGE",EDGE,{"disambiguationData":[OSD([sQuery(id+"F0.wireOp",EDGE,"E4.left")])],"isStart":true});
            var Q22;
            {var subQ0=sQuery(id+"F0.wireOp",EDGE,"E4.left");Q22=makeQuery(id+"F2.opFillet","BLEND_EDGE",EDGE,{"blendedFrom":[makeQuery(id+"F1.opExtrude","SWEPT_EDGE",EDGE,{"disambiguationData":[OSD([sQuery(id+"F0.wireOp",EDGE,"E4.bottom"),subQ0])]}),makeQuery(id+"F1.opExtrude","SWEPT_FACE",FACE,{"disambiguationData":[OSD([subQ0])]})],"blendedInto":[makeQuery(id+"F1.opExtrude","SWEPT_FACE",FACE,{"disambiguationData":[OSD([subQ0])]})]});}
            var Q23;
            {var subQ0=sQuery(id+"F0.wireOp",EDGE,"E4.left");var subQ1=sQuery(id+"F0.wireOp",EDGE,"E4.bottom");Q23=makeQuery(id+"F2.opFillet","BLEND_EDGE",EDGE,{"blendedFrom":[makeQuery(id+"F1.opExtrude","SWEPT_EDGE",EDGE,{"disambiguationData":[OSD([subQ1,subQ0])]}),makeQuery(id+"F1.opExtrude","CAP_FACE",FACE,{"disambiguationData":[OSD([sQuery(id+"F0.wireOp",EDGE,"E0.bottom"),sQuery(id+"F0.wireOp",EDGE,"E0.top"),sQuery(id+"F0.wireOp",EDGE,"E0.left"),sQuery(id+"F0.wireOp",EDGE,"E0.right"),sQuery(id+"F0.wireOp",EDGE,"E1.0.1.1"),sQuery(id+"F0.wireOp",EDGE,"E1.0.1.2"),sQuery(id+"F0.wireOp",EDGE,"E1.0.1.3"),sQuery(id+"F0.wireOp",EDGE,"E1.0.1.4"),sQuery(id+"F0.wireOp",EDGE,"E1.0.2.1"),sQuery(id+"F0.wireOp",EDGE,"E1.0.2.2"),sQuery(id+"F0.wireOp",EDGE,"E1.0.2.3"),sQuery(id+"F0.wireOp",EDGE,"E1.0.2.4"),sQuery(id+"F0.wireOp",EDGE,"E1.1.0.1"),sQuery(id+"F0.wireOp",EDGE,"E1.1.0.2"),sQuery(id+"F0.wireOp",EDGE,"E1.1.0.3"),sQuery(id+"F0.wireOp",EDGE,"E1.1.0.4"),sQuery(id+"F0.wireOp",EDGE,"E1.1.1.1"),sQuery(id+"F0.wireOp",EDGE,"E1.1.1.2"),sQuery(id+"F0.wireOp",EDGE,"E1.1.1.3"),sQuery(id+"F0.wireOp",EDGE,"E1.1.1.4"),sQuery(id+"F0.wireOp",EDGE,"E1.1.2.1"),sQuery(id+"F0.wireOp",EDGE,"E1.1.2.2"),sQuery(id+"F0.wireOp",EDGE,"E1.1.2.3"),sQuery(id+"F0.wireOp",EDGE,"E1.1.2.4"),sQuery(id+"F0.wireOp",EDGE,"E1.2.0.1"),sQuery(id+"F0.wireOp",EDGE,"E1.2.0.2"),sQuery(id+"F0.wireOp",EDGE,"E1.2.0.3"),sQuery(id+"F0.wireOp",EDGE,"E1.2.0.4"),sQuery(id+"F0.wireOp",EDGE,"E1.2.1.1"),sQuery(id+"F0.wireOp",EDGE,"E1.2.1.2"),sQuery(id+"F0.wireOp",EDGE,"E1.2.1.3"),sQuery(id+"F0.wireOp",EDGE,"E1.2.1.4"),sQuery(id+"F0.wireOp",EDGE,"E1.2.2.1"),sQuery(id+"F0.wireOp",EDGE,"E1.2.2.2"),sQuery(id+"F0.wireOp",EDGE,"E1.2.2.3"),sQuery(id+"F0.wireOp",EDGE,"E1.2.2.4"),sQuery(id+"F0.wireOp",EDGE,"E2.1.0.0"),sQuery(id+"F0.wireOp",EDGE,"E2.1.0.1"),sQuery(id+"F0.wireOp",EDGE,"E2.1.0.2"),sQuery(id+"F0.wireOp",EDGE,"E2.1.0.3"),sQuery(id+"F0.wireOp",EDGE,"E2.1.0.5"),sQuery(id+"F0.wireOp",EDGE,"E2.1.0.7"),sQuery(id+"F0.wireOp",EDGE,"E2.1.0.12"),sQuery(id+"F0.wireOp",EDGE,"E2.1.0.13"),sQuery(id+"F0.wireOp",EDGE,"E2.1.0.14"),sQuery(id+"F0.wireOp",EDGE,"E2.1.0.15"),sQuery(id+"F0.wireOp",EDGE,"E2.1.0.16"),sQuery(id+"F0.wireOp",EDGE,"E2.1.0.17"),sQuery(id+"F0.wireOp",EDGE,"E2.1.0.18"),sQuery(id+"F0.wireOp",EDGE,"E2.1.0.19"),sQuery(id+"F0.wireOp",EDGE,"E2.1.0.20"),sQuery(id+"F0.wireOp",EDGE,"E2.1.0.21"),sQuery(id+"F0.wireOp",EDGE,"E2.1.0.22"),sQuery(id+"F0.wireOp",EDGE,"E2.1.0.23"),sQuery(id+"F0.wireOp",EDGE,"E2.1.0.25"),sQuery(id+"F0.wireOp",EDGE,"E2.1.0.27"),sQuery(id+"F0.wireOp",EDGE,"E2.1.0.28"),sQuery(id+"F0.wireOp",EDGE,"E2.1.0.30"),sQuery(id+"F0.wireOp",EDGE,"E2.1.0.32"),sQuery(id+"F0.wireOp",EDGE,"E2.1.0.33"),sQuery(id+"F0.wireOp",EDGE,"E2.1.0.34"),sQuery(id+"F0.wireOp",EDGE,"E2.1.0.35"),sQuery(id+"F0.wireOp",EDGE,"E2.1.0.36"),sQuery(id+"F0.wireOp",EDGE,"E2.1.0.37"),sQuery(id+"F0.wireOp",EDGE,"E2.1.0.38"),sQuery(id+"F0.wireOp",EDGE,"E2.1.0.40"),sQuery(id+"F0.wireOp",EDGE,"E2.1.0.41"),sQuery(id+"F0.wireOp",EDGE,"E2.1.0.42"),sQuery(id+"F0.wireOp",EDGE,"E2.1.0.43"),sQuery(id+"F0.wireOp",EDGE,"E2.1.0.44"),sQuery(id+"F0.wireOp",EDGE,"E2.1.0.45"),sQuery(id+"F0.wireOp",EDGE,"E2.1.0.46"),sQuery(id+"F0.wireOp",EDGE,"E3.0.1.1"),sQuery(id+"F0.wireOp",EDGE,"E3.0.1.2"),sQuery(id+"F0.wireOp",EDGE,"E3.0.1.3"),sQuery(id+"F0.wireOp",EDGE,"E3.0.1.4"),sQuery(id+"F0.wireOp",EDGE,"E3.0.1.5"),sQuery(id+"F0.wireOp",EDGE,"E3.0.1.6"),sQuery(id+"F0.wireOp",EDGE,"E3.0.1.7"),sQuery(id+"F0.wireOp",EDGE,"E3.0.1.8"),sQuery(id+"F0.wireOp",EDGE,"E3.0.1.9"),sQuery(id+"F0.wireOp",EDGE,"E3.0.1.10"),sQuery(id+"F0.wireOp",EDGE,"E3.0.1.11"),sQuery(id+"F0.wireOp",EDGE,"E3.0.1.12"),sQuery(id+"F0.wireOp",EDGE,"E3.0.1.14"),sQuery(id+"F0.wireOp",EDGE,"E3.0.1.15"),sQuery(id+"F0.wireOp",EDGE,"E3.0.1.16"),sQuery(id+"F0.wireOp",EDGE,"E3.0.1.17"),sQuery(id+"F0.wireOp",EDGE,"E3.0.1.20"),sQuery(id+"F0.wireOp",EDGE,"E3.0.1.24"),sQuery(id+"F0.wireOp",EDGE,"E3.0.1.26"),sQuery(id+"F0.wireOp",EDGE,"E3.0.1.27"),sQuery(id+"F0.wireOp",EDGE,"E3.0.1.28"),sQuery(id+"F0.wireOp",EDGE,"E3.0.1.29"),sQuery(id+"F0.wireOp",EDGE,"E3.0.1.30"),sQuery(id+"F0.wireOp",EDGE,"E3.0.1.32"),subQ1,sQuery(id+"F0.wireOp",EDGE,"E4.top"),subQ0,sQuery(id+"F0.wireOp",EDGE,"E4.right"),sQuery(id+"F0.wireOp",EDGE,"E9.left"),sQuery(id+"F0.wireOp",EDGE,"E9.right"),sQuery(id+"F0.wireOp",EDGE,"E13.bottom"),sQuery(id+"F0.wireOp",EDGE,"E13.top"),sQuery(id+"F0.wireOp",EDGE,"E13.left"),sQuery(id+"F0.wireOp",EDGE,"E13.right"),sQuery(id+"F0.wireOp",EDGE,"E14.bottom"),sQuery(id+"F0.wireOp",EDGE,"E14.top"),sQuery(id+"F0.wireOp",EDGE,"E14.left"),sQuery(id+"F0.wireOp",EDGE,"E14.right"),sQuery(id+"F0.wireOp",EDGE,"E15.left"),sQuery(id+"F0.wireOp",EDGE,"E15.right"),sQuery(id+"F0.wireOp",EDGE,"E20.bottom"),sQuery(id+"F0.wireOp",EDGE,"E20.top"),sQuery(id+"F0.wireOp",EDGE,"E20.left"),sQuery(id+"F0.wireOp",EDGE,"E20.right"),sQuery(id+"F0.wireOp",EDGE,"E21.bottom"),sQuery(id+"F0.wireOp",EDGE,"E21.top"),sQuery(id+"F0.wireOp",EDGE,"E21.left"),sQuery(id+"F0.wireOp",EDGE,"E21.right"),sQuery(id+"F0.wireOp",EDGE,"E22.bottom"),sQuery(id+"F0.wireOp",EDGE,"E22.top"),sQuery(id+"F0.wireOp",EDGE,"E22.left"),sQuery(id+"F0.wireOp",EDGE,"E23.bottom"),sQuery(id+"F0.wireOp",EDGE,"E23.top"),sQuery(id+"F0.wireOp",EDGE,"E23.right"),sQuery(id+"F0.wireOp",EDGE,"E24.bottom"),sQuery(id+"F0.wireOp",EDGE,"E24.top"),sQuery(id+"F0.wireOp",EDGE,"E24.right"),sQuery(id+"F0.wireOp",EDGE,"E25.bottom"),sQuery(id+"F0.wireOp",EDGE,"E25.top"),sQuery(id+"F0.wireOp",EDGE,"E25.right"),sQuery(id+"F0.wireOp",EDGE,"E26.bottom"),sQuery(id+"F0.wireOp",EDGE,"E26.top"),sQuery(id+"F0.wireOp",EDGE,"E26.right"),sQuery(id+"F0.wireOp",EDGE,"E31.bottom"),sQuery(id+"F0.wireOp",EDGE,"E31.top"),sQuery(id+"F0.wireOp",EDGE,"E31.right")])],"isStart":true})],"blendedInto":[makeQuery(id+"F1.opExtrude","CAP_FACE",FACE,{"disambiguationData":[OSD([sQuery(id+"F0.wireOp",EDGE,"E0.bottom"),sQuery(id+"F0.wireOp",EDGE,"E0.top"),sQuery(id+"F0.wireOp",EDGE,"E0.left"),sQuery(id+"F0.wireOp",EDGE,"E0.right"),sQuery(id+"F0.wireOp",EDGE,"E1.0.1.1"),sQuery(id+"F0.wireOp",EDGE,"E1.0.1.2"),sQuery(id+"F0.wireOp",EDGE,"E1.0.1.3"),sQuery(id+"F0.wireOp",EDGE,"E1.0.1.4"),sQuery(id+"F0.wireOp",EDGE,"E1.0.2.1"),sQuery(id+"F0.wireOp",EDGE,"E1.0.2.2"),sQuery(id+"F0.wireOp",EDGE,"E1.0.2.3"),sQuery(id+"F0.wireOp",EDGE,"E1.0.2.4"),sQuery(id+"F0.wireOp",EDGE,"E1.1.0.1"),sQuery(id+"F0.wireOp",EDGE,"E1.1.0.2"),sQuery(id+"F0.wireOp",EDGE,"E1.1.0.3"),sQuery(id+"F0.wireOp",EDGE,"E1.1.0.4"),sQuery(id+"F0.wireOp",EDGE,"E1.1.1.1"),sQuery(id+"F0.wireOp",EDGE,"E1.1.1.2"),sQuery(id+"F0.wireOp",EDGE,"E1.1.1.3"),sQuery(id+"F0.wireOp",EDGE,"E1.1.1.4"),sQuery(id+"F0.wireOp",EDGE,"E1.1.2.1"),sQuery(id+"F0.wireOp",EDGE,"E1.1.2.2"),sQuery(id+"F0.wireOp",EDGE,"E1.1.2.3"),sQuery(id+"F0.wireOp",EDGE,"E1.1.2.4"),sQuery(id+"F0.wireOp",EDGE,"E1.2.0.1"),sQuery(id+"F0.wireOp",EDGE,"E1.2.0.2"),sQuery(id+"F0.wireOp",EDGE,"E1.2.0.3"),sQuery(id+"F0.wireOp",EDGE,"E1.2.0.4"),sQuery(id+"F0.wireOp",EDGE,"E1.2.1.1"),sQuery(id+"F0.wireOp",EDGE,"E1.2.1.2"),sQuery(id+"F0.wireOp",EDGE,"E1.2.1.3"),sQuery(id+"F0.wireOp",EDGE,"E1.2.1.4"),sQuery(id+"F0.wireOp",EDGE,"E1.2.2.1"),sQuery(id+"F0.wireOp",EDGE,"E1.2.2.2"),sQuery(id+"F0.wireOp",EDGE,"E1.2.2.3"),sQuery(id+"F0.wireOp",EDGE,"E1.2.2.4"),sQuery(id+"F0.wireOp",EDGE,"E2.1.0.0"),sQuery(id+"F0.wireOp",EDGE,"E2.1.0.1"),sQuery(id+"F0.wireOp",EDGE,"E2.1.0.2"),sQuery(id+"F0.wireOp",EDGE,"E2.1.0.3"),sQuery(id+"F0.wireOp",EDGE,"E2.1.0.5"),sQuery(id+"F0.wireOp",EDGE,"E2.1.0.7"),sQuery(id+"F0.wireOp",EDGE,"E2.1.0.12"),sQuery(id+"F0.wireOp",EDGE,"E2.1.0.13"),sQuery(id+"F0.wireOp",EDGE,"E2.1.0.14"),sQuery(id+"F0.wireOp",EDGE,"E2.1.0.15"),sQuery(id+"F0.wireOp",EDGE,"E2.1.0.16"),sQuery(id+"F0.wireOp",EDGE,"E2.1.0.17"),sQuery(id+"F0.wireOp",EDGE,"E2.1.0.18"),sQuery(id+"F0.wireOp",EDGE,"E2.1.0.19"),sQuery(id+"F0.wireOp",EDGE,"E2.1.0.20"),sQuery(id+"F0.wireOp",EDGE,"E2.1.0.21"),sQuery(id+"F0.wireOp",EDGE,"E2.1.0.22"),sQuery(id+"F0.wireOp",EDGE,"E2.1.0.23"),sQuery(id+"F0.wireOp",EDGE,"E2.1.0.25"),sQuery(id+"F0.wireOp",EDGE,"E2.1.0.27"),sQuery(id+"F0.wireOp",EDGE,"E2.1.0.28"),sQuery(id+"F0.wireOp",EDGE,"E2.1.0.30"),sQuery(id+"F0.wireOp",EDGE,"E2.1.0.32"),sQuery(id+"F0.wireOp",EDGE,"E2.1.0.33"),sQuery(id+"F0.wireOp",EDGE,"E2.1.0.34"),sQuery(id+"F0.wireOp",EDGE,"E2.1.0.35"),sQuery(id+"F0.wireOp",EDGE,"E2.1.0.36"),sQuery(id+"F0.wireOp",EDGE,"E2.1.0.37"),sQuery(id+"F0.wireOp",EDGE,"E2.1.0.38"),sQuery(id+"F0.wireOp",EDGE,"E2.1.0.40"),sQuery(id+"F0.wireOp",EDGE,"E2.1.0.41"),sQuery(id+"F0.wireOp",EDGE,"E2.1.0.42"),sQuery(id+"F0.wireOp",EDGE,"E2.1.0.43"),sQuery(id+"F0.wireOp",EDGE,"E2.1.0.44"),sQuery(id+"F0.wireOp",EDGE,"E2.1.0.45"),sQuery(id+"F0.wireOp",EDGE,"E2.1.0.46"),sQuery(id+"F0.wireOp",EDGE,"E3.0.1.1"),sQuery(id+"F0.wireOp",EDGE,"E3.0.1.2"),sQuery(id+"F0.wireOp",EDGE,"E3.0.1.3"),sQuery(id+"F0.wireOp",EDGE,"E3.0.1.4"),sQuery(id+"F0.wireOp",EDGE,"E3.0.1.5"),sQuery(id+"F0.wireOp",EDGE,"E3.0.1.6"),sQuery(id+"F0.wireOp",EDGE,"E3.0.1.7"),sQuery(id+"F0.wireOp",EDGE,"E3.0.1.8"),sQuery(id+"F0.wireOp",EDGE,"E3.0.1.9"),sQuery(id+"F0.wireOp",EDGE,"E3.0.1.10"),sQuery(id+"F0.wireOp",EDGE,"E3.0.1.11"),sQuery(id+"F0.wireOp",EDGE,"E3.0.1.12"),sQuery(id+"F0.wireOp",EDGE,"E3.0.1.14"),sQuery(id+"F0.wireOp",EDGE,"E3.0.1.15"),sQuery(id+"F0.wireOp",EDGE,"E3.0.1.16"),sQuery(id+"F0.wireOp",EDGE,"E3.0.1.17"),sQuery(id+"F0.wireOp",EDGE,"E3.0.1.20"),sQuery(id+"F0.wireOp",EDGE,"E3.0.1.24"),sQuery(id+"F0.wireOp",EDGE,"E3.0.1.26"),sQuery(id+"F0.wireOp",EDGE,"E3.0.1.27"),sQuery(id+"F0.wireOp",EDGE,"E3.0.1.28"),sQuery(id+"F0.wireOp",EDGE,"E3.0.1.29"),sQuery(id+"F0.wireOp",EDGE,"E3.0.1.30"),sQuery(id+"F0.wireOp",EDGE,"E3.0.1.32"),subQ1,sQuery(id+"F0.wireOp",EDGE,"E4.top"),subQ0,sQuery(id+"F0.wireOp",EDGE,"E4.right"),sQuery(id+"F0.wireOp",EDGE,"E9.left"),sQuery(id+"F0.wireOp",EDGE,"E9.right"),sQuery(id+"F0.wireOp",EDGE,"E13.bottom"),sQuery(id+"F0.wireOp",EDGE,"E13.top"),sQuery(id+"F0.wireOp",EDGE,"E13.left"),sQuery(id+"F0.wireOp",EDGE,"E13.right"),sQuery(id+"F0.wireOp",EDGE,"E14.bottom"),sQuery(id+"F0.wireOp",EDGE,"E14.top"),sQuery(id+"F0.wireOp",EDGE,"E14.left"),sQuery(id+"F0.wireOp",EDGE,"E14.right"),sQuery(id+"F0.wireOp",EDGE,"E15.left"),sQuery(id+"F0.wireOp",EDGE,"E15.right"),sQuery(id+"F0.wireOp",EDGE,"E20.bottom"),sQuery(id+"F0.wireOp",EDGE,"E20.top"),sQuery(id+"F0.wireOp",EDGE,"E20.left"),sQuery(id+"F0.wireOp",EDGE,"E20.right"),sQuery(id+"F0.wireOp",EDGE,"E21.bottom"),sQuery(id+"F0.wireOp",EDGE,"E21.top"),sQuery(id+"F0.wireOp",EDGE,"E21.left"),sQuery(id+"F0.wireOp",EDGE,"E21.right"),sQuery(id+"F0.wireOp",EDGE,"E22.bottom"),sQuery(id+"F0.wireOp",EDGE,"E22.top"),sQuery(id+"F0.wireOp",EDGE,"E22.left"),sQuery(id+"F0.wireOp",EDGE,"E23.bottom"),sQuery(id+"F0.wireOp",EDGE,"E23.top"),sQuery(id+"F0.wireOp",EDGE,"E23.right"),sQuery(id+"F0.wireOp",EDGE,"E24.bottom"),sQuery(id+"F0.wireOp",EDGE,"E24.top"),sQuery(id+"F0.wireOp",EDGE,"E24.right"),sQuery(id+"F0.wireOp",EDGE,"E25.bottom"),sQuery(id+"F0.wireOp",EDGE,"E25.top"),sQuery(id+"F0.wireOp",EDGE,"E25.right"),sQuery(id+"F0.wireOp",EDGE,"E26.bottom"),sQuery(id+"F0.wireOp",EDGE,"E26.top"),sQuery(id+"F0.wireOp",EDGE,"E26.right"),sQuery(id+"F0.wireOp",EDGE,"E31.bottom"),sQuery(id+"F0.wireOp",EDGE,"E31.top"),sQuery(id+"F0.wireOp",EDGE,"E31.right")])],"isStart":true})]});}
            fillet(context, id + "F4", {"entities" : qUnion([Q0, Q1, Q2, Q3, Q4, Q5, Q6, Q7, Q8, Q9, Q10, Q11, Q12, Q13, Q14, Q15, Q16, Q17, Q18, Q19, Q20, Q21, Q22, Q23]), "radius" : 0.5 * mm, "tangentPropagation" : true, "allowEdgeOverflow" : false});
        }
    });
